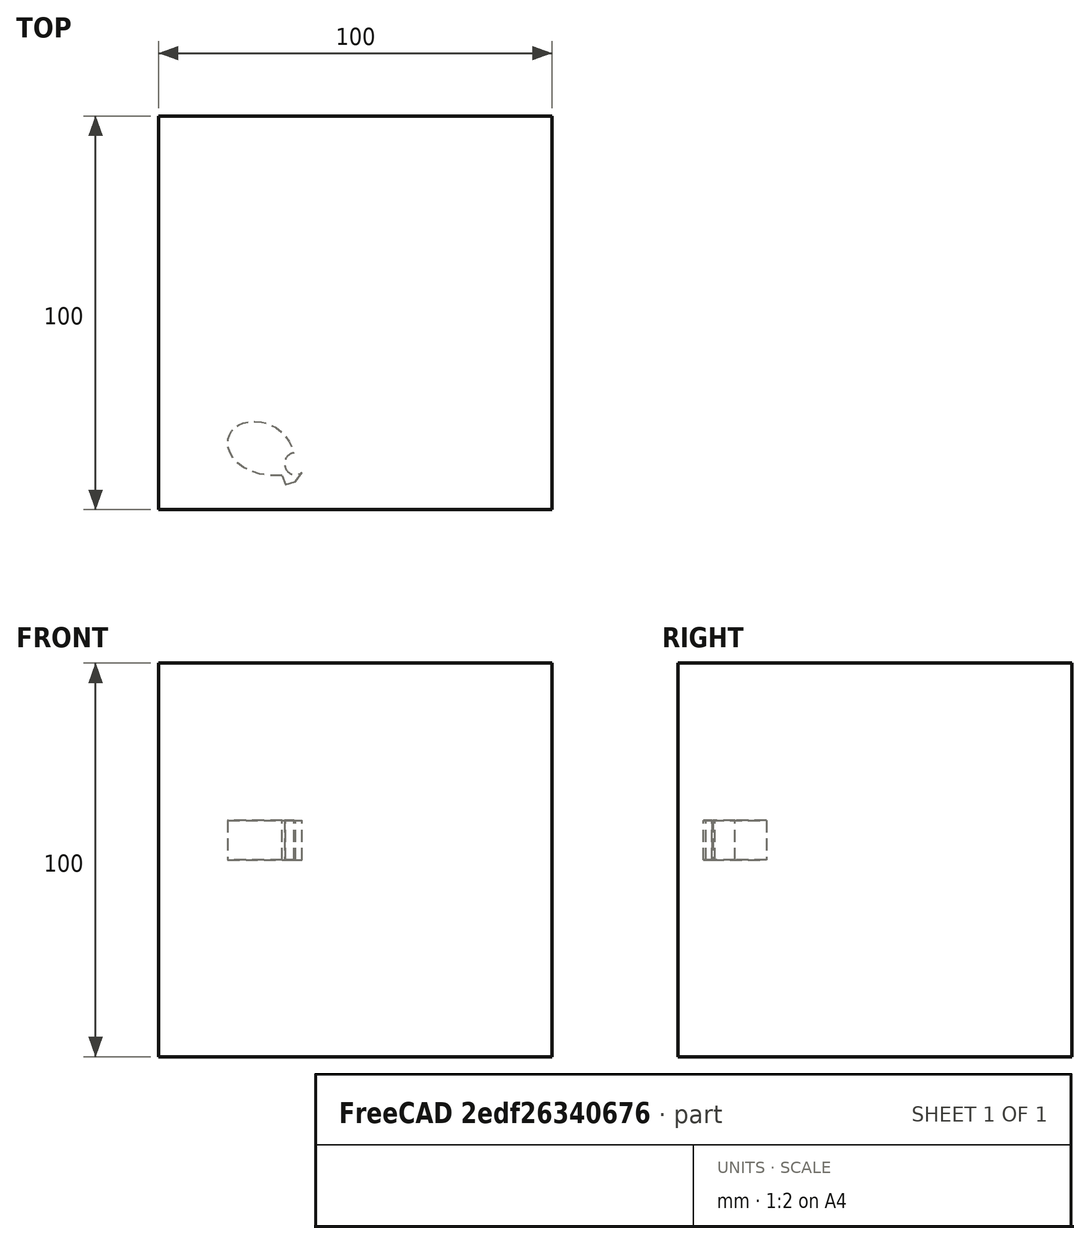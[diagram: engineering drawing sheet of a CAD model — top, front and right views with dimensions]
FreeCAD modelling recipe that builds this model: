
FCSTD DOCUMENT  (FreeCAD 1.0R39109 (Git))
Label: mirrorTest-3
License: All rights reserved
LicenseURL: http://en.wikipedia.org/wiki/All_rights_reserved
objects: App::DocumentObjectGroupPython×1248, Part::Mirroring×2, App::Part×2, Part::FeaturePython×1, Sketcher::SketchObject×1, Part::Extrusion×1
note: 6 computed .brp shape members not serialized (recipe doc carries the construction recipe); baked Part::Feature solids carry a one-line shape summary decoded from their .brp

FEATURE [App::DocumentObjectGroupPython] HALFPI  # scripted group (container) (typed FeaturePython)
  name = HALFPI
  value = pi/2.
FEATURE [App::DocumentObjectGroupPython] PI  # scripted group (container) (typed FeaturePython)
  name = PI
  value = 1.*pi
FEATURE [App::DocumentObjectGroupPython] TWOPI  # scripted group (container) (typed FeaturePython)
  name = TWOPI
  value = 2.*pi
FEATURE [App::DocumentObjectGroupPython] Constants  # scripted group (container) (typed FeaturePython)
  Group = -> [HALFPI,PI,TWOPI]
FEATURE [App::DocumentObjectGroupPython] Variables  # scripted group (container) (typed FeaturePython)
FEATURE [App::DocumentObjectGroupPython] Quantities  # scripted group (container) (typed FeaturePython)
FEATURE [App::DocumentObjectGroupPython] Isotopes  # scripted group (container) (typed FeaturePython)
FEATURE [App::DocumentObjectGroupPython] Elements  # scripted group (container) (typed FeaturePython)
FEATURE [App::DocumentObjectGroupPython] G4Isotopes  # scripted group (container) (typed FeaturePython)
FEATURE [App::DocumentObjectGroupPython] H_element  # scripted group (container) (typed FeaturePython)
  Z = 1
  atom_value = 1.008
  formula = H
  name = H_element
FEATURE [App::DocumentObjectGroupPython] He_element  # scripted group (container) (typed FeaturePython)
  Z = 2
  atom_value = 4.0026
  formula = He
  name = He_element
FEATURE [App::DocumentObjectGroupPython] Li_element  # scripted group (container) (typed FeaturePython)
  Z = 3
  atom_value = 6.94
  formula = Li
  name = Li_element
FEATURE [App::DocumentObjectGroupPython] Be_element  # scripted group (container) (typed FeaturePython)
  Z = 4
  atom_value = 9.01218
  formula = Be
  name = Be_element
FEATURE [App::DocumentObjectGroupPython] B_element  # scripted group (container) (typed FeaturePython)
  Z = 5
  atom_value = 10.81
  formula = B
  name = B_element
FEATURE [App::DocumentObjectGroupPython] C_element  # scripted group (container) (typed FeaturePython)
  Z = 6
  atom_value = 12.011
  formula = C
  name = C_element
FEATURE [App::DocumentObjectGroupPython] N_element  # scripted group (container) (typed FeaturePython)
  Z = 7
  atom_value = 14.007
  formula = N
  name = N_element
FEATURE [App::DocumentObjectGroupPython] O_element  # scripted group (container) (typed FeaturePython)
  Z = 8
  atom_value = 15.999
  formula = O
  name = O_element
FEATURE [App::DocumentObjectGroupPython] F_element  # scripted group (container) (typed FeaturePython)
  Z = 9
  atom_value = 18.9984
  formula = F
  name = F_element
FEATURE [App::DocumentObjectGroupPython] Ne_element  # scripted group (container) (typed FeaturePython)
  Z = 10
  atom_value = 20.1797
  formula = Ne
  name = Ne_element
FEATURE [App::DocumentObjectGroupPython] Na_element  # scripted group (container) (typed FeaturePython)
  Z = 11
  atom_value = 22.9898
  formula = Na
  name = Na_element
FEATURE [App::DocumentObjectGroupPython] Mg_element  # scripted group (container) (typed FeaturePython)
  Z = 12
  atom_value = 24.305
  formula = Mg
  name = Mg_element
FEATURE [App::DocumentObjectGroupPython] Al_element  # scripted group (container) (typed FeaturePython)
  Z = 13
  atom_value = 26.9815
  formula = Al
  name = Al_element
FEATURE [App::DocumentObjectGroupPython] Si_element  # scripted group (container) (typed FeaturePython)
  Z = 14
  atom_value = 28.085
  formula = Si
  name = Si_element
FEATURE [App::DocumentObjectGroupPython] P_element  # scripted group (container) (typed FeaturePython)
  Z = 15
  atom_value = 30.9738
  formula = P
  name = P_element
FEATURE [App::DocumentObjectGroupPython] S_element  # scripted group (container) (typed FeaturePython)
  Z = 16
  atom_value = 32.06
  formula = S
  name = S_element
FEATURE [App::DocumentObjectGroupPython] Cl_element  # scripted group (container) (typed FeaturePython)
  Z = 17
  atom_value = 35.45
  formula = Cl
  name = Cl_element
FEATURE [App::DocumentObjectGroupPython] Ar_element  # scripted group (container) (typed FeaturePython)
  Z = 18
  atom_value = 39.95
  formula = Ar
  name = Ar_element
FEATURE [App::DocumentObjectGroupPython] K_element  # scripted group (container) (typed FeaturePython)
  Z = 19
  atom_value = 39.0983
  formula = K
  name = K_element
FEATURE [App::DocumentObjectGroupPython] Ca_element  # scripted group (container) (typed FeaturePython)
  Z = 20
  atom_value = 40.078
  formula = Ca
  name = Ca_element
FEATURE [App::DocumentObjectGroupPython] Sc_element  # scripted group (container) (typed FeaturePython)
  Z = 21
  atom_value = 44.9559
  formula = Sc
  name = Sc_element
FEATURE [App::DocumentObjectGroupPython] Ti_element  # scripted group (container) (typed FeaturePython)
  Z = 22
  atom_value = 47.867
  formula = Ti
  name = Ti_element
FEATURE [App::DocumentObjectGroupPython] V_element  # scripted group (container) (typed FeaturePython)
  Z = 23
  atom_value = 50.9415
  formula = V
  name = V_element
FEATURE [App::DocumentObjectGroupPython] Cr_element  # scripted group (container) (typed FeaturePython)
  Z = 24
  atom_value = 51.9961
  formula = Cr
  name = Cr_element
FEATURE [App::DocumentObjectGroupPython] Mn_element  # scripted group (container) (typed FeaturePython)
  Z = 25
  atom_value = 54.938
  formula = Mn
  name = Mn_element
FEATURE [App::DocumentObjectGroupPython] Fe_element  # scripted group (container) (typed FeaturePython)
  Z = 26
  atom_value = 55.845
  formula = Fe
  name = Fe_element
FEATURE [App::DocumentObjectGroupPython] Co_element  # scripted group (container) (typed FeaturePython)
  Z = 27
  atom_value = 58.9332
  formula = Co
  name = Co_element
FEATURE [App::DocumentObjectGroupPython] Ni_element  # scripted group (container) (typed FeaturePython)
  Z = 28
  atom_value = 58.6934
  formula = Ni
  name = Ni_element
FEATURE [App::DocumentObjectGroupPython] Cu_element  # scripted group (container) (typed FeaturePython)
  Z = 29
  atom_value = 63.546
  formula = Cu
  name = Cu_element
FEATURE [App::DocumentObjectGroupPython] Zn_element  # scripted group (container) (typed FeaturePython)
  Z = 30
  atom_value = 65.38
  formula = Zn
  name = Zn_element
FEATURE [App::DocumentObjectGroupPython] Ga_element  # scripted group (container) (typed FeaturePython)
  Z = 31
  atom_value = 69.723
  formula = Ga
  name = Ga_element
FEATURE [App::DocumentObjectGroupPython] Ge_element  # scripted group (container) (typed FeaturePython)
  Z = 32
  atom_value = 72.63
  formula = Ge
  name = Ge_element
FEATURE [App::DocumentObjectGroupPython] As_element  # scripted group (container) (typed FeaturePython)
  Z = 33
  atom_value = 74.9216
  formula = As
  name = As_element
FEATURE [App::DocumentObjectGroupPython] Se_element  # scripted group (container) (typed FeaturePython)
  Z = 34
  atom_value = 78.971
  formula = Se
  name = Se_element
FEATURE [App::DocumentObjectGroupPython] Br_element  # scripted group (container) (typed FeaturePython)
  Z = 35
  atom_value = 79.904
  formula = Br
  name = Br_element
FEATURE [App::DocumentObjectGroupPython] Kr_element  # scripted group (container) (typed FeaturePython)
  Z = 36
  atom_value = 83.798
  formula = Kr
  name = Kr_element
FEATURE [App::DocumentObjectGroupPython] Rb_element  # scripted group (container) (typed FeaturePython)
  Z = 37
  atom_value = 85.4678
  formula = Rb
  name = Rb_element
FEATURE [App::DocumentObjectGroupPython] Sr_element  # scripted group (container) (typed FeaturePython)
  Z = 38
  atom_value = 87.62
  formula = Sr
  name = Sr_element
FEATURE [App::DocumentObjectGroupPython] Y_element  # scripted group (container) (typed FeaturePython)
  Z = 39
  atom_value = 88.9058
  formula = Y
  name = Y_element
FEATURE [App::DocumentObjectGroupPython] Zr_element  # scripted group (container) (typed FeaturePython)
  Z = 40
  atom_value = 91.224
  formula = Zr
  name = Zr_element
FEATURE [App::DocumentObjectGroupPython] Nb_element  # scripted group (container) (typed FeaturePython)
  Z = 41
  atom_value = 92.9064
  formula = Nb
  name = Nb_element
FEATURE [App::DocumentObjectGroupPython] Mo_element  # scripted group (container) (typed FeaturePython)
  Z = 42
  atom_value = 95.95
  formula = Mo
  name = Mo_element
FEATURE [App::DocumentObjectGroupPython] Tc_element  # scripted group (container) (typed FeaturePython)
  Z = 43
  atom_value = 97
  formula = Tc
  name = Tc_element
FEATURE [App::DocumentObjectGroupPython] Ru_element  # scripted group (container) (typed FeaturePython)
  Z = 44
  atom_value = 101.07
  formula = Ru
  name = Ru_element
FEATURE [App::DocumentObjectGroupPython] Rh_element  # scripted group (container) (typed FeaturePython)
  Z = 45
  atom_value = 102.905
  formula = Rh
  name = Rh_element
FEATURE [App::DocumentObjectGroupPython] Pd_element  # scripted group (container) (typed FeaturePython)
  Z = 46
  atom_value = 106.42
  formula = Pd
  name = Pd_element
FEATURE [App::DocumentObjectGroupPython] Ag_element  # scripted group (container) (typed FeaturePython)
  Z = 47
  atom_value = 107.868
  formula = Ag
  name = Ag_element
FEATURE [App::DocumentObjectGroupPython] Cd_element  # scripted group (container) (typed FeaturePython)
  Z = 48
  atom_value = 112.414
  formula = Cd
  name = Cd_element
FEATURE [App::DocumentObjectGroupPython] In_element  # scripted group (container) (typed FeaturePython)
  Z = 49
  atom_value = 114.818
  formula = In
  name = In_element
FEATURE [App::DocumentObjectGroupPython] Sn_element  # scripted group (container) (typed FeaturePython)
  Z = 50
  atom_value = 118.71
  formula = Sn
  name = Sn_element
FEATURE [App::DocumentObjectGroupPython] Sb_element  # scripted group (container) (typed FeaturePython)
  Z = 51
  atom_value = 121.76
  formula = Sb
  name = Sb_element
FEATURE [App::DocumentObjectGroupPython] Te_element  # scripted group (container) (typed FeaturePython)
  Z = 52
  atom_value = 127.6
  formula = Te
  name = Te_element
FEATURE [App::DocumentObjectGroupPython] I_element  # scripted group (container) (typed FeaturePython)
  Z = 53
  atom_value = 126.904
  formula = I
  name = I_element
FEATURE [App::DocumentObjectGroupPython] Xe_element  # scripted group (container) (typed FeaturePython)
  Z = 54
  atom_value = 131.293
  formula = Xe
  name = Xe_element
FEATURE [App::DocumentObjectGroupPython] Cs_element  # scripted group (container) (typed FeaturePython)
  Z = 55
  atom_value = 132.905
  formula = Cs
  name = Cs_element
FEATURE [App::DocumentObjectGroupPython] Ba_element  # scripted group (container) (typed FeaturePython)
  Z = 56
  atom_value = 137.327
  formula = Ba
  name = Ba_element
FEATURE [App::DocumentObjectGroupPython] La_element  # scripted group (container) (typed FeaturePython)
  Z = 57
  atom_value = 138.905
  formula = La
  name = La_element
FEATURE [App::DocumentObjectGroupPython] Ce_element  # scripted group (container) (typed FeaturePython)
  Z = 58
  atom_value = 140.116
  formula = Ce
  name = Ce_element
FEATURE [App::DocumentObjectGroupPython] Pr_element  # scripted group (container) (typed FeaturePython)
  Z = 59
  atom_value = 140.908
  formula = Pr
  name = Pr_element
FEATURE [App::DocumentObjectGroupPython] Nd_element  # scripted group (container) (typed FeaturePython)
  Z = 60
  atom_value = 144.242
  formula = Nd
  name = Nd_element
FEATURE [App::DocumentObjectGroupPython] Pm_element  # scripted group (container) (typed FeaturePython)
  Z = 61
  atom_value = 145
  formula = Pm
  name = Pm_element
FEATURE [App::DocumentObjectGroupPython] Sm_element  # scripted group (container) (typed FeaturePython)
  Z = 62
  atom_value = 150.36
  formula = Sm
  name = Sm_element
FEATURE [App::DocumentObjectGroupPython] Eu_element  # scripted group (container) (typed FeaturePython)
  Z = 63
  atom_value = 151.964
  formula = Eu
  name = Eu_element
FEATURE [App::DocumentObjectGroupPython] Gd_element  # scripted group (container) (typed FeaturePython)
  Z = 64
  atom_value = 157.25
  formula = Gd
  name = Gd_element
FEATURE [App::DocumentObjectGroupPython] Tb_element  # scripted group (container) (typed FeaturePython)
  Z = 65
  atom_value = 158.925
  formula = Tb
  name = Tb_element
FEATURE [App::DocumentObjectGroupPython] Dy_element  # scripted group (container) (typed FeaturePython)
  Z = 66
  atom_value = 162.5
  formula = Dy
  name = Dy_element
FEATURE [App::DocumentObjectGroupPython] Ho_element  # scripted group (container) (typed FeaturePython)
  Z = 67
  atom_value = 164.93
  formula = Ho
  name = Ho_element
FEATURE [App::DocumentObjectGroupPython] Er_element  # scripted group (container) (typed FeaturePython)
  Z = 68
  atom_value = 167.259
  formula = Er
  name = Er_element
FEATURE [App::DocumentObjectGroupPython] Tm_element  # scripted group (container) (typed FeaturePython)
  Z = 69
  atom_value = 168.934
  formula = Tm
  name = Tm_element
FEATURE [App::DocumentObjectGroupPython] Yb_element  # scripted group (container) (typed FeaturePython)
  Z = 70
  atom_value = 173.045
  formula = Yb
  name = Yb_element
FEATURE [App::DocumentObjectGroupPython] Lu_element  # scripted group (container) (typed FeaturePython)
  Z = 71
  atom_value = 174.967
  formula = Lu
  name = Lu_element
FEATURE [App::DocumentObjectGroupPython] Hf_element  # scripted group (container) (typed FeaturePython)
  Z = 72
  atom_value = 178.49
  formula = Hf
  name = Hf_element
FEATURE [App::DocumentObjectGroupPython] Ta_element  # scripted group (container) (typed FeaturePython)
  Z = 73
  atom_value = 180.948
  formula = Ta
  name = Ta_element
FEATURE [App::DocumentObjectGroupPython] W_element  # scripted group (container) (typed FeaturePython)
  Z = 74
  atom_value = 183.84
  formula = W
  name = W_element
FEATURE [App::DocumentObjectGroupPython] Re_element  # scripted group (container) (typed FeaturePython)
  Z = 75
  atom_value = 186.207
  formula = Re
  name = Re_element
FEATURE [App::DocumentObjectGroupPython] Os_element  # scripted group (container) (typed FeaturePython)
  Z = 76
  atom_value = 190.23
  formula = Os
  name = Os_element
FEATURE [App::DocumentObjectGroupPython] Ir_element  # scripted group (container) (typed FeaturePython)
  Z = 77
  atom_value = 192.217
  formula = Ir
  name = Ir_element
FEATURE [App::DocumentObjectGroupPython] Pt_element  # scripted group (container) (typed FeaturePython)
  Z = 78
  atom_value = 195.084
  formula = Pt
  name = Pt_element
FEATURE [App::DocumentObjectGroupPython] Au_element  # scripted group (container) (typed FeaturePython)
  Z = 79
  atom_value = 196.967
  formula = Au
  name = Au_element
FEATURE [App::DocumentObjectGroupPython] Hg_element  # scripted group (container) (typed FeaturePython)
  Z = 80
  atom_value = 200.592
  formula = Hg
  name = Hg_element
FEATURE [App::DocumentObjectGroupPython] Tl_element  # scripted group (container) (typed FeaturePython)
  Z = 81
  atom_value = 204.38
  formula = Tl
  name = Tl_element
FEATURE [App::DocumentObjectGroupPython] Pb_element  # scripted group (container) (typed FeaturePython)
  Z = 82
  atom_value = 207.2
  formula = Pb
  name = Pb_element
FEATURE [App::DocumentObjectGroupPython] Bi_element  # scripted group (container) (typed FeaturePython)
  Z = 83
  atom_value = 208.98
  formula = Bi
  name = Bi_element
FEATURE [App::DocumentObjectGroupPython] Po_element  # scripted group (container) (typed FeaturePython)
  Z = 84
  atom_value = 209
  formula = Po
  name = Po_element
FEATURE [App::DocumentObjectGroupPython] At_element  # scripted group (container) (typed FeaturePython)
  Z = 85
  atom_value = 210
  formula = At
  name = At_element
FEATURE [App::DocumentObjectGroupPython] Rn_element  # scripted group (container) (typed FeaturePython)
  Z = 86
  atom_value = 222
  formula = Rn
  name = Rn_element
FEATURE [App::DocumentObjectGroupPython] Fr_element  # scripted group (container) (typed FeaturePython)
  Z = 87
  atom_value = 223
  formula = Fr
  name = Fr_element
FEATURE [App::DocumentObjectGroupPython] Ra_element  # scripted group (container) (typed FeaturePython)
  Z = 88
  atom_value = 226
  formula = Ra
  name = Ra_element
FEATURE [App::DocumentObjectGroupPython] Ac_element  # scripted group (container) (typed FeaturePython)
  Z = 89
  atom_value = 227
  formula = Ac
  name = Ac_element
FEATURE [App::DocumentObjectGroupPython] Th_element  # scripted group (container) (typed FeaturePython)
  Z = 90
  atom_value = 232.038
  formula = Th
  name = Th_element
FEATURE [App::DocumentObjectGroupPython] Pa_element  # scripted group (container) (typed FeaturePython)
  Z = 91
  atom_value = 231.036
  formula = Pa
  name = Pa_element
FEATURE [App::DocumentObjectGroupPython] U_element  # scripted group (container) (typed FeaturePython)
  Z = 92
  atom_value = 238.029
  formula = U
  name = U_element
FEATURE [App::DocumentObjectGroupPython] Np_element  # scripted group (container) (typed FeaturePython)
  Z = 93
  atom_value = 237
  formula = Np
  name = Np_element
FEATURE [App::DocumentObjectGroupPython] Pu_element  # scripted group (container) (typed FeaturePython)
  Z = 94
  atom_value = 244
  formula = Pu
  name = Pu_element
FEATURE [App::DocumentObjectGroupPython] Am_element  # scripted group (container) (typed FeaturePython)
  Z = 95
  atom_value = 243
  formula = Am
  name = Am_element
FEATURE [App::DocumentObjectGroupPython] Cm_element  # scripted group (container) (typed FeaturePython)
  Z = 96
  atom_value = 247
  formula = Cm
  name = Cm_element
FEATURE [App::DocumentObjectGroupPython] Bk_element  # scripted group (container) (typed FeaturePython)
  Z = 97
  atom_value = 247
  formula = Bk
  name = Bk_element
FEATURE [App::DocumentObjectGroupPython] Cf_element  # scripted group (container) (typed FeaturePython)
  Z = 98
  atom_value = 251
  formula = Cf
  name = Cf_element
FEATURE [App::DocumentObjectGroupPython] G4Elements  # scripted group (container) (typed FeaturePython)
  Group = -> [H_element,He_element,Li_element,Be_element,B_element,C_element,N_element,O_element,F_element,Ne_element,Na_element,Mg_element,Al_element,Si_element,P_element,S_element,Cl_element,Ar_element,K_element,Ca_element,Sc_element,Ti_element,V_element,Cr_element,Mn_element,Fe_element,Co_element,Ni_element,Cu_element,Zn_element,Ga_element,Ge_element,As_element,Se_element,Br_element,Kr_element,Rb_element,+61 more]
FEATURE [App::DocumentObjectGroupPython] H_element001  label="H_element : 0.101"  # scripted group (container) (typed FeaturePython)
  n = 0.101327
FEATURE [App::DocumentObjectGroupPython] C_element001  label="C_element : 0.775"  # scripted group (container) (typed FeaturePython)
  n = 0.7755
FEATURE [App::DocumentObjectGroupPython] N_element001  label="N_element : 0.035"  # scripted group (container) (typed FeaturePython)
  n = 0.035057
FEATURE [App::DocumentObjectGroupPython] O_element001  label="O_element : 0.052"  # scripted group (container) (typed FeaturePython)
  n = 0.0523159
FEATURE [App::DocumentObjectGroupPython] F_element001  label="F_element : 0.017"  # scripted group (container) (typed FeaturePython)
  n = 0.017422
FEATURE [App::DocumentObjectGroupPython] Ca_element001  label="Ca_element : 0.018"  # scripted group (container) (typed FeaturePython)
  n = 0.018378
FEATURE [App::DocumentObjectGroupPython] G4_A_150_TISSUE  label="G4_A-150_TISSUE"  # scripted group (container) (typed FeaturePython)
  Dunit = g/cm3
  Dvalue = 1.127
  Group = -> [H_element001,C_element001,N_element001,O_element001,F_element001,Ca_element001]
  conduct = 2
  density = 1
  expand = 3
  formula = G4_A-150_TISSUE
  name = G4_A-150_TISSUE
  specific = 4
FEATURE [App::DocumentObjectGroupPython] C_element002  label="C_element : 3"  # scripted group (container) (typed FeaturePython)
  n = 3
  ref = C_element
FEATURE [App::DocumentObjectGroupPython] H_element002  label="H_element : 6"  # scripted group (container) (typed FeaturePython)
  n = 6
  ref = H_element
FEATURE [App::DocumentObjectGroupPython] O_element002  label="O_element : 1"  # scripted group (container) (typed FeaturePython)
  n = 1
  ref = O_element
FEATURE [App::DocumentObjectGroupPython] G4_ACETONE  # scripted group (container) (typed FeaturePython)
  Dunit = g/cm3
  Dvalue = 0.7899
  Group = -> [C_element002,H_element002,O_element002]
  conduct = 2
  density = 1
  expand = 3
  formula = G4_ACETONE
  name = G4_ACETONE
  specific = 4
FEATURE [App::DocumentObjectGroupPython] C_element003  label="C_element : 2"  # scripted group (container) (typed FeaturePython)
  n = 2
  ref = C_element
FEATURE [App::DocumentObjectGroupPython] H_element003  label="H_element : 2"  # scripted group (container) (typed FeaturePython)
  n = 2
  ref = H_element
FEATURE [App::DocumentObjectGroupPython] G4_ACETYLENE  # scripted group (container) (typed FeaturePython)
  Dunit = g/cm3
  Dvalue = 0.0010967
  Group = -> [C_element003,H_element003]
  conduct = 2
  density = 1
  expand = 3
  formula = G4_ACETYLENE
  name = G4_ACETYLENE
  specific = 4
FEATURE [App::DocumentObjectGroupPython] C_element004  label="C_element : 5"  # scripted group (container) (typed FeaturePython)
  n = 5
  ref = C_element
FEATURE [App::DocumentObjectGroupPython] H_element004  label="H_element : 5"  # scripted group (container) (typed FeaturePython)
  n = 5
  ref = H_element
FEATURE [App::DocumentObjectGroupPython] N_element002  label="N_element : 5"  # scripted group (container) (typed FeaturePython)
  n = 5
  ref = N_element
FEATURE [App::DocumentObjectGroupPython] G4_ADENINE  # scripted group (container) (typed FeaturePython)
  Dunit = g/cm3
  Dvalue = 1.6
  Group = -> [C_element004,H_element004,N_element002]
  conduct = 2
  density = 1
  expand = 3
  formula = G4_ADENINE
  name = G4_ADENINE
  specific = 4
FEATURE [App::DocumentObjectGroupPython] H_element005  label="H_element : 0.114"  # scripted group (container) (typed FeaturePython)
  n = 0.114
FEATURE [App::DocumentObjectGroupPython] C_element005  label="C_element : 0.598"  # scripted group (container) (typed FeaturePython)
  n = 0.598
FEATURE [App::DocumentObjectGroupPython] N_element003  label="N_element : 0.007"  # scripted group (container) (typed FeaturePython)
  n = 0.007
FEATURE [App::DocumentObjectGroupPython] O_element003  label="O_element : 0.278"  # scripted group (container) (typed FeaturePython)
  n = 0.278
FEATURE [App::DocumentObjectGroupPython] Na_element001  label="Na_element : 0.001"  # scripted group (container) (typed FeaturePython)
  n = 0.001
FEATURE [App::DocumentObjectGroupPython] S_element001  label="S_element : 0.001"  # scripted group (container) (typed FeaturePython)
  n = 0.001
FEATURE [App::DocumentObjectGroupPython] Cl_element001  label="Cl_element : 0.001"  # scripted group (container) (typed FeaturePython)
  n = 0.001
FEATURE [App::DocumentObjectGroupPython] G4_ADIPOSE_TISSUE_ICRP  # scripted group (container) (typed FeaturePython)
  Dunit = g/cm3
  Dvalue = 0.95
  Group = -> [H_element005,C_element005,N_element003,O_element003,Na_element001,S_element001,Cl_element001]
  conduct = 2
  density = 1
  expand = 3
  formula = G4_ADIPOSE_TISSUE_ICRP
  name = G4_ADIPOSE_TISSUE_ICRP
  specific = 4
FEATURE [App::DocumentObjectGroupPython] C_element006  label="C_element : 0.000"  # scripted group (container) (typed FeaturePython)
  n = 0.000124
FEATURE [App::DocumentObjectGroupPython] N_element004  label="N_element : 0.755"  # scripted group (container) (typed FeaturePython)
  n = 0.755268
FEATURE [App::DocumentObjectGroupPython] O_element004  label="O_element : 0.232"  # scripted group (container) (typed FeaturePython)
  n = 0.231781
FEATURE [App::DocumentObjectGroupPython] Ar_element001  label="Ar_element : 0.013"  # scripted group (container) (typed FeaturePython)
  n = 0.012827
FEATURE [App::DocumentObjectGroupPython] G4_AIR  # scripted group (container) (typed FeaturePython)
  Dunit = g/cm3
  Dvalue = 0.00120479
  Group = -> [C_element006,N_element004,O_element004,Ar_element001]
  conduct = 2
  density = 1
  expand = 3
  formula = G4_AIR
  name = G4_AIR
  specific = 4
FEATURE [App::DocumentObjectGroupPython] C_element007  label="C_element : 006"  # scripted group (container) (typed FeaturePython)
  n = 3
  ref = C_element
FEATURE [App::DocumentObjectGroupPython] H_element006  label="H_element : 7"  # scripted group (container) (typed FeaturePython)
  n = 7
  ref = H_element
FEATURE [App::DocumentObjectGroupPython] N_element005  label="N_element : 1"  # scripted group (container) (typed FeaturePython)
  n = 1
  ref = N_element
FEATURE [App::DocumentObjectGroupPython] O_element005  label="O_element : 2"  # scripted group (container) (typed FeaturePython)
  n = 2
  ref = O_element
FEATURE [App::DocumentObjectGroupPython] G4_ALANINE  # scripted group (container) (typed FeaturePython)
  Dunit = g/cm3
  Dvalue = 1.42
  Group = -> [C_element007,H_element006,N_element005,O_element005]
  conduct = 2
  density = 1
  expand = 3
  formula = G4_ALANINE
  name = G4_ALANINE
  specific = 4
FEATURE [App::DocumentObjectGroupPython] Al_element001  label="Al_element : 2"  # scripted group (container) (typed FeaturePython)
  n = 2
  ref = Al_element
FEATURE [App::DocumentObjectGroupPython] O_element006  label="O_element : 3"  # scripted group (container) (typed FeaturePython)
  n = 3
  ref = O_element
FEATURE [App::DocumentObjectGroupPython] G4_ALUMINUM_OXIDE  # scripted group (container) (typed FeaturePython)
  Dunit = g/cm3
  Dvalue = 3.97
  Group = -> [Al_element001,O_element006]
  conduct = 2
  density = 1
  expand = 3
  formula = G4_ALUMINUM_OXIDE
  name = G4_ALUMINUM_OXIDE
  specific = 4
FEATURE [App::DocumentObjectGroupPython] H_element007  label="H_element : 0.106"  # scripted group (container) (typed FeaturePython)
  n = 0.10593
FEATURE [App::DocumentObjectGroupPython] C_element008  label="C_element : 0.789"  # scripted group (container) (typed FeaturePython)
  n = 0.788974
FEATURE [App::DocumentObjectGroupPython] O_element007  label="O_element : 0.105"  # scripted group (container) (typed FeaturePython)
  n = 0.105096
FEATURE [App::DocumentObjectGroupPython] G4_AMBER  # scripted group (container) (typed FeaturePython)
  Dunit = g/cm3
  Dvalue = 1.1
  Group = -> [H_element007,C_element008,O_element007]
  conduct = 2
  density = 1
  expand = 3
  formula = G4_AMBER
  name = G4_AMBER
  specific = 4
FEATURE [App::DocumentObjectGroupPython] N_element006  label="N_element : 006"  # scripted group (container) (typed FeaturePython)
  n = 1
  ref = N_element
FEATURE [App::DocumentObjectGroupPython] H_element008  label="H_element : 3"  # scripted group (container) (typed FeaturePython)
  n = 3
  ref = H_element
FEATURE [App::DocumentObjectGroupPython] G4_AMMONIA  # scripted group (container) (typed FeaturePython)
  Dunit = g/cm3
  Dvalue = 0.000826019
  Group = -> [N_element006,H_element008]
  conduct = 2
  density = 1
  expand = 3
  formula = G4_AMMONIA
  name = G4_AMMONIA
  specific = 4
FEATURE [App::DocumentObjectGroupPython] C_element009  label="C_element : 6"  # scripted group (container) (typed FeaturePython)
  n = 6
  ref = C_element
FEATURE [App::DocumentObjectGroupPython] H_element009  label="H_element : 008"  # scripted group (container) (typed FeaturePython)
  n = 7
  ref = H_element
FEATURE [App::DocumentObjectGroupPython] N_element007  label="N_element : 007"  # scripted group (container) (typed FeaturePython)
  n = 1
  ref = N_element
FEATURE [App::DocumentObjectGroupPython] G4_ANILINE  # scripted group (container) (typed FeaturePython)
  Dunit = g/cm3
  Dvalue = 1.0235
  Group = -> [C_element009,H_element009,N_element007]
  conduct = 2
  density = 1
  expand = 3
  formula = G4_ANILINE
  name = G4_ANILINE
  specific = 4
FEATURE [App::DocumentObjectGroupPython] C_element010  label="C_element : 14"  # scripted group (container) (typed FeaturePython)
  n = 14
  ref = C_element
FEATURE [App::DocumentObjectGroupPython] H_element010  label="H_element : 10"  # scripted group (container) (typed FeaturePython)
  n = 10
  ref = H_element
FEATURE [App::DocumentObjectGroupPython] G4_ANTHRACENE  # scripted group (container) (typed FeaturePython)
  Dunit = g/cm3
  Dvalue = 1.283
  Group = -> [C_element010,H_element010]
  conduct = 2
  density = 1
  expand = 3
  formula = G4_ANTHRACENE
  name = G4_ANTHRACENE
  specific = 4
FEATURE [App::DocumentObjectGroupPython] H_element011  label="H_element : 0.065"  # scripted group (container) (typed FeaturePython)
  n = 0.0654709
FEATURE [App::DocumentObjectGroupPython] C_element011  label="C_element : 0.537"  # scripted group (container) (typed FeaturePython)
  n = 0.536944
FEATURE [App::DocumentObjectGroupPython] N_element008  label="N_element : 0.021"  # scripted group (container) (typed FeaturePython)
  n = 0.0215
FEATURE [App::DocumentObjectGroupPython] O_element008  label="O_element : 0.032"  # scripted group (container) (typed FeaturePython)
  n = 0.032085
FEATURE [App::DocumentObjectGroupPython] F_element002  label="F_element : 0.167"  # scripted group (container) (typed FeaturePython)
  n = 0.167411
FEATURE [App::DocumentObjectGroupPython] Ca_element002  label="Ca_element : 0.177"  # scripted group (container) (typed FeaturePython)
  n = 0.176589
FEATURE [App::DocumentObjectGroupPython] G4_B_100_BONE  label="G4_B-100_BONE"  # scripted group (container) (typed FeaturePython)
  Dunit = g/cm3
  Dvalue = 1.45
  Group = -> [H_element011,C_element011,N_element008,O_element008,F_element002,Ca_element002]
  conduct = 2
  density = 1
  expand = 3
  formula = G4_B-100_BONE
  name = G4_B-100_BONE
  specific = 4
FEATURE [App::DocumentObjectGroupPython] H_element012  label="H_element : 0.057"  # scripted group (container) (typed FeaturePython)
  n = 0.057441
FEATURE [App::DocumentObjectGroupPython] C_element012  label="C_element : 0.790"  # scripted group (container) (typed FeaturePython)
  n = 0.774591
FEATURE [App::DocumentObjectGroupPython] O_element009  label="O_element : 0.168"  # scripted group (container) (typed FeaturePython)
  n = 0.167968
FEATURE [App::DocumentObjectGroupPython] G4_BAKELITE  # scripted group (container) (typed FeaturePython)
  Dunit = g/cm3
  Dvalue = 1.25
  Group = -> [H_element012,C_element012,O_element009]
  conduct = 2
  density = 1
  expand = 3
  formula = G4_BAKELITE
  name = G4_BAKELITE
  specific = 4
FEATURE [App::DocumentObjectGroupPython] Ba_element001  label="Ba_element : 1"  # scripted group (container) (typed FeaturePython)
  n = 1
  ref = Ba_element
FEATURE [App::DocumentObjectGroupPython] F_element003  label="F_element : 2"  # scripted group (container) (typed FeaturePython)
  n = 2
  ref = F_element
FEATURE [App::DocumentObjectGroupPython] G4_BARIUM_FLUORIDE  # scripted group (container) (typed FeaturePython)
  Dunit = g/cm3
  Dvalue = 4.89
  Group = -> [Ba_element001,F_element003]
  conduct = 2
  density = 1
  expand = 3
  formula = G4_BARIUM_FLUORIDE
  name = G4_BARIUM_FLUORIDE
  specific = 4
FEATURE [App::DocumentObjectGroupPython] Ba_element002  label="Ba_element : 002"  # scripted group (container) (typed FeaturePython)
  n = 1
  ref = Ba_element
FEATURE [App::DocumentObjectGroupPython] S_element002  label="S_element : 1"  # scripted group (container) (typed FeaturePython)
  n = 1
  ref = S_element
FEATURE [App::DocumentObjectGroupPython] O_element010  label="O_element : 4"  # scripted group (container) (typed FeaturePython)
  n = 4
  ref = O_element
FEATURE [App::DocumentObjectGroupPython] G4_BARIUM_SULFATE  # scripted group (container) (typed FeaturePython)
  Dunit = g/cm3
  Dvalue = 4.5
  Group = -> [Ba_element002,S_element002,O_element010]
  conduct = 2
  density = 1
  expand = 3
  formula = G4_BARIUM_SULFATE
  name = G4_BARIUM_SULFATE
  specific = 4
FEATURE [App::DocumentObjectGroupPython] C_element013  label="C_element : 007"  # scripted group (container) (typed FeaturePython)
  n = 6
  ref = C_element
FEATURE [App::DocumentObjectGroupPython] H_element013  label="H_element : 009"  # scripted group (container) (typed FeaturePython)
  n = 6
  ref = H_element
FEATURE [App::DocumentObjectGroupPython] G4_BENZENE  # scripted group (container) (typed FeaturePython)
  Dunit = g/cm3
  Dvalue = 0.87865
  Group = -> [C_element013,H_element013]
  conduct = 2
  density = 1
  expand = 3
  formula = G4_BENZENE
  name = G4_BENZENE
  specific = 4
FEATURE [App::DocumentObjectGroupPython] Be_element001  label="Be_element : 1"  # scripted group (container) (typed FeaturePython)
  n = 1
  ref = Be_element
FEATURE [App::DocumentObjectGroupPython] O_element011  label="O_element : 005"  # scripted group (container) (typed FeaturePython)
  n = 1
  ref = O_element
FEATURE [App::DocumentObjectGroupPython] G4_BERYLLIUM_OXIDE  # scripted group (container) (typed FeaturePython)
  Dunit = g/cm3
  Dvalue = 3.01
  Group = -> [Be_element001,O_element011]
  conduct = 2
  density = 1
  expand = 3
  formula = G4_BERYLLIUM_OXIDE
  name = G4_BERYLLIUM_OXIDE
  specific = 4
FEATURE [App::DocumentObjectGroupPython] Bi_element001  label="Bi_element : 4"  # scripted group (container) (typed FeaturePython)
  n = 4
  ref = Bi_element
FEATURE [App::DocumentObjectGroupPython] Ge_element001  label="Ge_element : 3"  # scripted group (container) (typed FeaturePython)
  n = 3
  ref = Ge_element
FEATURE [App::DocumentObjectGroupPython] O_element012  label="O_element : 12"  # scripted group (container) (typed FeaturePython)
  n = 12
  ref = O_element
FEATURE [App::DocumentObjectGroupPython] G4_BGO  # scripted group (container) (typed FeaturePython)
  Dunit = g/cm3
  Dvalue = 7.13
  Group = -> [Bi_element001,Ge_element001,O_element012]
  conduct = 2
  density = 1
  expand = 3
  formula = G4_BGO
  name = G4_BGO
  specific = 4
FEATURE [App::DocumentObjectGroupPython] H_element014  label="H_element : 0.102"  # scripted group (container) (typed FeaturePython)
  n = 0.102
FEATURE [App::DocumentObjectGroupPython] C_element014  label="C_element : 0.110"  # scripted group (container) (typed FeaturePython)
  n = 0.11
FEATURE [App::DocumentObjectGroupPython] N_element009  label="N_element : 0.033"  # scripted group (container) (typed FeaturePython)
  n = 0.033
FEATURE [App::DocumentObjectGroupPython] O_element013  label="O_element : 0.745"  # scripted group (container) (typed FeaturePython)
  n = 0.745
FEATURE [App::DocumentObjectGroupPython] Na_element002  label="Na_element : 0.002"  # scripted group (container) (typed FeaturePython)
  n = 0.001
FEATURE [App::DocumentObjectGroupPython] P_element001  label="P_element : 0.001"  # scripted group (container) (typed FeaturePython)
  n = 0.001
FEATURE [App::DocumentObjectGroupPython] S_element003  label="S_element : 0.002"  # scripted group (container) (typed FeaturePython)
  n = 0.002
FEATURE [App::DocumentObjectGroupPython] Cl_element002  label="Cl_element : 0.003"  # scripted group (container) (typed FeaturePython)
  n = 0.003
FEATURE [App::DocumentObjectGroupPython] K_element001  label="K_element : 0.002"  # scripted group (container) (typed FeaturePython)
  n = 0.002
FEATURE [App::DocumentObjectGroupPython] Fe_element001  label="Fe_element : 0.001"  # scripted group (container) (typed FeaturePython)
  n = 0.001
FEATURE [App::DocumentObjectGroupPython] G4_BLOOD_ICRP  # scripted group (container) (typed FeaturePython)
  Dunit = g/cm3
  Dvalue = 1.06
  Group = -> [H_element014,C_element014,N_element009,O_element013,Na_element002,P_element001,S_element003,Cl_element002,K_element001,Fe_element001]
  conduct = 2
  density = 1
  expand = 3
  formula = G4_BLOOD_ICRP
  name = G4_BLOOD_ICRP
  specific = 4
FEATURE [App::DocumentObjectGroupPython] H_element015  label="H_element : 0.064"  # scripted group (container) (typed FeaturePython)
  n = 0.064
FEATURE [App::DocumentObjectGroupPython] C_element015  label="C_element : 0.278"  # scripted group (container) (typed FeaturePython)
  n = 0.278
FEATURE [App::DocumentObjectGroupPython] N_element010  label="N_element : 0.027"  # scripted group (container) (typed FeaturePython)
  n = 0.027
FEATURE [App::DocumentObjectGroupPython] O_element014  label="O_element : 0.410"  # scripted group (container) (typed FeaturePython)
  n = 0.41
FEATURE [App::DocumentObjectGroupPython] Mg_element001  label="Mg_element : 0.002"  # scripted group (container) (typed FeaturePython)
  n = 0.002
FEATURE [App::DocumentObjectGroupPython] P_element002  label="P_element : 0.070"  # scripted group (container) (typed FeaturePython)
  n = 0.07
FEATURE [App::DocumentObjectGroupPython] S_element004  label="S_element : 0.003"  # scripted group (container) (typed FeaturePython)
  n = 0.002
FEATURE [App::DocumentObjectGroupPython] Ca_element003  label="Ca_element : 0.147"  # scripted group (container) (typed FeaturePython)
  n = 0.147
FEATURE [App::DocumentObjectGroupPython] G4_BONE_COMPACT_ICRU  # scripted group (container) (typed FeaturePython)
  Dunit = g/cm3
  Dvalue = 1.85
  Group = -> [H_element015,C_element015,N_element010,O_element014,Mg_element001,P_element002,S_element004,Ca_element003]
  conduct = 2
  density = 1
  expand = 3
  formula = G4_BONE_COMPACT_ICRU
  name = G4_BONE_COMPACT_ICRU
  specific = 4
FEATURE [App::DocumentObjectGroupPython] H_element016  label="H_element : 0.034"  # scripted group (container) (typed FeaturePython)
  n = 0.034
FEATURE [App::DocumentObjectGroupPython] C_element016  label="C_element : 0.155"  # scripted group (container) (typed FeaturePython)
  n = 0.155
FEATURE [App::DocumentObjectGroupPython] N_element011  label="N_element : 0.042"  # scripted group (container) (typed FeaturePython)
  n = 0.042
FEATURE [App::DocumentObjectGroupPython] O_element015  label="O_element : 0.435"  # scripted group (container) (typed FeaturePython)
  n = 0.435
FEATURE [App::DocumentObjectGroupPython] Na_element003  label="Na_element : 0.003"  # scripted group (container) (typed FeaturePython)
  n = 0.001
FEATURE [App::DocumentObjectGroupPython] Mg_element002  label="Mg_element : 0.003"  # scripted group (container) (typed FeaturePython)
  n = 0.002
FEATURE [App::DocumentObjectGroupPython] P_element003  label="P_element : 0.103"  # scripted group (container) (typed FeaturePython)
  n = 0.103
FEATURE [App::DocumentObjectGroupPython] S_element005  label="S_element : 0.004"  # scripted group (container) (typed FeaturePython)
  n = 0.003
FEATURE [App::DocumentObjectGroupPython] Ca_element004  label="Ca_element : 0.225"  # scripted group (container) (typed FeaturePython)
  n = 0.225
FEATURE [App::DocumentObjectGroupPython] G4_BONE_CORTICAL_ICRP  # scripted group (container) (typed FeaturePython)
  Dunit = g/cm3
  Dvalue = 1.92
  Group = -> [H_element016,C_element016,N_element011,O_element015,Na_element003,Mg_element002,P_element003,S_element005,Ca_element004]
  conduct = 2
  density = 1
  expand = 3
  formula = G4_BONE_CORTICAL_ICRP
  name = G4_BONE_CORTICAL_ICRP
  specific = 4
FEATURE [App::DocumentObjectGroupPython] B_element001  label="B_element : 4"  # scripted group (container) (typed FeaturePython)
  n = 4
  ref = B_element
FEATURE [App::DocumentObjectGroupPython] C_element017  label="C_element : 1"  # scripted group (container) (typed FeaturePython)
  n = 1
  ref = C_element
FEATURE [App::DocumentObjectGroupPython] G4_BORON_CARBIDE  # scripted group (container) (typed FeaturePython)
  Dunit = g/cm3
  Dvalue = 2.52
  Group = -> [B_element001,C_element017]
  conduct = 2
  density = 1
  expand = 3
  formula = G4_BORON_CARBIDE
  name = G4_BORON_CARBIDE
  specific = 4
FEATURE [App::DocumentObjectGroupPython] B_element002  label="B_element : 2"  # scripted group (container) (typed FeaturePython)
  n = 2
  ref = B_element
FEATURE [App::DocumentObjectGroupPython] O_element016  label="O_element : 006"  # scripted group (container) (typed FeaturePython)
  n = 3
  ref = O_element
FEATURE [App::DocumentObjectGroupPython] G4_BORON_OXIDE  # scripted group (container) (typed FeaturePython)
  Dunit = g/cm3
  Dvalue = 1.812
  Group = -> [B_element002,O_element016]
  conduct = 2
  density = 1
  expand = 3
  formula = G4_BORON_OXIDE
  name = G4_BORON_OXIDE
  specific = 4
FEATURE [App::DocumentObjectGroupPython] H_element017  label="H_element : 0.107"  # scripted group (container) (typed FeaturePython)
  n = 0.107
FEATURE [App::DocumentObjectGroupPython] C_element018  label="C_element : 0.145"  # scripted group (container) (typed FeaturePython)
  n = 0.145
FEATURE [App::DocumentObjectGroupPython] N_element012  label="N_element : 0.022"  # scripted group (container) (typed FeaturePython)
  n = 0.022
FEATURE [App::DocumentObjectGroupPython] O_element017  label="O_element : 0.712"  # scripted group (container) (typed FeaturePython)
  n = 0.712
FEATURE [App::DocumentObjectGroupPython] Na_element004  label="Na_element : 0.004"  # scripted group (container) (typed FeaturePython)
  n = 0.002
FEATURE [App::DocumentObjectGroupPython] P_element004  label="P_element : 0.004"  # scripted group (container) (typed FeaturePython)
  n = 0.004
FEATURE [App::DocumentObjectGroupPython] S_element006  label="S_element : 0.005"  # scripted group (container) (typed FeaturePython)
  n = 0.002
FEATURE [App::DocumentObjectGroupPython] Cl_element003  label="Cl_element : 0.004"  # scripted group (container) (typed FeaturePython)
  n = 0.003
FEATURE [App::DocumentObjectGroupPython] K_element002  label="K_element : 0.003"  # scripted group (container) (typed FeaturePython)
  n = 0.003
FEATURE [App::DocumentObjectGroupPython] G4_BRAIN_ICRP  # scripted group (container) (typed FeaturePython)
  Dunit = g/cm3
  Dvalue = 1.04
  Group = -> [H_element017,C_element018,N_element012,O_element017,Na_element004,P_element004,S_element006,Cl_element003,K_element002]
  conduct = 2
  density = 1
  expand = 3
  formula = G4_BRAIN_ICRP
  name = G4_BRAIN_ICRP
  specific = 4
FEATURE [App::DocumentObjectGroupPython] C_element019  label="C_element : 4"  # scripted group (container) (typed FeaturePython)
  n = 4
  ref = C_element
FEATURE [App::DocumentObjectGroupPython] H_element018  label="H_element : 010"  # scripted group (container) (typed FeaturePython)
  n = 10
  ref = H_element
FEATURE [App::DocumentObjectGroupPython] G4_BUTANE  # scripted group (container) (typed FeaturePython)
  Dunit = g/cm3
  Dvalue = 0.00249343
  Group = -> [C_element019,H_element018]
  conduct = 2
  density = 1
  expand = 3
  formula = G4_BUTANE
  name = G4_BUTANE
  specific = 4
FEATURE [App::DocumentObjectGroupPython] C_element020  label="C_element : 008"  # scripted group (container) (typed FeaturePython)
  n = 4
  ref = C_element
FEATURE [App::DocumentObjectGroupPython] H_element019  label="H_element : 011"  # scripted group (container) (typed FeaturePython)
  n = 10
  ref = H_element
FEATURE [App::DocumentObjectGroupPython] O_element018  label="O_element : 007"  # scripted group (container) (typed FeaturePython)
  n = 1
  ref = O_element
FEATURE [App::DocumentObjectGroupPython] G4_N_BUTYL_ALCOHOL  label="G4_N-BUTYL_ALCOHOL"  # scripted group (container) (typed FeaturePython)
  Dunit = g/cm3
  Dvalue = 0.8098
  Group = -> [C_element020,H_element019,O_element018]
  conduct = 2
  density = 1
  expand = 3
  formula = G4_N-BUTYL_ALCOHOL
  name = G4_N-BUTYL_ALCOHOL
  specific = 4
FEATURE [App::DocumentObjectGroupPython] H_element020  label="H_element : 0.025"  # scripted group (container) (typed FeaturePython)
  n = 0.02468
FEATURE [App::DocumentObjectGroupPython] C_element021  label="C_element : 0.502"  # scripted group (container) (typed FeaturePython)
  n = 0.501611
FEATURE [App::DocumentObjectGroupPython] O_element019  label="O_element : 0.005"  # scripted group (container) (typed FeaturePython)
  n = 0.004527
FEATURE [App::DocumentObjectGroupPython] F_element004  label="F_element : 0.465"  # scripted group (container) (typed FeaturePython)
  n = 0.465209
FEATURE [App::DocumentObjectGroupPython] Si_element001  label="Si_element : 0.004"  # scripted group (container) (typed FeaturePython)
  n = 0.003973
FEATURE [App::DocumentObjectGroupPython] G4_C_552  label="G4_C-552"  # scripted group (container) (typed FeaturePython)
  Dunit = g/cm3
  Dvalue = 1.76
  Group = -> [H_element020,C_element021,O_element019,F_element004,Si_element001]
  conduct = 2
  density = 1
  expand = 3
  formula = G4_C-552
  name = G4_C-552
  specific = 4
FEATURE [App::DocumentObjectGroupPython] Cd_element001  label="Cd_element : 1"  # scripted group (container) (typed FeaturePython)
  n = 1
  ref = Cd_element
FEATURE [App::DocumentObjectGroupPython] Te_element001  label="Te_element : 1"  # scripted group (container) (typed FeaturePython)
  n = 1
  ref = Te_element
FEATURE [App::DocumentObjectGroupPython] G4_CADMIUM_TELLURIDE  # scripted group (container) (typed FeaturePython)
  Dunit = g/cm3
  Dvalue = 6.2
  Group = -> [Cd_element001,Te_element001]
  conduct = 2
  density = 1
  expand = 3
  formula = G4_CADMIUM_TELLURIDE
  name = G4_CADMIUM_TELLURIDE
  specific = 4
FEATURE [App::DocumentObjectGroupPython] Cd_element002  label="Cd_element : 002"  # scripted group (container) (typed FeaturePython)
  n = 1
  ref = Cd_element
FEATURE [App::DocumentObjectGroupPython] W_element001  label="W_element : 1"  # scripted group (container) (typed FeaturePython)
  n = 1
  ref = W_element
FEATURE [App::DocumentObjectGroupPython] O_element020  label="O_element : 008"  # scripted group (container) (typed FeaturePython)
  n = 4
  ref = O_element
FEATURE [App::DocumentObjectGroupPython] G4_CADMIUM_TUNGSTATE  # scripted group (container) (typed FeaturePython)
  Dunit = g/cm3
  Dvalue = 7.9
  Group = -> [Cd_element002,W_element001,O_element020]
  conduct = 2
  density = 1
  expand = 3
  formula = G4_CADMIUM_TUNGSTATE
  name = G4_CADMIUM_TUNGSTATE
  specific = 4
FEATURE [App::DocumentObjectGroupPython] Ca_element005  label="Ca_element : 1"  # scripted group (container) (typed FeaturePython)
  n = 1
  ref = Ca_element
FEATURE [App::DocumentObjectGroupPython] C_element022  label="C_element : 009"  # scripted group (container) (typed FeaturePython)
  n = 1
  ref = C_element
FEATURE [App::DocumentObjectGroupPython] O_element021  label="O_element : 009"  # scripted group (container) (typed FeaturePython)
  n = 3
  ref = O_element
FEATURE [App::DocumentObjectGroupPython] G4_CALCIUM_CARBONATE  # scripted group (container) (typed FeaturePython)
  Dunit = g/cm3
  Dvalue = 2.8
  Group = -> [Ca_element005,C_element022,O_element021]
  conduct = 2
  density = 1
  expand = 3
  formula = G4_CALCIUM_CARBONATE
  name = G4_CALCIUM_CARBONATE
  specific = 4
FEATURE [App::DocumentObjectGroupPython] Ca_element006  label="Ca_element : 002"  # scripted group (container) (typed FeaturePython)
  n = 1
  ref = Ca_element
FEATURE [App::DocumentObjectGroupPython] F_element005  label="F_element : 003"  # scripted group (container) (typed FeaturePython)
  n = 2
  ref = F_element
FEATURE [App::DocumentObjectGroupPython] G4_CALCIUM_FLUORIDE  # scripted group (container) (typed FeaturePython)
  Dunit = g/cm3
  Dvalue = 3.18
  Group = -> [Ca_element006,F_element005]
  conduct = 2
  density = 1
  expand = 3
  formula = G4_CALCIUM_FLUORIDE
  name = G4_CALCIUM_FLUORIDE
  specific = 4
FEATURE [App::DocumentObjectGroupPython] Ca_element007  label="Ca_element : 003"  # scripted group (container) (typed FeaturePython)
  n = 1
  ref = Ca_element
FEATURE [App::DocumentObjectGroupPython] O_element022  label="O_element : 010"  # scripted group (container) (typed FeaturePython)
  n = 1
  ref = O_element
FEATURE [App::DocumentObjectGroupPython] G4_CALCIUM_OXIDE  # scripted group (container) (typed FeaturePython)
  Dunit = g/cm3
  Dvalue = 3.3
  Group = -> [Ca_element007,O_element022]
  conduct = 2
  density = 1
  expand = 3
  formula = G4_CALCIUM_OXIDE
  name = G4_CALCIUM_OXIDE
  specific = 4
FEATURE [App::DocumentObjectGroupPython] Ca_element008  label="Ca_element : 004"  # scripted group (container) (typed FeaturePython)
  n = 1
  ref = Ca_element
FEATURE [App::DocumentObjectGroupPython] S_element007  label="S_element : 002"  # scripted group (container) (typed FeaturePython)
  n = 1
  ref = S_element
FEATURE [App::DocumentObjectGroupPython] O_element023  label="O_element : 011"  # scripted group (container) (typed FeaturePython)
  n = 4
  ref = O_element
FEATURE [App::DocumentObjectGroupPython] G4_CALCIUM_SULFATE  # scripted group (container) (typed FeaturePython)
  Dunit = g/cm3
  Dvalue = 2.96
  Group = -> [Ca_element008,S_element007,O_element023]
  conduct = 2
  density = 1
  expand = 3
  formula = G4_CALCIUM_SULFATE
  name = G4_CALCIUM_SULFATE
  specific = 4
FEATURE [App::DocumentObjectGroupPython] Ca_element009  label="Ca_element : 005"  # scripted group (container) (typed FeaturePython)
  n = 1
  ref = Ca_element
FEATURE [App::DocumentObjectGroupPython] W_element002  label="W_element : 002"  # scripted group (container) (typed FeaturePython)
  n = 1
  ref = W_element
FEATURE [App::DocumentObjectGroupPython] O_element024  label="O_element : 012"  # scripted group (container) (typed FeaturePython)
  n = 4
  ref = O_element
FEATURE [App::DocumentObjectGroupPython] G4_CALCIUM_TUNGSTATE  # scripted group (container) (typed FeaturePython)
  Dunit = g/cm3
  Dvalue = 6.062
  Group = -> [Ca_element009,W_element002,O_element024]
  conduct = 2
  density = 1
  expand = 3
  formula = G4_CALCIUM_TUNGSTATE
  name = G4_CALCIUM_TUNGSTATE
  specific = 4
FEATURE [App::DocumentObjectGroupPython] C_element023  label="C_element : 010"  # scripted group (container) (typed FeaturePython)
  n = 1
  ref = C_element
FEATURE [App::DocumentObjectGroupPython] O_element025  label="O_element : 013"  # scripted group (container) (typed FeaturePython)
  n = 2
  ref = O_element
FEATURE [App::DocumentObjectGroupPython] G4_CARBON_DIOXIDE  # scripted group (container) (typed FeaturePython)
  Dunit = g/cm3
  Dvalue = 0.00184212
  Group = -> [C_element023,O_element025]
  conduct = 2
  density = 1
  expand = 3
  formula = G4_CARBON_DIOXIDE
  name = G4_CARBON_DIOXIDE
  specific = 4
FEATURE [App::DocumentObjectGroupPython] C_element024  label="C_element : 011"  # scripted group (container) (typed FeaturePython)
  n = 1
  ref = C_element
FEATURE [App::DocumentObjectGroupPython] Cl_element004  label="Cl_element : 4"  # scripted group (container) (typed FeaturePython)
  n = 4
  ref = Cl_element
FEATURE [App::DocumentObjectGroupPython] G4_CARBON_TETRACHLORIDE  # scripted group (container) (typed FeaturePython)
  Dunit = g/cm3
  Dvalue = 1.594
  Group = -> [C_element024,Cl_element004]
  conduct = 2
  density = 1
  expand = 3
  formula = G4_CARBON_TETRACHLORIDE
  name = G4_CARBON_TETRACHLORIDE
  specific = 4
FEATURE [App::DocumentObjectGroupPython] C_element025  label="C_element : 012"  # scripted group (container) (typed FeaturePython)
  n = 6
  ref = C_element
FEATURE [App::DocumentObjectGroupPython] H_element021  label="H_element : 012"  # scripted group (container) (typed FeaturePython)
  n = 10
  ref = H_element
FEATURE [App::DocumentObjectGroupPython] O_element026  label="O_element : 5"  # scripted group (container) (typed FeaturePython)
  n = 5
  ref = O_element
FEATURE [App::DocumentObjectGroupPython] G4_CELLULOSE_CELLOPHANE  # scripted group (container) (typed FeaturePython)
  Dunit = g/cm3
  Dvalue = 1.42
  Group = -> [C_element025,H_element021,O_element026]
  conduct = 2
  density = 1
  expand = 3
  formula = G4_CELLULOSE_CELLOPHANE
  name = G4_CELLULOSE_CELLOPHANE
  specific = 4
FEATURE [App::DocumentObjectGroupPython] H_element022  label="H_element : 0.067"  # scripted group (container) (typed FeaturePython)
  n = 0.067125
FEATURE [App::DocumentObjectGroupPython] C_element026  label="C_element : 0.545"  # scripted group (container) (typed FeaturePython)
  n = 0.545403
FEATURE [App::DocumentObjectGroupPython] O_element027  label="O_element : 0.387"  # scripted group (container) (typed FeaturePython)
  n = 0.387472
FEATURE [App::DocumentObjectGroupPython] G4_CELLULOSE_BUTYRATE  # scripted group (container) (typed FeaturePython)
  Dunit = g/cm3
  Dvalue = 1.2
  Group = -> [H_element022,C_element026,O_element027]
  conduct = 2
  density = 1
  expand = 3
  formula = G4_CELLULOSE_BUTYRATE
  name = G4_CELLULOSE_BUTYRATE
  specific = 4
FEATURE [App::DocumentObjectGroupPython] H_element023  label="H_element : 0.029"  # scripted group (container) (typed FeaturePython)
  n = 0.029216
FEATURE [App::DocumentObjectGroupPython] C_element027  label="C_element : 0.271"  # scripted group (container) (typed FeaturePython)
  n = 0.271296
FEATURE [App::DocumentObjectGroupPython] N_element013  label="N_element : 0.121"  # scripted group (container) (typed FeaturePython)
  n = 0.121276
FEATURE [App::DocumentObjectGroupPython] O_element028  label="O_element : 0.578"  # scripted group (container) (typed FeaturePython)
  n = 0.578212
FEATURE [App::DocumentObjectGroupPython] G4_CELLULOSE_NITRATE  # scripted group (container) (typed FeaturePython)
  Dunit = g/cm3
  Dvalue = 1.49
  Group = -> [H_element023,C_element027,N_element013,O_element028]
  conduct = 2
  density = 1
  expand = 3
  formula = G4_CELLULOSE_NITRATE
  name = G4_CELLULOSE_NITRATE
  specific = 4
FEATURE [App::DocumentObjectGroupPython] H_element024  label="H_element : 0.108"  # scripted group (container) (typed FeaturePython)
  n = 0.107596
FEATURE [App::DocumentObjectGroupPython] N_element014  label="N_element : 0.001"  # scripted group (container) (typed FeaturePython)
  n = 0.0008
FEATURE [App::DocumentObjectGroupPython] O_element029  label="O_element : 0.875"  # scripted group (container) (typed FeaturePython)
  n = 0.874976
FEATURE [App::DocumentObjectGroupPython] S_element008  label="S_element : 0.015"  # scripted group (container) (typed FeaturePython)
  n = 0.014627
FEATURE [App::DocumentObjectGroupPython] Ce_element001  label="Ce_element : 0.002"  # scripted group (container) (typed FeaturePython)
  n = 0.002001
FEATURE [App::DocumentObjectGroupPython] G4_CERIC_SULFATE  # scripted group (container) (typed FeaturePython)
  Dunit = g/cm3
  Dvalue = 1.03
  Group = -> [H_element024,N_element014,O_element029,S_element008,Ce_element001]
  conduct = 2
  density = 1
  expand = 3
  formula = G4_CERIC_SULFATE
  name = G4_CERIC_SULFATE
  specific = 4
FEATURE [App::DocumentObjectGroupPython] Cs_element001  label="Cs_element : 1"  # scripted group (container) (typed FeaturePython)
  n = 1
  ref = Cs_element
FEATURE [App::DocumentObjectGroupPython] F_element006  label="F_element : 1"  # scripted group (container) (typed FeaturePython)
  n = 1
  ref = F_element
FEATURE [App::DocumentObjectGroupPython] G4_CESIUM_FLUORIDE  # scripted group (container) (typed FeaturePython)
  Dunit = g/cm3
  Dvalue = 4.115
  Group = -> [Cs_element001,F_element006]
  conduct = 2
  density = 1
  expand = 3
  formula = G4_CESIUM_FLUORIDE
  name = G4_CESIUM_FLUORIDE
  specific = 4
FEATURE [App::DocumentObjectGroupPython] Cs_element002  label="Cs_element : 002"  # scripted group (container) (typed FeaturePython)
  n = 1
  ref = Cs_element
FEATURE [App::DocumentObjectGroupPython] I_element001  label="I_element : 1"  # scripted group (container) (typed FeaturePython)
  n = 1
  ref = I_element
FEATURE [App::DocumentObjectGroupPython] G4_CESIUM_IODIDE  # scripted group (container) (typed FeaturePython)
  Dunit = g/cm3
  Dvalue = 4.51
  Group = -> [Cs_element002,I_element001]
  conduct = 2
  density = 1
  expand = 3
  formula = G4_CESIUM_IODIDE
  name = G4_CESIUM_IODIDE
  specific = 4
FEATURE [App::DocumentObjectGroupPython] C_element028  label="C_element : 013"  # scripted group (container) (typed FeaturePython)
  n = 6
  ref = C_element
FEATURE [App::DocumentObjectGroupPython] H_element025  label="H_element : 013"  # scripted group (container) (typed FeaturePython)
  n = 5
  ref = H_element
FEATURE [App::DocumentObjectGroupPython] Cl_element005  label="Cl_element : 1"  # scripted group (container) (typed FeaturePython)
  n = 1
  ref = Cl_element
FEATURE [App::DocumentObjectGroupPython] G4_CHLOROBENZENE  # scripted group (container) (typed FeaturePython)
  Dunit = g/cm3
  Dvalue = 1.1058
  Group = -> [C_element028,H_element025,Cl_element005]
  conduct = 2
  density = 1
  expand = 3
  formula = G4_CHLOROBENZENE
  name = G4_CHLOROBENZENE
  specific = 4
FEATURE [App::DocumentObjectGroupPython] C_element029  label="C_element : 014"  # scripted group (container) (typed FeaturePython)
  n = 1
  ref = C_element
FEATURE [App::DocumentObjectGroupPython] H_element026  label="H_element : 1"  # scripted group (container) (typed FeaturePython)
  n = 1
  ref = H_element
FEATURE [App::DocumentObjectGroupPython] Cl_element006  label="Cl_element : 3"  # scripted group (container) (typed FeaturePython)
  n = 3
  ref = Cl_element
FEATURE [App::DocumentObjectGroupPython] G4_CHLOROFORM  # scripted group (container) (typed FeaturePython)
  Dunit = g/cm3
  Dvalue = 1.4832
  Group = -> [C_element029,H_element026,Cl_element006]
  conduct = 2
  density = 1
  expand = 3
  formula = G4_CHLOROFORM
  name = G4_CHLOROFORM
  specific = 4
FEATURE [App::DocumentObjectGroupPython] H_element027  label="H_element : 0.010"  # scripted group (container) (typed FeaturePython)
  n = 0.01
FEATURE [App::DocumentObjectGroupPython] C_element030  label="C_element : 0.001"  # scripted group (container) (typed FeaturePython)
  n = 0.001
FEATURE [App::DocumentObjectGroupPython] O_element030  label="O_element : 0.529"  # scripted group (container) (typed FeaturePython)
  n = 0.529107
FEATURE [App::DocumentObjectGroupPython] Na_element005  label="Na_element : 0.016"  # scripted group (container) (typed FeaturePython)
  n = 0.016
FEATURE [App::DocumentObjectGroupPython] Mg_element003  label="Mg_element : 0.004"  # scripted group (container) (typed FeaturePython)
  n = 0.002
FEATURE [App::DocumentObjectGroupPython] Al_element002  label="Al_element : 0.034"  # scripted group (container) (typed FeaturePython)
  n = 0.033872
FEATURE [App::DocumentObjectGroupPython] Si_element002  label="Si_element : 0.337"  # scripted group (container) (typed FeaturePython)
  n = 0.337021
FEATURE [App::DocumentObjectGroupPython] K_element003  label="K_element : 0.013"  # scripted group (container) (typed FeaturePython)
  n = 0.013
FEATURE [App::DocumentObjectGroupPython] Ca_element010  label="Ca_element : 0.044"  # scripted group (container) (typed FeaturePython)
  n = 0.044
FEATURE [App::DocumentObjectGroupPython] Fe_element002  label="Fe_element : 0.014"  # scripted group (container) (typed FeaturePython)
  n = 0.014
FEATURE [App::DocumentObjectGroupPython] G4_CONCRETE  # scripted group (container) (typed FeaturePython)
  Dunit = g/cm3
  Dvalue = 2.3
  Group = -> [H_element027,C_element030,O_element030,Na_element005,Mg_element003,Al_element002,Si_element002,K_element003,Ca_element010,Fe_element002]
  conduct = 2
  density = 1
  expand = 3
  formula = G4_CONCRETE
  name = G4_CONCRETE
  specific = 4
FEATURE [App::DocumentObjectGroupPython] C_element031  label="C_element : 015"  # scripted group (container) (typed FeaturePython)
  n = 6
  ref = C_element
FEATURE [App::DocumentObjectGroupPython] H_element028  label="H_element : 12"  # scripted group (container) (typed FeaturePython)
  n = 12
  ref = H_element
FEATURE [App::DocumentObjectGroupPython] G4_CYCLOHEXANE  # scripted group (container) (typed FeaturePython)
  Dunit = g/cm3
  Dvalue = 0.779
  Group = -> [C_element031,H_element028]
  conduct = 2
  density = 1
  expand = 3
  formula = G4_CYCLOHEXANE
  name = G4_CYCLOHEXANE
  specific = 4
FEATURE [App::DocumentObjectGroupPython] C_element032  label="C_element : 016"  # scripted group (container) (typed FeaturePython)
  n = 6
  ref = C_element
FEATURE [App::DocumentObjectGroupPython] H_element029  label="H_element : 4"  # scripted group (container) (typed FeaturePython)
  n = 4
  ref = H_element
FEATURE [App::DocumentObjectGroupPython] Cl_element007  label="Cl_element : 2"  # scripted group (container) (typed FeaturePython)
  n = 2
  ref = Cl_element
FEATURE [App::DocumentObjectGroupPython] G4_1_2_DICHLOROBENZENE  label="G4_1.2-DICHLOROBENZENE"  # scripted group (container) (typed FeaturePython)
  Dunit = g/cm3
  Dvalue = 1.3048
  Group = -> [C_element032,H_element029,Cl_element007]
  conduct = 2
  density = 1
  expand = 3
  formula = G4_1.2-DICHLOROBENZENE
  name = G4_1.2-DICHLOROBENZENE
  specific = 4
FEATURE [App::DocumentObjectGroupPython] C_element033  label="C_element : 017"  # scripted group (container) (typed FeaturePython)
  n = 4
  ref = C_element
FEATURE [App::DocumentObjectGroupPython] H_element030  label="H_element : 8"  # scripted group (container) (typed FeaturePython)
  n = 8
  ref = H_element
FEATURE [App::DocumentObjectGroupPython] O_element031  label="O_element : 014"  # scripted group (container) (typed FeaturePython)
  n = 1
  ref = O_element
FEATURE [App::DocumentObjectGroupPython] Cl_element008  label="Cl_element : 005"  # scripted group (container) (typed FeaturePython)
  n = 2
  ref = Cl_element
FEATURE [App::DocumentObjectGroupPython] G4_DICHLORODIETHYL_ETHER  # scripted group (container) (typed FeaturePython)
  Dunit = g/cm3
  Dvalue = 1.2199
  Group = -> [C_element033,H_element030,O_element031,Cl_element008]
  conduct = 2
  density = 1
  expand = 3
  formula = G4_DICHLORODIETHYL_ETHER
  name = G4_DICHLORODIETHYL_ETHER
  specific = 4
FEATURE [App::DocumentObjectGroupPython] C_element034  label="C_element : 018"  # scripted group (container) (typed FeaturePython)
  n = 2
  ref = C_element
FEATURE [App::DocumentObjectGroupPython] H_element031  label="H_element : 014"  # scripted group (container) (typed FeaturePython)
  n = 4
  ref = H_element
FEATURE [App::DocumentObjectGroupPython] Cl_element009  label="Cl_element : 006"  # scripted group (container) (typed FeaturePython)
  n = 2
  ref = Cl_element
FEATURE [App::DocumentObjectGroupPython] G4_1_2_DICHLOROETHANE  label="G4_1.2-DICHLOROETHANE"  # scripted group (container) (typed FeaturePython)
  Dunit = g/cm3
  Dvalue = 1.2351
  Group = -> [C_element034,H_element031,Cl_element009]
  conduct = 2
  density = 1
  expand = 3
  formula = G4_1.2-DICHLOROETHANE
  name = G4_1.2-DICHLOROETHANE
  specific = 4
FEATURE [App::DocumentObjectGroupPython] C_element035  label="C_element : 019"  # scripted group (container) (typed FeaturePython)
  n = 4
  ref = C_element
FEATURE [App::DocumentObjectGroupPython] H_element032  label="H_element : 015"  # scripted group (container) (typed FeaturePython)
  n = 10
  ref = H_element
FEATURE [App::DocumentObjectGroupPython] O_element032  label="O_element : 015"  # scripted group (container) (typed FeaturePython)
  n = 1
  ref = O_element
FEATURE [App::DocumentObjectGroupPython] G4_DIETHYL_ETHER  # scripted group (container) (typed FeaturePython)
  Dunit = g/cm3
  Dvalue = 0.71378
  Group = -> [C_element035,H_element032,O_element032]
  conduct = 2
  density = 1
  expand = 3
  formula = G4_DIETHYL_ETHER
  name = G4_DIETHYL_ETHER
  specific = 4
FEATURE [App::DocumentObjectGroupPython] C_element036  label="C_element : 020"  # scripted group (container) (typed FeaturePython)
  n = 3
  ref = C_element
FEATURE [App::DocumentObjectGroupPython] H_element033  label="H_element : 016"  # scripted group (container) (typed FeaturePython)
  n = 7
  ref = H_element
FEATURE [App::DocumentObjectGroupPython] N_element015  label="N_element : 008"  # scripted group (container) (typed FeaturePython)
  n = 1
  ref = N_element
FEATURE [App::DocumentObjectGroupPython] O_element033  label="O_element : 016"  # scripted group (container) (typed FeaturePython)
  n = 1
  ref = O_element
FEATURE [App::DocumentObjectGroupPython] G4_N_N_DIMETHYL_FORMAMIDE  label="G4_N.N-DIMETHYL_FORMAMIDE"  # scripted group (container) (typed FeaturePython)
  Dunit = g/cm3
  Dvalue = 0.9487
  Group = -> [C_element036,H_element033,N_element015,O_element033]
  conduct = 2
  density = 1
  expand = 3
  formula = G4_N.N-DIMETHYL_FORMAMIDE
  name = G4_N.N-DIMETHYL_FORMAMIDE
  specific = 4
FEATURE [App::DocumentObjectGroupPython] C_element037  label="C_element : 021"  # scripted group (container) (typed FeaturePython)
  n = 2
  ref = C_element
FEATURE [App::DocumentObjectGroupPython] H_element034  label="H_element : 017"  # scripted group (container) (typed FeaturePython)
  n = 6
  ref = H_element
FEATURE [App::DocumentObjectGroupPython] O_element034  label="O_element : 017"  # scripted group (container) (typed FeaturePython)
  n = 1
  ref = O_element
FEATURE [App::DocumentObjectGroupPython] S_element009  label="S_element : 003"  # scripted group (container) (typed FeaturePython)
  n = 1
  ref = S_element
FEATURE [App::DocumentObjectGroupPython] G4_DIMETHYL_SULFOXIDE  # scripted group (container) (typed FeaturePython)
  Dunit = g/cm3
  Dvalue = 1.1014
  Group = -> [C_element037,H_element034,O_element034,S_element009]
  conduct = 2
  density = 1
  expand = 3
  formula = G4_DIMETHYL_SULFOXIDE
  name = G4_DIMETHYL_SULFOXIDE
  specific = 4
FEATURE [App::DocumentObjectGroupPython] C_element038  label="C_element : 022"  # scripted group (container) (typed FeaturePython)
  n = 2
  ref = C_element
FEATURE [App::DocumentObjectGroupPython] H_element035  label="H_element : 018"  # scripted group (container) (typed FeaturePython)
  n = 6
  ref = H_element
FEATURE [App::DocumentObjectGroupPython] G4_ETHANE  # scripted group (container) (typed FeaturePython)
  Dunit = g/cm3
  Dvalue = 0.00125324
  Group = -> [C_element038,H_element035]
  conduct = 2
  density = 1
  expand = 3
  formula = G4_ETHANE
  name = G4_ETHANE
  specific = 4
FEATURE [App::DocumentObjectGroupPython] C_element039  label="C_element : 023"  # scripted group (container) (typed FeaturePython)
  n = 2
  ref = C_element
FEATURE [App::DocumentObjectGroupPython] H_element036  label="H_element : 019"  # scripted group (container) (typed FeaturePython)
  n = 6
  ref = H_element
FEATURE [App::DocumentObjectGroupPython] O_element035  label="O_element : 018"  # scripted group (container) (typed FeaturePython)
  n = 1
  ref = O_element
FEATURE [App::DocumentObjectGroupPython] G4_ETHYL_ALCOHOL  # scripted group (container) (typed FeaturePython)
  Dunit = g/cm3
  Dvalue = 0.7893
  Group = -> [C_element039,H_element036,O_element035]
  conduct = 2
  density = 1
  expand = 3
  formula = G4_ETHYL_ALCOHOL
  name = G4_ETHYL_ALCOHOL
  specific = 4
FEATURE [App::DocumentObjectGroupPython] H_element037  label="H_element : 0.090"  # scripted group (container) (typed FeaturePython)
  n = 0.090027
FEATURE [App::DocumentObjectGroupPython] C_element040  label="C_element : 0.585"  # scripted group (container) (typed FeaturePython)
  n = 0.585182
FEATURE [App::DocumentObjectGroupPython] O_element036  label="O_element : 0.325"  # scripted group (container) (typed FeaturePython)
  n = 0.324791
FEATURE [App::DocumentObjectGroupPython] G4_ETHYL_CELLULOSE  # scripted group (container) (typed FeaturePython)
  Dunit = g/cm3
  Dvalue = 1.13
  Group = -> [H_element037,C_element040,O_element036]
  conduct = 2
  density = 1
  expand = 3
  formula = G4_ETHYL_CELLULOSE
  name = G4_ETHYL_CELLULOSE
  specific = 4
FEATURE [App::DocumentObjectGroupPython] C_element041  label="C_element : 024"  # scripted group (container) (typed FeaturePython)
  n = 2
  ref = C_element
FEATURE [App::DocumentObjectGroupPython] H_element038  label="H_element : 020"  # scripted group (container) (typed FeaturePython)
  n = 4
  ref = H_element
FEATURE [App::DocumentObjectGroupPython] G4_ETHYLENE  # scripted group (container) (typed FeaturePython)
  Dunit = g/cm3
  Dvalue = 0.00117497
  Group = -> [C_element041,H_element038]
  conduct = 2
  density = 1
  expand = 3
  formula = G4_ETHYLENE
  name = G4_ETHYLENE
  specific = 4
FEATURE [App::DocumentObjectGroupPython] H_element039  label="H_element : 0.096"  # scripted group (container) (typed FeaturePython)
  n = 0.096
FEATURE [App::DocumentObjectGroupPython] C_element042  label="C_element : 0.195"  # scripted group (container) (typed FeaturePython)
  n = 0.195
FEATURE [App::DocumentObjectGroupPython] N_element016  label="N_element : 0.057"  # scripted group (container) (typed FeaturePython)
  n = 0.057
FEATURE [App::DocumentObjectGroupPython] O_element037  label="O_element : 0.646"  # scripted group (container) (typed FeaturePython)
  n = 0.646
FEATURE [App::DocumentObjectGroupPython] Na_element006  label="Na_element : 0.017"  # scripted group (container) (typed FeaturePython)
  n = 0.001
FEATURE [App::DocumentObjectGroupPython] P_element005  label="P_element : 0.104"  # scripted group (container) (typed FeaturePython)
  n = 0.001
FEATURE [App::DocumentObjectGroupPython] S_element010  label="S_element : 0.016"  # scripted group (container) (typed FeaturePython)
  n = 0.003
FEATURE [App::DocumentObjectGroupPython] Cl_element010  label="Cl_element : 0.005"  # scripted group (container) (typed FeaturePython)
  n = 0.001
FEATURE [App::DocumentObjectGroupPython] G4_EYE_LENS_ICRP  # scripted group (container) (typed FeaturePython)
  Dunit = g/cm3
  Dvalue = 1.07
  Group = -> [H_element039,C_element042,N_element016,O_element037,Na_element006,P_element005,S_element010,Cl_element010]
  conduct = 2
  density = 1
  expand = 3
  formula = G4_EYE_LENS_ICRP
  name = G4_EYE_LENS_ICRP
  specific = 4
FEATURE [App::DocumentObjectGroupPython] Fe_element003  label="Fe_element : 2"  # scripted group (container) (typed FeaturePython)
  n = 2
  ref = Fe_element
FEATURE [App::DocumentObjectGroupPython] O_element038  label="O_element : 019"  # scripted group (container) (typed FeaturePython)
  n = 3
  ref = O_element
FEATURE [App::DocumentObjectGroupPython] G4_FERRIC_OXIDE  # scripted group (container) (typed FeaturePython)
  Dunit = g/cm3
  Dvalue = 5.2
  Group = -> [Fe_element003,O_element038]
  conduct = 2
  density = 1
  expand = 3
  formula = G4_FERRIC_OXIDE
  name = G4_FERRIC_OXIDE
  specific = 4
FEATURE [App::DocumentObjectGroupPython] Fe_element004  label="Fe_element : 1"  # scripted group (container) (typed FeaturePython)
  n = 1
  ref = Fe_element
FEATURE [App::DocumentObjectGroupPython] B_element003  label="B_element : 1"  # scripted group (container) (typed FeaturePython)
  n = 1
  ref = B_element
FEATURE [App::DocumentObjectGroupPython] G4_FERROBORIDE  # scripted group (container) (typed FeaturePython)
  Dunit = g/cm3
  Dvalue = 7.15
  Group = -> [Fe_element004,B_element003]
  conduct = 2
  density = 1
  expand = 3
  formula = G4_FERROBORIDE
  name = G4_FERROBORIDE
  specific = 4
FEATURE [App::DocumentObjectGroupPython] Fe_element005  label="Fe_element : 003"  # scripted group (container) (typed FeaturePython)
  n = 1
  ref = Fe_element
FEATURE [App::DocumentObjectGroupPython] O_element039  label="O_element : 020"  # scripted group (container) (typed FeaturePython)
  n = 1
  ref = O_element
FEATURE [App::DocumentObjectGroupPython] G4_FERROUS_OXIDE  # scripted group (container) (typed FeaturePython)
  Dunit = g/cm3
  Dvalue = 5.7
  Group = -> [Fe_element005,O_element039]
  conduct = 2
  density = 1
  expand = 3
  formula = G4_FERROUS_OXIDE
  name = G4_FERROUS_OXIDE
  specific = 4
FEATURE [App::DocumentObjectGroupPython] H_element040  label="H_element : 0.115"  # scripted group (container) (typed FeaturePython)
  n = 0.108259
FEATURE [App::DocumentObjectGroupPython] N_element017  label="N_element : 0.000"  # scripted group (container) (typed FeaturePython)
  n = 2.7e-05
FEATURE [App::DocumentObjectGroupPython] O_element040  label="O_element : 0.879"  # scripted group (container) (typed FeaturePython)
  n = 0.878636
FEATURE [App::DocumentObjectGroupPython] Na_element007  label="Na_element : 0.000"  # scripted group (container) (typed FeaturePython)
  n = 2.2e-05
FEATURE [App::DocumentObjectGroupPython] S_element011  label="S_element : 0.013"  # scripted group (container) (typed FeaturePython)
  n = 0.012968
FEATURE [App::DocumentObjectGroupPython] Cl_element011  label="Cl_element : 0.000"  # scripted group (container) (typed FeaturePython)
  n = 3.4e-05
FEATURE [App::DocumentObjectGroupPython] Fe_element006  label="Fe_element : 0.000"  # scripted group (container) (typed FeaturePython)
  n = 5.4e-05
FEATURE [App::DocumentObjectGroupPython] G4_FERROUS_SULFATE  # scripted group (container) (typed FeaturePython)
  Dunit = g/cm3
  Dvalue = 1.024
  Group = -> [H_element040,N_element017,O_element040,Na_element007,S_element011,Cl_element011,Fe_element006]
  conduct = 2
  density = 1
  expand = 3
  formula = G4_FERROUS_SULFATE
  name = G4_FERROUS_SULFATE
  specific = 4
FEATURE [App::DocumentObjectGroupPython] C_element043  label="C_element : 0.099"  # scripted group (container) (typed FeaturePython)
  n = 0.099335
FEATURE [App::DocumentObjectGroupPython] F_element007  label="F_element : 0.314"  # scripted group (container) (typed FeaturePython)
  n = 0.314247
FEATURE [App::DocumentObjectGroupPython] Cl_element012  label="Cl_element : 0.586"  # scripted group (container) (typed FeaturePython)
  n = 0.586418
FEATURE [App::DocumentObjectGroupPython] G4_FREON_12  label="G4_FREON-12"  # scripted group (container) (typed FeaturePython)
  Dunit = g/cm3
  Dvalue = 1.12
  Group = -> [C_element043,F_element007,Cl_element012]
  conduct = 2
  density = 1
  expand = 3
  formula = G4_FREON-12
  name = G4_FREON-12
  specific = 4
FEATURE [App::DocumentObjectGroupPython] C_element044  label="C_element : 0.057"  # scripted group (container) (typed FeaturePython)
  n = 0.057245
FEATURE [App::DocumentObjectGroupPython] F_element008  label="F_element : 0.181"  # scripted group (container) (typed FeaturePython)
  n = 0.181096
FEATURE [App::DocumentObjectGroupPython] Br_element001  label="Br_element : 0.762"  # scripted group (container) (typed FeaturePython)
  n = 0.761659
FEATURE [App::DocumentObjectGroupPython] G4_FREON_12B2  label="G4_FREON-12B2"  # scripted group (container) (typed FeaturePython)
  Dunit = g/cm3
  Dvalue = 1.8
  Group = -> [C_element044,F_element008,Br_element001]
  conduct = 2
  density = 1
  expand = 3
  formula = G4_FREON-12B2
  name = G4_FREON-12B2
  specific = 4
FEATURE [App::DocumentObjectGroupPython] C_element045  label="C_element : 0.115"  # scripted group (container) (typed FeaturePython)
  n = 0.114983
FEATURE [App::DocumentObjectGroupPython] F_element009  label="F_element : 0.546"  # scripted group (container) (typed FeaturePython)
  n = 0.545621
FEATURE [App::DocumentObjectGroupPython] Cl_element013  label="Cl_element : 0.339"  # scripted group (container) (typed FeaturePython)
  n = 0.339396
FEATURE [App::DocumentObjectGroupPython] G4_FREON_13  label="G4_FREON-13"  # scripted group (container) (typed FeaturePython)
  Dunit = g/cm3
  Dvalue = 0.95
  Group = -> [C_element045,F_element009,Cl_element013]
  conduct = 2
  density = 1
  expand = 3
  formula = G4_FREON-13
  name = G4_FREON-13
  specific = 4
FEATURE [App::DocumentObjectGroupPython] C_element046  label="C_element : 025"  # scripted group (container) (typed FeaturePython)
  n = 1
  ref = C_element
FEATURE [App::DocumentObjectGroupPython] F_element010  label="F_element : 3"  # scripted group (container) (typed FeaturePython)
  n = 3
  ref = F_element
FEATURE [App::DocumentObjectGroupPython] Br_element002  label="Br_element : 1"  # scripted group (container) (typed FeaturePython)
  n = 1
  ref = Br_element
FEATURE [App::DocumentObjectGroupPython] G4_FREON_13B1  label="G4_FREON-13B1"  # scripted group (container) (typed FeaturePython)
  Dunit = g/cm3
  Dvalue = 1.5
  Group = -> [C_element046,F_element010,Br_element002]
  conduct = 2
  density = 1
  expand = 3
  formula = G4_FREON-13B1
  name = G4_FREON-13B1
  specific = 4
FEATURE [App::DocumentObjectGroupPython] C_element047  label="C_element : 0.061"  # scripted group (container) (typed FeaturePython)
  n = 0.061309
FEATURE [App::DocumentObjectGroupPython] F_element011  label="F_element : 0.291"  # scripted group (container) (typed FeaturePython)
  n = 0.290924
FEATURE [App::DocumentObjectGroupPython] I_element002  label="I_element : 0.648"  # scripted group (container) (typed FeaturePython)
  n = 0.647767
FEATURE [App::DocumentObjectGroupPython] G4_FREON_13I1  label="G4_FREON-13I1"  # scripted group (container) (typed FeaturePython)
  Dunit = g/cm3
  Dvalue = 1.8
  Group = -> [C_element047,F_element011,I_element002]
  conduct = 2
  density = 1
  expand = 3
  formula = G4_FREON-13I1
  name = G4_FREON-13I1
  specific = 4
FEATURE [App::DocumentObjectGroupPython] Gd_element001  label="Gd_element : 2"  # scripted group (container) (typed FeaturePython)
  n = 2
  ref = Gd_element
FEATURE [App::DocumentObjectGroupPython] O_element041  label="O_element : 021"  # scripted group (container) (typed FeaturePython)
  n = 2
  ref = O_element
FEATURE [App::DocumentObjectGroupPython] S_element012  label="S_element : 004"  # scripted group (container) (typed FeaturePython)
  n = 1
  ref = S_element
FEATURE [App::DocumentObjectGroupPython] G4_GADOLINIUM_OXYSULFIDE  # scripted group (container) (typed FeaturePython)
  Dunit = g/cm3
  Dvalue = 7.44
  Group = -> [Gd_element001,O_element041,S_element012]
  conduct = 2
  density = 1
  expand = 3
  formula = G4_GADOLINIUM_OXYSULFIDE
  name = G4_GADOLINIUM_OXYSULFIDE
  specific = 4
FEATURE [App::DocumentObjectGroupPython] Ga_element001  label="Ga_element : 1"  # scripted group (container) (typed FeaturePython)
  n = 1
  ref = Ga_element
FEATURE [App::DocumentObjectGroupPython] As_element001  label="As_element : 1"  # scripted group (container) (typed FeaturePython)
  n = 1
  ref = As_element
FEATURE [App::DocumentObjectGroupPython] G4_GALLIUM_ARSENIDE  # scripted group (container) (typed FeaturePython)
  Dunit = g/cm3
  Dvalue = 5.31
  Group = -> [Ga_element001,As_element001]
  conduct = 2
  density = 1
  expand = 3
  formula = G4_GALLIUM_ARSENIDE
  name = G4_GALLIUM_ARSENIDE
  specific = 4
FEATURE [App::DocumentObjectGroupPython] H_element041  label="H_element : 0.081"  # scripted group (container) (typed FeaturePython)
  n = 0.08118
FEATURE [App::DocumentObjectGroupPython] C_element048  label="C_element : 0.416"  # scripted group (container) (typed FeaturePython)
  n = 0.41606
FEATURE [App::DocumentObjectGroupPython] N_element018  label="N_element : 0.111"  # scripted group (container) (typed FeaturePython)
  n = 0.11124
FEATURE [App::DocumentObjectGroupPython] O_element042  label="O_element : 0.381"  # scripted group (container) (typed FeaturePython)
  n = 0.38064
FEATURE [App::DocumentObjectGroupPython] S_element013  label="S_element : 0.011"  # scripted group (container) (typed FeaturePython)
  n = 0.01088
FEATURE [App::DocumentObjectGroupPython] G4_GEL_PHOTO_EMULSION  # scripted group (container) (typed FeaturePython)
  Dunit = g/cm3
  Dvalue = 1.2914
  Group = -> [H_element041,C_element048,N_element018,O_element042,S_element013]
  conduct = 2
  density = 1
  expand = 3
  formula = G4_GEL_PHOTO_EMULSION
  name = G4_GEL_PHOTO_EMULSION
  specific = 4
FEATURE [App::DocumentObjectGroupPython] B_element004  label="B_element : 0.040"  # scripted group (container) (typed FeaturePython)
  n = 0.0400639
FEATURE [App::DocumentObjectGroupPython] O_element043  label="O_element : 0.540"  # scripted group (container) (typed FeaturePython)
  n = 0.539561
FEATURE [App::DocumentObjectGroupPython] Na_element008  label="Na_element : 0.028"  # scripted group (container) (typed FeaturePython)
  n = 0.0281909
FEATURE [App::DocumentObjectGroupPython] Al_element003  label="Al_element : 0.012"  # scripted group (container) (typed FeaturePython)
  n = 0.011644
FEATURE [App::DocumentObjectGroupPython] Si_element003  label="Si_element : 0.377"  # scripted group (container) (typed FeaturePython)
  n = 0.377219
FEATURE [App::DocumentObjectGroupPython] K_element004  label="K_element : 0.014"  # scripted group (container) (typed FeaturePython)
  n = 0.00332099
FEATURE [App::DocumentObjectGroupPython] G4_Pyrex_Glass  # scripted group (container) (typed FeaturePython)
  Dunit = g/cm3
  Dvalue = 2.23
  Group = -> [B_element004,O_element043,Na_element008,Al_element003,Si_element003,K_element004]
  conduct = 2
  density = 1
  expand = 3
  formula = G4_Pyrex_Glass
  name = G4_Pyrex_Glass
  specific = 4
FEATURE [App::DocumentObjectGroupPython] O_element044  label="O_element : 0.156"  # scripted group (container) (typed FeaturePython)
  n = 0.156453
FEATURE [App::DocumentObjectGroupPython] Si_element004  label="Si_element : 0.081"  # scripted group (container) (typed FeaturePython)
  n = 0.080866
FEATURE [App::DocumentObjectGroupPython] Ti_element001  label="Ti_element : 0.008"  # scripted group (container) (typed FeaturePython)
  n = 0.008092
FEATURE [App::DocumentObjectGroupPython] As_element002  label="As_element : 0.003"  # scripted group (container) (typed FeaturePython)
  n = 0.002651
FEATURE [App::DocumentObjectGroupPython] Pb_element001  label="Pb_element : 0.752"  # scripted group (container) (typed FeaturePython)
  n = 0.751938
FEATURE [App::DocumentObjectGroupPython] G4_GLASS_LEAD  # scripted group (container) (typed FeaturePython)
  Dunit = g/cm3
  Dvalue = 6.22
  Group = -> [O_element044,Si_element004,Ti_element001,As_element002,Pb_element001]
  conduct = 2
  density = 1
  expand = 3
  formula = G4_GLASS_LEAD
  name = G4_GLASS_LEAD
  specific = 4
FEATURE [App::DocumentObjectGroupPython] O_element045  label="O_element : 0.460"  # scripted group (container) (typed FeaturePython)
  n = 0.4598
FEATURE [App::DocumentObjectGroupPython] Na_element009  label="Na_element : 0.096"  # scripted group (container) (typed FeaturePython)
  n = 0.0964411
FEATURE [App::DocumentObjectGroupPython] Si_element005  label="Si_element : 0.378"  # scripted group (container) (typed FeaturePython)
  n = 0.336553
FEATURE [App::DocumentObjectGroupPython] Ca_element011  label="Ca_element : 0.107"  # scripted group (container) (typed FeaturePython)
  n = 0.107205
FEATURE [App::DocumentObjectGroupPython] G4_GLASS_PLATE  # scripted group (container) (typed FeaturePython)
  Dunit = g/cm3
  Dvalue = 2.4
  Group = -> [O_element045,Na_element009,Si_element005,Ca_element011]
  conduct = 2
  density = 1
  expand = 3
  formula = G4_GLASS_PLATE
  name = G4_GLASS_PLATE
  specific = 4
FEATURE [App::DocumentObjectGroupPython] C_element049  label="C_element : 026"  # scripted group (container) (typed FeaturePython)
  n = 5
  ref = C_element
FEATURE [App::DocumentObjectGroupPython] H_element042  label="H_element : 021"  # scripted group (container) (typed FeaturePython)
  n = 10
  ref = H_element
FEATURE [App::DocumentObjectGroupPython] N_element019  label="N_element : 2"  # scripted group (container) (typed FeaturePython)
  n = 2
  ref = N_element
FEATURE [App::DocumentObjectGroupPython] O_element046  label="O_element : 022"  # scripted group (container) (typed FeaturePython)
  n = 3
  ref = O_element
FEATURE [App::DocumentObjectGroupPython] G4_GLUTAMINE  # scripted group (container) (typed FeaturePython)
  Dunit = g/cm3
  Dvalue = 1.46
  Group = -> [C_element049,H_element042,N_element019,O_element046]
  conduct = 2
  density = 1
  expand = 3
  formula = G4_GLUTAMINE
  name = G4_GLUTAMINE
  specific = 4
FEATURE [App::DocumentObjectGroupPython] C_element050  label="C_element : 027"  # scripted group (container) (typed FeaturePython)
  n = 3
  ref = C_element
FEATURE [App::DocumentObjectGroupPython] H_element043  label="H_element : 022"  # scripted group (container) (typed FeaturePython)
  n = 8
  ref = H_element
FEATURE [App::DocumentObjectGroupPython] O_element047  label="O_element : 023"  # scripted group (container) (typed FeaturePython)
  n = 3
  ref = O_element
FEATURE [App::DocumentObjectGroupPython] G4_GLYCEROL  # scripted group (container) (typed FeaturePython)
  Dunit = g/cm3
  Dvalue = 1.2613
  Group = -> [C_element050,H_element043,O_element047]
  conduct = 2
  density = 1
  expand = 3
  formula = G4_GLYCEROL
  name = G4_GLYCEROL
  specific = 4
FEATURE [App::DocumentObjectGroupPython] C_element051  label="C_element : 028"  # scripted group (container) (typed FeaturePython)
  n = 5
  ref = C_element
FEATURE [App::DocumentObjectGroupPython] H_element044  label="H_element : 023"  # scripted group (container) (typed FeaturePython)
  n = 5
  ref = H_element
FEATURE [App::DocumentObjectGroupPython] N_element020  label="N_element : 009"  # scripted group (container) (typed FeaturePython)
  n = 5
  ref = N_element
FEATURE [App::DocumentObjectGroupPython] O_element048  label="O_element : 024"  # scripted group (container) (typed FeaturePython)
  n = 1
  ref = O_element
FEATURE [App::DocumentObjectGroupPython] G4_GUANINE  # scripted group (container) (typed FeaturePython)
  Dunit = g/cm3
  Dvalue = 2.2
  Group = -> [C_element051,H_element044,N_element020,O_element048]
  conduct = 2
  density = 1
  expand = 3
  formula = G4_GUANINE
  name = G4_GUANINE
  specific = 4
FEATURE [App::DocumentObjectGroupPython] Ca_element012  label="Ca_element : 006"  # scripted group (container) (typed FeaturePython)
  n = 1
  ref = Ca_element
FEATURE [App::DocumentObjectGroupPython] S_element014  label="S_element : 005"  # scripted group (container) (typed FeaturePython)
  n = 1
  ref = S_element
FEATURE [App::DocumentObjectGroupPython] O_element049  label="O_element : 6"  # scripted group (container) (typed FeaturePython)
  n = 6
  ref = O_element
FEATURE [App::DocumentObjectGroupPython] H_element045  label="H_element : 024"  # scripted group (container) (typed FeaturePython)
  n = 4
  ref = H_element
FEATURE [App::DocumentObjectGroupPython] G4_GYPSUM  # scripted group (container) (typed FeaturePython)
  Dunit = g/cm3
  Dvalue = 2.32
  Group = -> [Ca_element012,S_element014,O_element049,H_element045]
  conduct = 2
  density = 1
  expand = 3
  formula = G4_GYPSUM
  name = G4_GYPSUM
  specific = 4
FEATURE [App::DocumentObjectGroupPython] C_element052  label="C_element : 7"  # scripted group (container) (typed FeaturePython)
  n = 7
  ref = C_element
FEATURE [App::DocumentObjectGroupPython] H_element046  label="H_element : 16"  # scripted group (container) (typed FeaturePython)
  n = 16
  ref = H_element
FEATURE [App::DocumentObjectGroupPython] G4_N_HEPTANE  label="G4_N-HEPTANE"  # scripted group (container) (typed FeaturePython)
  Dunit = g/cm3
  Dvalue = 0.68376
  Group = -> [C_element052,H_element046]
  conduct = 2
  density = 1
  expand = 3
  formula = G4_N-HEPTANE
  name = G4_N-HEPTANE
  specific = 4
FEATURE [App::DocumentObjectGroupPython] C_element053  label="C_element : 029"  # scripted group (container) (typed FeaturePython)
  n = 6
  ref = C_element
FEATURE [App::DocumentObjectGroupPython] H_element047  label="H_element : 14"  # scripted group (container) (typed FeaturePython)
  n = 14
  ref = H_element
FEATURE [App::DocumentObjectGroupPython] G4_N_HEXANE  label="G4_N-HEXANE"  # scripted group (container) (typed FeaturePython)
  Dunit = g/cm3
  Dvalue = 0.6603
  Group = -> [C_element053,H_element047]
  conduct = 2
  density = 1
  expand = 3
  formula = G4_N-HEXANE
  name = G4_N-HEXANE
  specific = 4
FEATURE [App::DocumentObjectGroupPython] C_element054  label="C_element : 22"  # scripted group (container) (typed FeaturePython)
  n = 22
  ref = C_element
FEATURE [App::DocumentObjectGroupPython] H_element048  label="H_element : 025"  # scripted group (container) (typed FeaturePython)
  n = 10
  ref = H_element
FEATURE [App::DocumentObjectGroupPython] N_element021  label="N_element : 010"  # scripted group (container) (typed FeaturePython)
  n = 2
  ref = N_element
FEATURE [App::DocumentObjectGroupPython] O_element050  label="O_element : 025"  # scripted group (container) (typed FeaturePython)
  n = 5
  ref = O_element
FEATURE [App::DocumentObjectGroupPython] G4_KAPTON  # scripted group (container) (typed FeaturePython)
  Dunit = g/cm3
  Dvalue = 1.42
  Group = -> [C_element054,H_element048,N_element021,O_element050]
  conduct = 2
  density = 1
  expand = 3
  formula = G4_KAPTON
  name = G4_KAPTON
  specific = 4
FEATURE [App::DocumentObjectGroupPython] La_element001  label="La_element : 1"  # scripted group (container) (typed FeaturePython)
  n = 1
  ref = La_element
FEATURE [App::DocumentObjectGroupPython] Br_element003  label="Br_element : 002"  # scripted group (container) (typed FeaturePython)
  n = 1
  ref = Br_element
FEATURE [App::DocumentObjectGroupPython] O_element051  label="O_element : 026"  # scripted group (container) (typed FeaturePython)
  n = 1
  ref = O_element
FEATURE [App::DocumentObjectGroupPython] G4_LANTHANUM_OXYBROMIDE  # scripted group (container) (typed FeaturePython)
  Dunit = g/cm3
  Dvalue = 6.28
  Group = -> [La_element001,Br_element003,O_element051]
  conduct = 2
  density = 1
  expand = 3
  formula = G4_LANTHANUM_OXYBROMIDE
  name = G4_LANTHANUM_OXYBROMIDE
  specific = 4
FEATURE [App::DocumentObjectGroupPython] La_element002  label="La_element : 2"  # scripted group (container) (typed FeaturePython)
  n = 2
  ref = La_element
FEATURE [App::DocumentObjectGroupPython] O_element052  label="O_element : 027"  # scripted group (container) (typed FeaturePython)
  n = 2
  ref = O_element
FEATURE [App::DocumentObjectGroupPython] S_element015  label="S_element : 006"  # scripted group (container) (typed FeaturePython)
  n = 1
  ref = S_element
FEATURE [App::DocumentObjectGroupPython] G4_LANTHANUM_OXYSULFIDE  # scripted group (container) (typed FeaturePython)
  Dunit = g/cm3
  Dvalue = 5.86
  Group = -> [La_element002,O_element052,S_element015]
  conduct = 2
  density = 1
  expand = 3
  formula = G4_LANTHANUM_OXYSULFIDE
  name = G4_LANTHANUM_OXYSULFIDE
  specific = 4
FEATURE [App::DocumentObjectGroupPython] O_element053  label="O_element : 0.072"  # scripted group (container) (typed FeaturePython)
  n = 0.071682
FEATURE [App::DocumentObjectGroupPython] Pb_element002  label="Pb_element : 0.928"  # scripted group (container) (typed FeaturePython)
  n = 0.928318
FEATURE [App::DocumentObjectGroupPython] G4_LEAD_OXIDE  # scripted group (container) (typed FeaturePython)
  Dunit = g/cm3
  Dvalue = 9.53
  Group = -> [O_element053,Pb_element002]
  conduct = 2
  density = 1
  expand = 3
  formula = G4_LEAD_OXIDE
  name = G4_LEAD_OXIDE
  specific = 4
FEATURE [App::DocumentObjectGroupPython] Li_element001  label="Li_element : 1"  # scripted group (container) (typed FeaturePython)
  n = 1
  ref = Li_element
FEATURE [App::DocumentObjectGroupPython] N_element022  label="N_element : 011"  # scripted group (container) (typed FeaturePython)
  n = 1
  ref = N_element
FEATURE [App::DocumentObjectGroupPython] H_element049  label="H_element : 026"  # scripted group (container) (typed FeaturePython)
  n = 2
  ref = H_element
FEATURE [App::DocumentObjectGroupPython] G4_LITHIUM_AMIDE  # scripted group (container) (typed FeaturePython)
  Dunit = g/cm3
  Dvalue = 1.178
  Group = -> [Li_element001,N_element022,H_element049]
  conduct = 2
  density = 1
  expand = 3
  formula = G4_LITHIUM_AMIDE
  name = G4_LITHIUM_AMIDE
  specific = 4
FEATURE [App::DocumentObjectGroupPython] Li_element002  label="Li_element : 2"  # scripted group (container) (typed FeaturePython)
  n = 2
  ref = Li_element
FEATURE [App::DocumentObjectGroupPython] C_element055  label="C_element : 030"  # scripted group (container) (typed FeaturePython)
  n = 1
  ref = C_element
FEATURE [App::DocumentObjectGroupPython] O_element054  label="O_element : 028"  # scripted group (container) (typed FeaturePython)
  n = 3
  ref = O_element
FEATURE [App::DocumentObjectGroupPython] G4_LITHIUM_CARBONATE  # scripted group (container) (typed FeaturePython)
  Dunit = g/cm3
  Dvalue = 2.11
  Group = -> [Li_element002,C_element055,O_element054]
  conduct = 2
  density = 1
  expand = 3
  formula = G4_LITHIUM_CARBONATE
  name = G4_LITHIUM_CARBONATE
  specific = 4
FEATURE [App::DocumentObjectGroupPython] Li_element003  label="Li_element : 003"  # scripted group (container) (typed FeaturePython)
  n = 1
  ref = Li_element
FEATURE [App::DocumentObjectGroupPython] F_element012  label="F_element : 004"  # scripted group (container) (typed FeaturePython)
  n = 1
  ref = F_element
FEATURE [App::DocumentObjectGroupPython] G4_LITHIUM_FLUORIDE  # scripted group (container) (typed FeaturePython)
  Dunit = g/cm3
  Dvalue = 2.635
  Group = -> [Li_element003,F_element012]
  conduct = 2
  density = 1
  expand = 3
  formula = G4_LITHIUM_FLUORIDE
  name = G4_LITHIUM_FLUORIDE
  specific = 4
FEATURE [App::DocumentObjectGroupPython] Li_element004  label="Li_element : 004"  # scripted group (container) (typed FeaturePython)
  n = 1
  ref = Li_element
FEATURE [App::DocumentObjectGroupPython] H_element050  label="H_element : 027"  # scripted group (container) (typed FeaturePython)
  n = 1
  ref = H_element
FEATURE [App::DocumentObjectGroupPython] G4_LITHIUM_HYDRIDE  # scripted group (container) (typed FeaturePython)
  Dunit = g/cm3
  Dvalue = 0.82
  Group = -> [Li_element004,H_element050]
  conduct = 2
  density = 1
  expand = 3
  formula = G4_LITHIUM_HYDRIDE
  name = G4_LITHIUM_HYDRIDE
  specific = 4
FEATURE [App::DocumentObjectGroupPython] Li_element005  label="Li_element : 005"  # scripted group (container) (typed FeaturePython)
  n = 1
  ref = Li_element
FEATURE [App::DocumentObjectGroupPython] I_element003  label="I_element : 002"  # scripted group (container) (typed FeaturePython)
  n = 1
  ref = I_element
FEATURE [App::DocumentObjectGroupPython] G4_LITHIUM_IODIDE  # scripted group (container) (typed FeaturePython)
  Dunit = g/cm3
  Dvalue = 3.494
  Group = -> [Li_element005,I_element003]
  conduct = 2
  density = 1
  expand = 3
  formula = G4_LITHIUM_IODIDE
  name = G4_LITHIUM_IODIDE
  specific = 4
FEATURE [App::DocumentObjectGroupPython] Li_element006  label="Li_element : 006"  # scripted group (container) (typed FeaturePython)
  n = 2
  ref = Li_element
FEATURE [App::DocumentObjectGroupPython] O_element055  label="O_element : 029"  # scripted group (container) (typed FeaturePython)
  n = 1
  ref = O_element
FEATURE [App::DocumentObjectGroupPython] G4_LITHIUM_OXIDE  # scripted group (container) (typed FeaturePython)
  Dunit = g/cm3
  Dvalue = 2.013
  Group = -> [Li_element006,O_element055]
  conduct = 2
  density = 1
  expand = 3
  formula = G4_LITHIUM_OXIDE
  name = G4_LITHIUM_OXIDE
  specific = 4
FEATURE [App::DocumentObjectGroupPython] Li_element007  label="Li_element : 007"  # scripted group (container) (typed FeaturePython)
  n = 2
  ref = Li_element
FEATURE [App::DocumentObjectGroupPython] B_element005  label="B_element : 005"  # scripted group (container) (typed FeaturePython)
  n = 4
  ref = B_element
FEATURE [App::DocumentObjectGroupPython] O_element056  label="O_element : 7"  # scripted group (container) (typed FeaturePython)
  n = 7
  ref = O_element
FEATURE [App::DocumentObjectGroupPython] G4_LITHIUM_TETRABORATE  # scripted group (container) (typed FeaturePython)
  Dunit = g/cm3
  Dvalue = 2.44
  Group = -> [Li_element007,B_element005,O_element056]
  conduct = 2
  density = 1
  expand = 3
  formula = G4_LITHIUM_TETRABORATE
  name = G4_LITHIUM_TETRABORATE
  specific = 4
FEATURE [App::DocumentObjectGroupPython] H_element051  label="H_element : 0.105"  # scripted group (container) (typed FeaturePython)
  n = 0.105
FEATURE [App::DocumentObjectGroupPython] C_element056  label="C_element : 0.083"  # scripted group (container) (typed FeaturePython)
  n = 0.083
FEATURE [App::DocumentObjectGroupPython] N_element023  label="N_element : 0.023"  # scripted group (container) (typed FeaturePython)
  n = 0.023
FEATURE [App::DocumentObjectGroupPython] O_element057  label="O_element : 0.779"  # scripted group (container) (typed FeaturePython)
  n = 0.779
FEATURE [App::DocumentObjectGroupPython] Na_element010  label="Na_element : 0.097"  # scripted group (container) (typed FeaturePython)
  n = 0.002
FEATURE [App::DocumentObjectGroupPython] P_element006  label="P_element : 0.105"  # scripted group (container) (typed FeaturePython)
  n = 0.001
FEATURE [App::DocumentObjectGroupPython] S_element016  label="S_element : 0.017"  # scripted group (container) (typed FeaturePython)
  n = 0.002
FEATURE [App::DocumentObjectGroupPython] Cl_element014  label="Cl_element : 0.587"  # scripted group (container) (typed FeaturePython)
  n = 0.003
FEATURE [App::DocumentObjectGroupPython] K_element005  label="K_element : 0.015"  # scripted group (container) (typed FeaturePython)
  n = 0.002
FEATURE [App::DocumentObjectGroupPython] G4_LUNG_ICRP  # scripted group (container) (typed FeaturePython)
  Dunit = g/cm3
  Dvalue = 1.04
  Group = -> [H_element051,C_element056,N_element023,O_element057,Na_element010,P_element006,S_element016,Cl_element014,K_element005]
  conduct = 2
  density = 1
  expand = 3
  formula = G4_LUNG_ICRP
  name = G4_LUNG_ICRP
  specific = 4
FEATURE [App::DocumentObjectGroupPython] H_element052  label="H_element : 0.116"  # scripted group (container) (typed FeaturePython)
  n = 0.114318
FEATURE [App::DocumentObjectGroupPython] C_element057  label="C_element : 0.656"  # scripted group (container) (typed FeaturePython)
  n = 0.655824
FEATURE [App::DocumentObjectGroupPython] O_element058  label="O_element : 0.092"  # scripted group (container) (typed FeaturePython)
  n = 0.0921831
FEATURE [App::DocumentObjectGroupPython] Mg_element004  label="Mg_element : 0.135"  # scripted group (container) (typed FeaturePython)
  n = 0.134792
FEATURE [App::DocumentObjectGroupPython] Ca_element013  label="Ca_element : 0.003"  # scripted group (container) (typed FeaturePython)
  n = 0.002883
FEATURE [App::DocumentObjectGroupPython] G4_M3_WAX  # scripted group (container) (typed FeaturePython)
  Dunit = g/cm3
  Dvalue = 1.05
  Group = -> [H_element052,C_element057,O_element058,Mg_element004,Ca_element013]
  conduct = 2
  density = 1
  expand = 3
  formula = G4_M3_WAX
  name = G4_M3_WAX
  specific = 4
FEATURE [App::DocumentObjectGroupPython] Mg_element005  label="Mg_element : 1"  # scripted group (container) (typed FeaturePython)
  n = 1
  ref = Mg_element
FEATURE [App::DocumentObjectGroupPython] C_element058  label="C_element : 031"  # scripted group (container) (typed FeaturePython)
  n = 1
  ref = C_element
FEATURE [App::DocumentObjectGroupPython] O_element059  label="O_element : 030"  # scripted group (container) (typed FeaturePython)
  n = 3
  ref = O_element
FEATURE [App::DocumentObjectGroupPython] G4_MAGNESIUM_CARBONATE  # scripted group (container) (typed FeaturePython)
  Dunit = g/cm3
  Dvalue = 2.958
  Group = -> [Mg_element005,C_element058,O_element059]
  conduct = 2
  density = 1
  expand = 3
  formula = G4_MAGNESIUM_CARBONATE
  name = G4_MAGNESIUM_CARBONATE
  specific = 4
FEATURE [App::DocumentObjectGroupPython] Mg_element006  label="Mg_element : 002"  # scripted group (container) (typed FeaturePython)
  n = 1
  ref = Mg_element
FEATURE [App::DocumentObjectGroupPython] F_element013  label="F_element : 005"  # scripted group (container) (typed FeaturePython)
  n = 2
  ref = F_element
FEATURE [App::DocumentObjectGroupPython] G4_MAGNESIUM_FLUORIDE  # scripted group (container) (typed FeaturePython)
  Dunit = g/cm3
  Dvalue = 3
  Group = -> [Mg_element006,F_element013]
  conduct = 2
  density = 1
  expand = 3
  formula = G4_MAGNESIUM_FLUORIDE
  name = G4_MAGNESIUM_FLUORIDE
  specific = 4
FEATURE [App::DocumentObjectGroupPython] Mg_element007  label="Mg_element : 003"  # scripted group (container) (typed FeaturePython)
  n = 1
  ref = Mg_element
FEATURE [App::DocumentObjectGroupPython] O_element060  label="O_element : 031"  # scripted group (container) (typed FeaturePython)
  n = 1
  ref = O_element
FEATURE [App::DocumentObjectGroupPython] G4_MAGNESIUM_OXIDE  # scripted group (container) (typed FeaturePython)
  Dunit = g/cm3
  Dvalue = 3.58
  Group = -> [Mg_element007,O_element060]
  conduct = 2
  density = 1
  expand = 3
  formula = G4_MAGNESIUM_OXIDE
  name = G4_MAGNESIUM_OXIDE
  specific = 4
FEATURE [App::DocumentObjectGroupPython] Mg_element008  label="Mg_element : 004"  # scripted group (container) (typed FeaturePython)
  n = 1
  ref = Mg_element
FEATURE [App::DocumentObjectGroupPython] B_element006  label="B_element : 006"  # scripted group (container) (typed FeaturePython)
  n = 4
  ref = B_element
FEATURE [App::DocumentObjectGroupPython] O_element061  label="O_element : 032"  # scripted group (container) (typed FeaturePython)
  n = 7
  ref = O_element
FEATURE [App::DocumentObjectGroupPython] G4_MAGNESIUM_TETRABORATE  # scripted group (container) (typed FeaturePython)
  Dunit = g/cm3
  Dvalue = 2.53
  Group = -> [Mg_element008,B_element006,O_element061]
  conduct = 2
  density = 1
  expand = 3
  formula = G4_MAGNESIUM_TETRABORATE
  name = G4_MAGNESIUM_TETRABORATE
  specific = 4
FEATURE [App::DocumentObjectGroupPython] Hg_element001  label="Hg_element : 1"  # scripted group (container) (typed FeaturePython)
  n = 1
  ref = Hg_element
FEATURE [App::DocumentObjectGroupPython] I_element004  label="I_element : 2"  # scripted group (container) (typed FeaturePython)
  n = 2
  ref = I_element
FEATURE [App::DocumentObjectGroupPython] G4_MERCURIC_IODIDE  # scripted group (container) (typed FeaturePython)
  Dunit = g/cm3
  Dvalue = 6.36
  Group = -> [Hg_element001,I_element004]
  conduct = 2
  density = 1
  expand = 3
  formula = G4_MERCURIC_IODIDE
  name = G4_MERCURIC_IODIDE
  specific = 4
FEATURE [App::DocumentObjectGroupPython] C_element059  label="C_element : 032"  # scripted group (container) (typed FeaturePython)
  n = 1
  ref = C_element
FEATURE [App::DocumentObjectGroupPython] H_element053  label="H_element : 028"  # scripted group (container) (typed FeaturePython)
  n = 4
  ref = H_element
FEATURE [App::DocumentObjectGroupPython] G4_METHANE  # scripted group (container) (typed FeaturePython)
  Dunit = g/cm3
  Dvalue = 0.000667151
  Group = -> [C_element059,H_element053]
  conduct = 2
  density = 1
  expand = 3
  formula = G4_METHANE
  name = G4_METHANE
  specific = 4
FEATURE [App::DocumentObjectGroupPython] C_element060  label="C_element : 033"  # scripted group (container) (typed FeaturePython)
  n = 1
  ref = C_element
FEATURE [App::DocumentObjectGroupPython] H_element054  label="H_element : 029"  # scripted group (container) (typed FeaturePython)
  n = 4
  ref = H_element
FEATURE [App::DocumentObjectGroupPython] O_element062  label="O_element : 033"  # scripted group (container) (typed FeaturePython)
  n = 1
  ref = O_element
FEATURE [App::DocumentObjectGroupPython] G4_METHANOL  # scripted group (container) (typed FeaturePython)
  Dunit = g/cm3
  Dvalue = 0.7914
  Group = -> [C_element060,H_element054,O_element062]
  conduct = 2
  density = 1
  expand = 3
  formula = G4_METHANOL
  name = G4_METHANOL
  specific = 4
FEATURE [App::DocumentObjectGroupPython] H_element055  label="H_element : 0.134"  # scripted group (container) (typed FeaturePython)
  n = 0.13404
FEATURE [App::DocumentObjectGroupPython] C_element061  label="C_element : 0.778"  # scripted group (container) (typed FeaturePython)
  n = 0.77796
FEATURE [App::DocumentObjectGroupPython] O_element063  label="O_element : 0.035"  # scripted group (container) (typed FeaturePython)
  n = 0.03502
FEATURE [App::DocumentObjectGroupPython] Mg_element009  label="Mg_element : 0.039"  # scripted group (container) (typed FeaturePython)
  n = 0.038594
FEATURE [App::DocumentObjectGroupPython] Ti_element002  label="Ti_element : 0.014"  # scripted group (container) (typed FeaturePython)
  n = 0.014386
FEATURE [App::DocumentObjectGroupPython] G4_MIX_D_WAX  # scripted group (container) (typed FeaturePython)
  Dunit = g/cm3
  Dvalue = 0.99
  Group = -> [H_element055,C_element061,O_element063,Mg_element009,Ti_element002]
  conduct = 2
  density = 1
  expand = 3
  formula = G4_MIX_D_WAX
  name = G4_MIX_D_WAX
  specific = 4
FEATURE [App::DocumentObjectGroupPython] H_element056  label="H_element : 0.135"  # scripted group (container) (typed FeaturePython)
  n = 0.081192
FEATURE [App::DocumentObjectGroupPython] C_element062  label="C_element : 0.583"  # scripted group (container) (typed FeaturePython)
  n = 0.583442
FEATURE [App::DocumentObjectGroupPython] N_element024  label="N_element : 0.018"  # scripted group (container) (typed FeaturePython)
  n = 0.017798
FEATURE [App::DocumentObjectGroupPython] O_element064  label="O_element : 0.186"  # scripted group (container) (typed FeaturePython)
  n = 0.186381
FEATURE [App::DocumentObjectGroupPython] Mg_element010  label="Mg_element : 0.130"  # scripted group (container) (typed FeaturePython)
  n = 0.130287
FEATURE [App::DocumentObjectGroupPython] Cl_element015  label="Cl_element : 0.588"  # scripted group (container) (typed FeaturePython)
  n = 0.0009
FEATURE [App::DocumentObjectGroupPython] G4_MS20_TISSUE  # scripted group (container) (typed FeaturePython)
  Dunit = g/cm3
  Dvalue = 1
  Group = -> [H_element056,C_element062,N_element024,O_element064,Mg_element010,Cl_element015]
  conduct = 2
  density = 1
  expand = 3
  formula = G4_MS20_TISSUE
  name = G4_MS20_TISSUE
  specific = 4
FEATURE [App::DocumentObjectGroupPython] H_element057  label="H_element : 0.136"  # scripted group (container) (typed FeaturePython)
  n = 0.102
FEATURE [App::DocumentObjectGroupPython] C_element063  label="C_element : 0.143"  # scripted group (container) (typed FeaturePython)
  n = 0.143
FEATURE [App::DocumentObjectGroupPython] N_element025  label="N_element : 0.034"  # scripted group (container) (typed FeaturePython)
  n = 0.034
FEATURE [App::DocumentObjectGroupPython] O_element065  label="O_element : 0.710"  # scripted group (container) (typed FeaturePython)
  n = 0.71
FEATURE [App::DocumentObjectGroupPython] Na_element011  label="Na_element : 0.098"  # scripted group (container) (typed FeaturePython)
  n = 0.001
FEATURE [App::DocumentObjectGroupPython] P_element007  label="P_element : 0.002"  # scripted group (container) (typed FeaturePython)
  n = 0.002
FEATURE [App::DocumentObjectGroupPython] S_element017  label="S_element : 0.018"  # scripted group (container) (typed FeaturePython)
  n = 0.003
FEATURE [App::DocumentObjectGroupPython] Cl_element016  label="Cl_element : 0.589"  # scripted group (container) (typed FeaturePython)
  n = 0.001
FEATURE [App::DocumentObjectGroupPython] K_element006  label="K_element : 0.004"  # scripted group (container) (typed FeaturePython)
  n = 0.004
FEATURE [App::DocumentObjectGroupPython] G4_MUSCLE_SKELETAL_ICRP  # scripted group (container) (typed FeaturePython)
  Dunit = g/cm3
  Dvalue = 1.05
  Group = -> [H_element057,C_element063,N_element025,O_element065,Na_element011,P_element007,S_element017,Cl_element016,K_element006]
  conduct = 2
  density = 1
  expand = 3
  formula = G4_MUSCLE_SKELETAL_ICRP
  name = G4_MUSCLE_SKELETAL_ICRP
  specific = 4
FEATURE [App::DocumentObjectGroupPython] H_element058  label="H_element : 0.137"  # scripted group (container) (typed FeaturePython)
  n = 0.102102
FEATURE [App::DocumentObjectGroupPython] C_element064  label="C_element : 0.123"  # scripted group (container) (typed FeaturePython)
  n = 0.123123
FEATURE [App::DocumentObjectGroupPython] N_element026  label="N_element : 0.756"  # scripted group (container) (typed FeaturePython)
  n = 0.035035
FEATURE [App::DocumentObjectGroupPython] O_element066  label="O_element : 0.730"  # scripted group (container) (typed FeaturePython)
  n = 0.72973
FEATURE [App::DocumentObjectGroupPython] Na_element012  label="Na_element : 0.099"  # scripted group (container) (typed FeaturePython)
  n = 0.001001
FEATURE [App::DocumentObjectGroupPython] P_element008  label="P_element : 0.106"  # scripted group (container) (typed FeaturePython)
  n = 0.002002
FEATURE [App::DocumentObjectGroupPython] S_element018  label="S_element : 0.019"  # scripted group (container) (typed FeaturePython)
  n = 0.004004
FEATURE [App::DocumentObjectGroupPython] K_element007  label="K_element : 0.016"  # scripted group (container) (typed FeaturePython)
  n = 0.003003
FEATURE [App::DocumentObjectGroupPython] G4_MUSCLE_STRIATED_ICRU  # scripted group (container) (typed FeaturePython)
  Dunit = g/cm3
  Dvalue = 1.04
  Group = -> [H_element058,C_element064,N_element026,O_element066,Na_element012,P_element008,S_element018,K_element007]
  conduct = 2
  density = 1
  expand = 3
  formula = G4_MUSCLE_STRIATED_ICRU
  name = G4_MUSCLE_STRIATED_ICRU
  specific = 4
FEATURE [App::DocumentObjectGroupPython] H_element059  label="H_element : 0.098"  # scripted group (container) (typed FeaturePython)
  n = 0.0982341
FEATURE [App::DocumentObjectGroupPython] C_element065  label="C_element : 0.156"  # scripted group (container) (typed FeaturePython)
  n = 0.156214
FEATURE [App::DocumentObjectGroupPython] N_element027  label="N_element : 0.757"  # scripted group (container) (typed FeaturePython)
  n = 0.035451
FEATURE [App::DocumentObjectGroupPython] O_element067  label="O_element : 0.880"  # scripted group (container) (typed FeaturePython)
  n = 0.710101
FEATURE [App::DocumentObjectGroupPython] G4_MUSCLE_WITH_SUCROSE  # scripted group (container) (typed FeaturePython)
  Dunit = g/cm3
  Dvalue = 1.11
  Group = -> [H_element059,C_element065,N_element027,O_element067]
  conduct = 2
  density = 1
  expand = 3
  formula = G4_MUSCLE_WITH_SUCROSE
  name = G4_MUSCLE_WITH_SUCROSE
  specific = 4
FEATURE [App::DocumentObjectGroupPython] H_element060  label="H_element : 0.138"  # scripted group (container) (typed FeaturePython)
  n = 0.101969
FEATURE [App::DocumentObjectGroupPython] C_element066  label="C_element : 0.120"  # scripted group (container) (typed FeaturePython)
  n = 0.120058
FEATURE [App::DocumentObjectGroupPython] N_element028  label="N_element : 0.758"  # scripted group (container) (typed FeaturePython)
  n = 0.035451
FEATURE [App::DocumentObjectGroupPython] O_element068  label="O_element : 0.743"  # scripted group (container) (typed FeaturePython)
  n = 0.742522
FEATURE [App::DocumentObjectGroupPython] G4_MUSCLE_WITHOUT_SUCROSE  # scripted group (container) (typed FeaturePython)
  Dunit = g/cm3
  Dvalue = 1.07
  Group = -> [H_element060,C_element066,N_element028,O_element068]
  conduct = 2
  density = 1
  expand = 3
  formula = G4_MUSCLE_WITHOUT_SUCROSE
  name = G4_MUSCLE_WITHOUT_SUCROSE
  specific = 4
FEATURE [App::DocumentObjectGroupPython] C_element067  label="C_element : 10"  # scripted group (container) (typed FeaturePython)
  n = 10
  ref = C_element
FEATURE [App::DocumentObjectGroupPython] H_element061  label="H_element : 030"  # scripted group (container) (typed FeaturePython)
  n = 8
  ref = H_element
FEATURE [App::DocumentObjectGroupPython] G4_NAPHTHALENE  # scripted group (container) (typed FeaturePython)
  Dunit = g/cm3
  Dvalue = 1.145
  Group = -> [C_element067,H_element061]
  conduct = 2
  density = 1
  expand = 3
  formula = G4_NAPHTHALENE
  name = G4_NAPHTHALENE
  specific = 4
FEATURE [App::DocumentObjectGroupPython] C_element068  label="C_element : 034"  # scripted group (container) (typed FeaturePython)
  n = 6
  ref = C_element
FEATURE [App::DocumentObjectGroupPython] H_element062  label="H_element : 031"  # scripted group (container) (typed FeaturePython)
  n = 5
  ref = H_element
FEATURE [App::DocumentObjectGroupPython] N_element029  label="N_element : 012"  # scripted group (container) (typed FeaturePython)
  n = 1
  ref = N_element
FEATURE [App::DocumentObjectGroupPython] O_element069  label="O_element : 034"  # scripted group (container) (typed FeaturePython)
  n = 2
  ref = O_element
FEATURE [App::DocumentObjectGroupPython] G4_NITROBENZENE  # scripted group (container) (typed FeaturePython)
  Dunit = g/cm3
  Dvalue = 1.19867
  Group = -> [C_element068,H_element062,N_element029,O_element069]
  conduct = 2
  density = 1
  expand = 3
  formula = G4_NITROBENZENE
  name = G4_NITROBENZENE
  specific = 4
FEATURE [App::DocumentObjectGroupPython] N_element030  label="N_element : 013"  # scripted group (container) (typed FeaturePython)
  n = 2
  ref = N_element
FEATURE [App::DocumentObjectGroupPython] O_element070  label="O_element : 035"  # scripted group (container) (typed FeaturePython)
  n = 1
  ref = O_element
FEATURE [App::DocumentObjectGroupPython] G4_NITROUS_OXIDE  # scripted group (container) (typed FeaturePython)
  Dunit = g/cm3
  Dvalue = 0.00183094
  Group = -> [N_element030,O_element070]
  conduct = 2
  density = 1
  expand = 3
  formula = G4_NITROUS_OXIDE
  name = G4_NITROUS_OXIDE
  specific = 4
FEATURE [App::DocumentObjectGroupPython] H_element063  label="H_element : 0.104"  # scripted group (container) (typed FeaturePython)
  n = 0.103509
FEATURE [App::DocumentObjectGroupPython] C_element069  label="C_element : 0.648"  # scripted group (container) (typed FeaturePython)
  n = 0.648416
FEATURE [App::DocumentObjectGroupPython] N_element031  label="N_element : 0.100"  # scripted group (container) (typed FeaturePython)
  n = 0.0995361
FEATURE [App::DocumentObjectGroupPython] O_element071  label="O_element : 0.149"  # scripted group (container) (typed FeaturePython)
  n = 0.148539
FEATURE [App::DocumentObjectGroupPython] G4_NYLON_8062  label="G4_NYLON-8062"  # scripted group (container) (typed FeaturePython)
  Dunit = g/cm3
  Dvalue = 1.08
  Group = -> [H_element063,C_element069,N_element031,O_element071]
  conduct = 2
  density = 1
  expand = 3
  formula = G4_NYLON-8062
  name = G4_NYLON-8062
  specific = 4
FEATURE [App::DocumentObjectGroupPython] C_element070  label="C_element : 035"  # scripted group (container) (typed FeaturePython)
  n = 6
  ref = C_element
FEATURE [App::DocumentObjectGroupPython] H_element064  label="H_element : 11"  # scripted group (container) (typed FeaturePython)
  n = 11
  ref = H_element
FEATURE [App::DocumentObjectGroupPython] N_element032  label="N_element : 014"  # scripted group (container) (typed FeaturePython)
  n = 1
  ref = N_element
FEATURE [App::DocumentObjectGroupPython] O_element072  label="O_element : 036"  # scripted group (container) (typed FeaturePython)
  n = 1
  ref = O_element
FEATURE [App::DocumentObjectGroupPython] G4_NYLON_6_6  label="G4_NYLON-6-6"  # scripted group (container) (typed FeaturePython)
  Dunit = g/cm3
  Dvalue = 1.14
  Group = -> [C_element070,H_element064,N_element032,O_element072]
  conduct = 2
  density = 1
  expand = 3
  formula = G4_NYLON-6-6
  name = G4_NYLON-6-6
  specific = 4
FEATURE [App::DocumentObjectGroupPython] H_element065  label="H_element : 0.139"  # scripted group (container) (typed FeaturePython)
  n = 0.107062
FEATURE [App::DocumentObjectGroupPython] C_element071  label="C_element : 0.680"  # scripted group (container) (typed FeaturePython)
  n = 0.680449
FEATURE [App::DocumentObjectGroupPython] N_element033  label="N_element : 0.099"  # scripted group (container) (typed FeaturePython)
  n = 0.099189
FEATURE [App::DocumentObjectGroupPython] O_element073  label="O_element : 0.113"  # scripted group (container) (typed FeaturePython)
  n = 0.1133
FEATURE [App::DocumentObjectGroupPython] G4_NYLON_6_10  label="G4_NYLON-6-10"  # scripted group (container) (typed FeaturePython)
  Dunit = g/cm3
  Dvalue = 1.14
  Group = -> [H_element065,C_element071,N_element033,O_element073]
  conduct = 2
  density = 1
  expand = 3
  formula = G4_NYLON-6-10
  name = G4_NYLON-6-10
  specific = 4
FEATURE [App::DocumentObjectGroupPython] H_element066  label="H_element : 0.140"  # scripted group (container) (typed FeaturePython)
  n = 0.115476
FEATURE [App::DocumentObjectGroupPython] C_element072  label="C_element : 0.721"  # scripted group (container) (typed FeaturePython)
  n = 0.720818
FEATURE [App::DocumentObjectGroupPython] N_element034  label="N_element : 0.076"  # scripted group (container) (typed FeaturePython)
  n = 0.0764169
FEATURE [App::DocumentObjectGroupPython] O_element074  label="O_element : 0.087"  # scripted group (container) (typed FeaturePython)
  n = 0.0872889
FEATURE [App::DocumentObjectGroupPython] G4_NYLON_11_RILSAN  label="G4_NYLON-11_RILSAN"  # scripted group (container) (typed FeaturePython)
  Dunit = g/cm3
  Dvalue = 1.425
  Group = -> [H_element066,C_element072,N_element034,O_element074]
  conduct = 2
  density = 1
  expand = 3
  formula = G4_NYLON-11_RILSAN
  name = G4_NYLON-11_RILSAN
  specific = 4
FEATURE [App::DocumentObjectGroupPython] C_element073  label="C_element : 8"  # scripted group (container) (typed FeaturePython)
  n = 8
  ref = C_element
FEATURE [App::DocumentObjectGroupPython] H_element067  label="H_element : 18"  # scripted group (container) (typed FeaturePython)
  n = 18
  ref = H_element
FEATURE [App::DocumentObjectGroupPython] G4_OCTANE  # scripted group (container) (typed FeaturePython)
  Dunit = g/cm3
  Dvalue = 0.7026
  Group = -> [C_element073,H_element067]
  conduct = 2
  density = 1
  expand = 3
  formula = G4_OCTANE
  name = G4_OCTANE
  specific = 4
FEATURE [App::DocumentObjectGroupPython] C_element074  label="C_element : 25"  # scripted group (container) (typed FeaturePython)
  n = 25
  ref = C_element
FEATURE [App::DocumentObjectGroupPython] H_element068  label="H_element : 52"  # scripted group (container) (typed FeaturePython)
  n = 52
  ref = H_element
FEATURE [App::DocumentObjectGroupPython] G4_PARAFFIN  # scripted group (container) (typed FeaturePython)
  Dunit = g/cm3
  Dvalue = 0.93
  Group = -> [C_element074,H_element068]
  conduct = 2
  density = 1
  expand = 3
  formula = G4_PARAFFIN
  name = G4_PARAFFIN
  specific = 4
FEATURE [App::DocumentObjectGroupPython] C_element075  label="C_element : 036"  # scripted group (container) (typed FeaturePython)
  n = 5
  ref = C_element
FEATURE [App::DocumentObjectGroupPython] H_element069  label="H_element : 032"  # scripted group (container) (typed FeaturePython)
  n = 12
  ref = H_element
FEATURE [App::DocumentObjectGroupPython] G4_N_PENTANE  label="G4_N-PENTANE"  # scripted group (container) (typed FeaturePython)
  Dunit = g/cm3
  Dvalue = 0.6262
  Group = -> [C_element075,H_element069]
  conduct = 2
  density = 1
  expand = 3
  formula = G4_N-PENTANE
  name = G4_N-PENTANE
  specific = 4
FEATURE [App::DocumentObjectGroupPython] H_element070  label="H_element : 0.014"  # scripted group (container) (typed FeaturePython)
  n = 0.0141
FEATURE [App::DocumentObjectGroupPython] C_element076  label="C_element : 0.072"  # scripted group (container) (typed FeaturePython)
  n = 0.072261
FEATURE [App::DocumentObjectGroupPython] N_element035  label="N_element : 0.019"  # scripted group (container) (typed FeaturePython)
  n = 0.01932
FEATURE [App::DocumentObjectGroupPython] O_element075  label="O_element : 0.066"  # scripted group (container) (typed FeaturePython)
  n = 0.066101
FEATURE [App::DocumentObjectGroupPython] S_element019  label="S_element : 0.020"  # scripted group (container) (typed FeaturePython)
  n = 0.00189
FEATURE [App::DocumentObjectGroupPython] Br_element004  label="Br_element : 0.349"  # scripted group (container) (typed FeaturePython)
  n = 0.349103
FEATURE [App::DocumentObjectGroupPython] Ag_element001  label="Ag_element : 0.474"  # scripted group (container) (typed FeaturePython)
  n = 0.474105
FEATURE [App::DocumentObjectGroupPython] I_element005  label="I_element : 0.003"  # scripted group (container) (typed FeaturePython)
  n = 0.00312
FEATURE [App::DocumentObjectGroupPython] G4_PHOTO_EMULSION  # scripted group (container) (typed FeaturePython)
  Dunit = g/cm3
  Dvalue = 3.815
  Group = -> [H_element070,C_element076,N_element035,O_element075,S_element019,Br_element004,Ag_element001,I_element005]
  conduct = 2
  density = 1
  expand = 3
  formula = G4_PHOTO_EMULSION
  name = G4_PHOTO_EMULSION
  specific = 4
FEATURE [App::DocumentObjectGroupPython] C_element077  label="C_element : 9"  # scripted group (container) (typed FeaturePython)
  n = 9
  ref = C_element
FEATURE [App::DocumentObjectGroupPython] H_element071  label="H_element : 033"  # scripted group (container) (typed FeaturePython)
  n = 10
  ref = H_element
FEATURE [App::DocumentObjectGroupPython] G4_PLASTIC_SC_VINYLTOLUENE  # scripted group (container) (typed FeaturePython)
  Dunit = g/cm3
  Dvalue = 1.032
  Group = -> [C_element077,H_element071]
  conduct = 2
  density = 1
  expand = 3
  formula = G4_PLASTIC_SC_VINYLTOLUENE
  name = G4_PLASTIC_SC_VINYLTOLUENE
  specific = 4
FEATURE [App::DocumentObjectGroupPython] Pu_element001  label="Pu_element : 1"  # scripted group (container) (typed FeaturePython)
  n = 1
  ref = Pu_element
FEATURE [App::DocumentObjectGroupPython] O_element076  label="O_element : 037"  # scripted group (container) (typed FeaturePython)
  n = 2
  ref = O_element
FEATURE [App::DocumentObjectGroupPython] G4_PLUTONIUM_DIOXIDE  # scripted group (container) (typed FeaturePython)
  Dunit = g/cm3
  Dvalue = 11.46
  Group = -> [Pu_element001,O_element076]
  conduct = 2
  density = 1
  expand = 3
  formula = G4_PLUTONIUM_DIOXIDE
  name = G4_PLUTONIUM_DIOXIDE
  specific = 4
FEATURE [App::DocumentObjectGroupPython] C_element078  label="C_element : 037"  # scripted group (container) (typed FeaturePython)
  n = 3
  ref = C_element
FEATURE [App::DocumentObjectGroupPython] H_element072  label="H_element : 034"  # scripted group (container) (typed FeaturePython)
  n = 3
  ref = H_element
FEATURE [App::DocumentObjectGroupPython] N_element036  label="N_element : 015"  # scripted group (container) (typed FeaturePython)
  n = 1
  ref = N_element
FEATURE [App::DocumentObjectGroupPython] G4_POLYACRYLONITRILE  # scripted group (container) (typed FeaturePython)
  Dunit = g/cm3
  Dvalue = 1.17
  Group = -> [C_element078,H_element072,N_element036]
  conduct = 2
  density = 1
  expand = 3
  formula = G4_POLYACRYLONITRILE
  name = G4_POLYACRYLONITRILE
  specific = 4
FEATURE [App::DocumentObjectGroupPython] C_element079  label="C_element : 16"  # scripted group (container) (typed FeaturePython)
  n = 16
  ref = C_element
FEATURE [App::DocumentObjectGroupPython] H_element073  label="H_element : 035"  # scripted group (container) (typed FeaturePython)
  n = 14
  ref = H_element
FEATURE [App::DocumentObjectGroupPython] O_element077  label="O_element : 038"  # scripted group (container) (typed FeaturePython)
  n = 3
  ref = O_element
FEATURE [App::DocumentObjectGroupPython] G4_POLYCARBONATE  # scripted group (container) (typed FeaturePython)
  Dunit = g/cm3
  Dvalue = 1.2
  Group = -> [C_element079,H_element073,O_element077]
  conduct = 2
  density = 1
  expand = 3
  formula = G4_POLYCARBONATE
  name = G4_POLYCARBONATE
  specific = 4
FEATURE [App::DocumentObjectGroupPython] C_element080  label="C_element : 038"  # scripted group (container) (typed FeaturePython)
  n = 8
  ref = C_element
FEATURE [App::DocumentObjectGroupPython] H_element074  label="H_element : 036"  # scripted group (container) (typed FeaturePython)
  n = 7
  ref = H_element
FEATURE [App::DocumentObjectGroupPython] Cl_element017  label="Cl_element : 007"  # scripted group (container) (typed FeaturePython)
  n = 1
  ref = Cl_element
FEATURE [App::DocumentObjectGroupPython] G4_POLYCHLOROSTYRENE  # scripted group (container) (typed FeaturePython)
  Dunit = g/cm3
  Dvalue = 1.3
  Group = -> [C_element080,H_element074,Cl_element017]
  conduct = 2
  density = 1
  expand = 3
  formula = G4_POLYCHLOROSTYRENE
  name = G4_POLYCHLOROSTYRENE
  specific = 4
FEATURE [App::DocumentObjectGroupPython] C_element081  label="C_element : 039"  # scripted group (container) (typed FeaturePython)
  n = 1
  ref = C_element
FEATURE [App::DocumentObjectGroupPython] H_element075  label="H_element : 037"  # scripted group (container) (typed FeaturePython)
  n = 2
  ref = H_element
FEATURE [App::DocumentObjectGroupPython] G4_POLYETHYLENE  # scripted group (container) (typed FeaturePython)
  Dunit = g/cm3
  Dvalue = 0.94
  Group = -> [C_element081,H_element075]
  conduct = 2
  density = 1
  expand = 3
  formula = G4_POLYETHYLENE
  name = G4_POLYETHYLENE
  specific = 4
FEATURE [App::DocumentObjectGroupPython] C_element082  label="C_element : 040"  # scripted group (container) (typed FeaturePython)
  n = 10
  ref = C_element
FEATURE [App::DocumentObjectGroupPython] H_element076  label="H_element : 038"  # scripted group (container) (typed FeaturePython)
  n = 8
  ref = H_element
FEATURE [App::DocumentObjectGroupPython] O_element078  label="O_element : 039"  # scripted group (container) (typed FeaturePython)
  n = 4
  ref = O_element
FEATURE [App::DocumentObjectGroupPython] G4_MYLAR  # scripted group (container) (typed FeaturePython)
  Dunit = g/cm3
  Dvalue = 1.4
  Group = -> [C_element082,H_element076,O_element078]
  conduct = 2
  density = 1
  expand = 3
  formula = G4_MYLAR
  name = G4_MYLAR
  specific = 4
FEATURE [App::DocumentObjectGroupPython] C_element083  label="C_element : 041"  # scripted group (container) (typed FeaturePython)
  n = 5
  ref = C_element
FEATURE [App::DocumentObjectGroupPython] H_element077  label="H_element : 039"  # scripted group (container) (typed FeaturePython)
  n = 8
  ref = H_element
FEATURE [App::DocumentObjectGroupPython] O_element079  label="O_element : 040"  # scripted group (container) (typed FeaturePython)
  n = 2
  ref = O_element
FEATURE [App::DocumentObjectGroupPython] G4_PLEXIGLASS  # scripted group (container) (typed FeaturePython)
  Dunit = g/cm3
  Dvalue = 1.19
  Group = -> [C_element083,H_element077,O_element079]
  conduct = 2
  density = 1
  expand = 3
  formula = G4_PLEXIGLASS
  name = G4_PLEXIGLASS
  specific = 4
FEATURE [App::DocumentObjectGroupPython] C_element084  label="C_element : 042"  # scripted group (container) (typed FeaturePython)
  n = 1
  ref = C_element
FEATURE [App::DocumentObjectGroupPython] H_element078  label="H_element : 040"  # scripted group (container) (typed FeaturePython)
  n = 2
  ref = H_element
FEATURE [App::DocumentObjectGroupPython] O_element080  label="O_element : 041"  # scripted group (container) (typed FeaturePython)
  n = 1
  ref = O_element
FEATURE [App::DocumentObjectGroupPython] G4_POLYOXYMETHYLENE  # scripted group (container) (typed FeaturePython)
  Dunit = g/cm3
  Dvalue = 1.425
  Group = -> [C_element084,H_element078,O_element080]
  conduct = 2
  density = 1
  expand = 3
  formula = G4_POLYOXYMETHYLENE
  name = G4_POLYOXYMETHYLENE
  specific = 4
FEATURE [App::DocumentObjectGroupPython] C_element085  label="C_element : 043"  # scripted group (container) (typed FeaturePython)
  n = 2
  ref = C_element
FEATURE [App::DocumentObjectGroupPython] H_element079  label="H_element : 041"  # scripted group (container) (typed FeaturePython)
  n = 4
  ref = H_element
FEATURE [App::DocumentObjectGroupPython] G4_POLYPROPYLENE  # scripted group (container) (typed FeaturePython)
  Dunit = g/cm3
  Dvalue = 0.9
  Group = -> [C_element085,H_element079]
  conduct = 2
  density = 1
  expand = 3
  formula = G4_POLYPROPYLENE
  name = G4_POLYPROPYLENE
  specific = 4
FEATURE [App::DocumentObjectGroupPython] C_element086  label="C_element : 044"  # scripted group (container) (typed FeaturePython)
  n = 8
  ref = C_element
FEATURE [App::DocumentObjectGroupPython] H_element080  label="H_element : 042"  # scripted group (container) (typed FeaturePython)
  n = 8
  ref = H_element
FEATURE [App::DocumentObjectGroupPython] G4_POLYSTYRENE  # scripted group (container) (typed FeaturePython)
  Dunit = g/cm3
  Dvalue = 1.06
  Group = -> [C_element086,H_element080]
  conduct = 2
  density = 1
  expand = 3
  formula = G4_POLYSTYRENE
  name = G4_POLYSTYRENE
  specific = 4
FEATURE [App::DocumentObjectGroupPython] C_element087  label="C_element : 045"  # scripted group (container) (typed FeaturePython)
  n = 2
  ref = C_element
FEATURE [App::DocumentObjectGroupPython] F_element014  label="F_element : 4"  # scripted group (container) (typed FeaturePython)
  n = 4
  ref = F_element
FEATURE [App::DocumentObjectGroupPython] G4_TEFLON  # scripted group (container) (typed FeaturePython)
  Dunit = g/cm3
  Dvalue = 2.2
  Group = -> [C_element087,F_element014]
  conduct = 2
  density = 1
  expand = 3
  formula = G4_TEFLON
  name = G4_TEFLON
  specific = 4
FEATURE [App::DocumentObjectGroupPython] C_element088  label="C_element : 046"  # scripted group (container) (typed FeaturePython)
  n = 2
  ref = C_element
FEATURE [App::DocumentObjectGroupPython] F_element015  label="F_element : 006"  # scripted group (container) (typed FeaturePython)
  n = 3
  ref = F_element
FEATURE [App::DocumentObjectGroupPython] Cl_element018  label="Cl_element : 008"  # scripted group (container) (typed FeaturePython)
  n = 1
  ref = Cl_element
FEATURE [App::DocumentObjectGroupPython] G4_POLYTRIFLUOROCHLOROETHYLENE  # scripted group (container) (typed FeaturePython)
  Dunit = g/cm3
  Dvalue = 2.1
  Group = -> [C_element088,F_element015,Cl_element018]
  conduct = 2
  density = 1
  expand = 3
  formula = G4_POLYTRIFLUOROCHLOROETHYLENE
  name = G4_POLYTRIFLUOROCHLOROETHYLENE
  specific = 4
FEATURE [App::DocumentObjectGroupPython] C_element089  label="C_element : 047"  # scripted group (container) (typed FeaturePython)
  n = 4
  ref = C_element
FEATURE [App::DocumentObjectGroupPython] H_element081  label="H_element : 043"  # scripted group (container) (typed FeaturePython)
  n = 6
  ref = H_element
FEATURE [App::DocumentObjectGroupPython] O_element081  label="O_element : 042"  # scripted group (container) (typed FeaturePython)
  n = 2
  ref = O_element
FEATURE [App::DocumentObjectGroupPython] G4_POLYVINYL_ACETATE  # scripted group (container) (typed FeaturePython)
  Dunit = g/cm3
  Dvalue = 1.19
  Group = -> [C_element089,H_element081,O_element081]
  conduct = 2
  density = 1
  expand = 3
  formula = G4_POLYVINYL_ACETATE
  name = G4_POLYVINYL_ACETATE
  specific = 4
FEATURE [App::DocumentObjectGroupPython] C_element090  label="C_element : 048"  # scripted group (container) (typed FeaturePython)
  n = 2
  ref = C_element
FEATURE [App::DocumentObjectGroupPython] H_element082  label="H_element : 044"  # scripted group (container) (typed FeaturePython)
  n = 4
  ref = H_element
FEATURE [App::DocumentObjectGroupPython] O_element082  label="O_element : 043"  # scripted group (container) (typed FeaturePython)
  n = 1
  ref = O_element
FEATURE [App::DocumentObjectGroupPython] G4_POLYVINYL_ALCOHOL  # scripted group (container) (typed FeaturePython)
  Dunit = g/cm3
  Dvalue = 1.3
  Group = -> [C_element090,H_element082,O_element082]
  conduct = 2
  density = 1
  expand = 3
  formula = G4_POLYVINYL_ALCOHOL
  name = G4_POLYVINYL_ALCOHOL
  specific = 4
FEATURE [App::DocumentObjectGroupPython] C_element091  label="C_element : 049"  # scripted group (container) (typed FeaturePython)
  n = 8
  ref = C_element
FEATURE [App::DocumentObjectGroupPython] H_element083  label="H_element : 045"  # scripted group (container) (typed FeaturePython)
  n = 14
  ref = H_element
FEATURE [App::DocumentObjectGroupPython] O_element083  label="O_element : 044"  # scripted group (container) (typed FeaturePython)
  n = 2
  ref = O_element
FEATURE [App::DocumentObjectGroupPython] G4_POLYVINYL_BUTYRAL  # scripted group (container) (typed FeaturePython)
  Dunit = g/cm3
  Dvalue = 1.12
  Group = -> [C_element091,H_element083,O_element083]
  conduct = 2
  density = 1
  expand = 3
  formula = G4_POLYVINYL_BUTYRAL
  name = G4_POLYVINYL_BUTYRAL
  specific = 4
FEATURE [App::DocumentObjectGroupPython] C_element092  label="C_element : 050"  # scripted group (container) (typed FeaturePython)
  n = 2
  ref = C_element
FEATURE [App::DocumentObjectGroupPython] H_element084  label="H_element : 046"  # scripted group (container) (typed FeaturePython)
  n = 3
  ref = H_element
FEATURE [App::DocumentObjectGroupPython] Cl_element019  label="Cl_element : 009"  # scripted group (container) (typed FeaturePython)
  n = 1
  ref = Cl_element
FEATURE [App::DocumentObjectGroupPython] G4_POLYVINYL_CHLORIDE  # scripted group (container) (typed FeaturePython)
  Dunit = g/cm3
  Dvalue = 1.3
  Group = -> [C_element092,H_element084,Cl_element019]
  conduct = 2
  density = 1
  expand = 3
  formula = G4_POLYVINYL_CHLORIDE
  name = G4_POLYVINYL_CHLORIDE
  specific = 4
FEATURE [App::DocumentObjectGroupPython] C_element093  label="C_element : 051"  # scripted group (container) (typed FeaturePython)
  n = 2
  ref = C_element
FEATURE [App::DocumentObjectGroupPython] H_element085  label="H_element : 047"  # scripted group (container) (typed FeaturePython)
  n = 2
  ref = H_element
FEATURE [App::DocumentObjectGroupPython] Cl_element020  label="Cl_element : 010"  # scripted group (container) (typed FeaturePython)
  n = 2
  ref = Cl_element
FEATURE [App::DocumentObjectGroupPython] G4_POLYVINYLIDENE_CHLORIDE  # scripted group (container) (typed FeaturePython)
  Dunit = g/cm3
  Dvalue = 1.7
  Group = -> [C_element093,H_element085,Cl_element020]
  conduct = 2
  density = 1
  expand = 3
  formula = G4_POLYVINYLIDENE_CHLORIDE
  name = G4_POLYVINYLIDENE_CHLORIDE
  specific = 4
FEATURE [App::DocumentObjectGroupPython] C_element094  label="C_element : 052"  # scripted group (container) (typed FeaturePython)
  n = 2
  ref = C_element
FEATURE [App::DocumentObjectGroupPython] H_element086  label="H_element : 048"  # scripted group (container) (typed FeaturePython)
  n = 2
  ref = H_element
FEATURE [App::DocumentObjectGroupPython] F_element016  label="F_element : 007"  # scripted group (container) (typed FeaturePython)
  n = 2
  ref = F_element
FEATURE [App::DocumentObjectGroupPython] G4_POLYVINYLIDENE_FLUORIDE  # scripted group (container) (typed FeaturePython)
  Dunit = g/cm3
  Dvalue = 1.76
  Group = -> [C_element094,H_element086,F_element016]
  conduct = 2
  density = 1
  expand = 3
  formula = G4_POLYVINYLIDENE_FLUORIDE
  name = G4_POLYVINYLIDENE_FLUORIDE
  specific = 4
FEATURE [App::DocumentObjectGroupPython] C_element095  label="C_element : 053"  # scripted group (container) (typed FeaturePython)
  n = 6
  ref = C_element
FEATURE [App::DocumentObjectGroupPython] H_element087  label="H_element : 9"  # scripted group (container) (typed FeaturePython)
  n = 9
  ref = H_element
FEATURE [App::DocumentObjectGroupPython] N_element037  label="N_element : 016"  # scripted group (container) (typed FeaturePython)
  n = 1
  ref = N_element
FEATURE [App::DocumentObjectGroupPython] O_element084  label="O_element : 045"  # scripted group (container) (typed FeaturePython)
  n = 1
  ref = O_element
FEATURE [App::DocumentObjectGroupPython] G4_POLYVINYL_PYRROLIDONE  # scripted group (container) (typed FeaturePython)
  Dunit = g/cm3
  Dvalue = 1.25
  Group = -> [C_element095,H_element087,N_element037,O_element084]
  conduct = 2
  density = 1
  expand = 3
  formula = G4_POLYVINYL_PYRROLIDONE
  name = G4_POLYVINYL_PYRROLIDONE
  specific = 4
FEATURE [App::DocumentObjectGroupPython] K_element008  label="K_element : 1"  # scripted group (container) (typed FeaturePython)
  n = 1
  ref = K_element
FEATURE [App::DocumentObjectGroupPython] I_element006  label="I_element : 003"  # scripted group (container) (typed FeaturePython)
  n = 1
  ref = I_element
FEATURE [App::DocumentObjectGroupPython] G4_POTASSIUM_IODIDE  # scripted group (container) (typed FeaturePython)
  Dunit = g/cm3
  Dvalue = 3.13
  Group = -> [K_element008,I_element006]
  conduct = 2
  density = 1
  expand = 3
  formula = G4_POTASSIUM_IODIDE
  name = G4_POTASSIUM_IODIDE
  specific = 4
FEATURE [App::DocumentObjectGroupPython] K_element009  label="K_element : 2"  # scripted group (container) (typed FeaturePython)
  n = 2
  ref = K_element
FEATURE [App::DocumentObjectGroupPython] O_element085  label="O_element : 046"  # scripted group (container) (typed FeaturePython)
  n = 1
  ref = O_element
FEATURE [App::DocumentObjectGroupPython] G4_POTASSIUM_OXIDE  # scripted group (container) (typed FeaturePython)
  Dunit = g/cm3
  Dvalue = 2.32
  Group = -> [K_element009,O_element085]
  conduct = 2
  density = 1
  expand = 3
  formula = G4_POTASSIUM_OXIDE
  name = G4_POTASSIUM_OXIDE
  specific = 4
FEATURE [App::DocumentObjectGroupPython] C_element096  label="C_element : 054"  # scripted group (container) (typed FeaturePython)
  n = 3
  ref = C_element
FEATURE [App::DocumentObjectGroupPython] H_element088  label="H_element : 049"  # scripted group (container) (typed FeaturePython)
  n = 8
  ref = H_element
FEATURE [App::DocumentObjectGroupPython] G4_PROPANE  # scripted group (container) (typed FeaturePython)
  Dunit = g/cm3
  Dvalue = 0.00187939
  Group = -> [C_element096,H_element088]
  conduct = 2
  density = 1
  expand = 3
  formula = G4_PROPANE
  name = G4_PROPANE
  specific = 4
FEATURE [App::DocumentObjectGroupPython] C_element097  label="C_element : 055"  # scripted group (container) (typed FeaturePython)
  n = 3
  ref = C_element
FEATURE [App::DocumentObjectGroupPython] H_element089  label="H_element : 050"  # scripted group (container) (typed FeaturePython)
  n = 8
  ref = H_element
FEATURE [App::DocumentObjectGroupPython] G4_lPROPANE  # scripted group (container) (typed FeaturePython)
  Dunit = g/cm3
  Dvalue = 0.43
  Group = -> [C_element097,H_element089]
  conduct = 2
  density = 1
  expand = 3
  formula = G4_lPROPANE
  name = G4_lPROPANE
  specific = 4
FEATURE [App::DocumentObjectGroupPython] C_element098  label="C_element : 056"  # scripted group (container) (typed FeaturePython)
  n = 3
  ref = C_element
FEATURE [App::DocumentObjectGroupPython] H_element090  label="H_element : 051"  # scripted group (container) (typed FeaturePython)
  n = 8
  ref = H_element
FEATURE [App::DocumentObjectGroupPython] O_element086  label="O_element : 047"  # scripted group (container) (typed FeaturePython)
  n = 1
  ref = O_element
FEATURE [App::DocumentObjectGroupPython] G4_N_PROPYL_ALCOHOL  label="G4_N-PROPYL_ALCOHOL"  # scripted group (container) (typed FeaturePython)
  Dunit = g/cm3
  Dvalue = 0.8035
  Group = -> [C_element098,H_element090,O_element086]
  conduct = 2
  density = 1
  expand = 3
  formula = G4_N-PROPYL_ALCOHOL
  name = G4_N-PROPYL_ALCOHOL
  specific = 4
FEATURE [App::DocumentObjectGroupPython] C_element099  label="C_element : 057"  # scripted group (container) (typed FeaturePython)
  n = 5
  ref = C_element
FEATURE [App::DocumentObjectGroupPython] H_element091  label="H_element : 052"  # scripted group (container) (typed FeaturePython)
  n = 5
  ref = H_element
FEATURE [App::DocumentObjectGroupPython] N_element038  label="N_element : 017"  # scripted group (container) (typed FeaturePython)
  n = 1
  ref = N_element
FEATURE [App::DocumentObjectGroupPython] G4_PYRIDINE  # scripted group (container) (typed FeaturePython)
  Dunit = g/cm3
  Dvalue = 0.9819
  Group = -> [C_element099,H_element091,N_element038]
  conduct = 2
  density = 1
  expand = 3
  formula = G4_PYRIDINE
  name = G4_PYRIDINE
  specific = 4
FEATURE [App::DocumentObjectGroupPython] H_element092  label="H_element : 0.144"  # scripted group (container) (typed FeaturePython)
  n = 0.143711
FEATURE [App::DocumentObjectGroupPython] C_element100  label="C_element : 0.856"  # scripted group (container) (typed FeaturePython)
  n = 0.856289
FEATURE [App::DocumentObjectGroupPython] G4_RUBBER_BUTYL  # scripted group (container) (typed FeaturePython)
  Dunit = g/cm3
  Dvalue = 0.92
  Group = -> [H_element092,C_element100]
  conduct = 2
  density = 1
  expand = 3
  formula = G4_RUBBER_BUTYL
  name = G4_RUBBER_BUTYL
  specific = 4
FEATURE [App::DocumentObjectGroupPython] H_element093  label="H_element : 0.118"  # scripted group (container) (typed FeaturePython)
  n = 0.118371
FEATURE [App::DocumentObjectGroupPython] C_element101  label="C_element : 0.882"  # scripted group (container) (typed FeaturePython)
  n = 0.881629
FEATURE [App::DocumentObjectGroupPython] G4_RUBBER_NATURAL  # scripted group (container) (typed FeaturePython)
  Dunit = g/cm3
  Dvalue = 0.92
  Group = -> [H_element093,C_element101]
  conduct = 2
  density = 1
  expand = 3
  formula = G4_RUBBER_NATURAL
  name = G4_RUBBER_NATURAL
  specific = 4
FEATURE [App::DocumentObjectGroupPython] H_element094  label="H_element : 0.145"  # scripted group (container) (typed FeaturePython)
  n = 0.05692
FEATURE [App::DocumentObjectGroupPython] C_element102  label="C_element : 0.543"  # scripted group (container) (typed FeaturePython)
  n = 0.542646
FEATURE [App::DocumentObjectGroupPython] Cl_element021  label="Cl_element : 0.400"  # scripted group (container) (typed FeaturePython)
  n = 0.400434
FEATURE [App::DocumentObjectGroupPython] G4_RUBBER_NEOPRENE  # scripted group (container) (typed FeaturePython)
  Dunit = g/cm3
  Dvalue = 1.23
  Group = -> [H_element094,C_element102,Cl_element021]
  conduct = 2
  density = 1
  expand = 3
  formula = G4_RUBBER_NEOPRENE
  name = G4_RUBBER_NEOPRENE
  specific = 4
FEATURE [App::DocumentObjectGroupPython] Si_element006  label="Si_element : 1"  # scripted group (container) (typed FeaturePython)
  n = 1
  ref = Si_element
FEATURE [App::DocumentObjectGroupPython] O_element087  label="O_element : 048"  # scripted group (container) (typed FeaturePython)
  n = 2
  ref = O_element
FEATURE [App::DocumentObjectGroupPython] G4_SILICON_DIOXIDE  # scripted group (container) (typed FeaturePython)
  Dunit = g/cm3
  Dvalue = 2.32
  Group = -> [Si_element006,O_element087]
  conduct = 2
  density = 1
  expand = 3
  formula = G4_SILICON_DIOXIDE
  name = G4_SILICON_DIOXIDE
  specific = 4
FEATURE [App::DocumentObjectGroupPython] Ag_element002  label="Ag_element : 1"  # scripted group (container) (typed FeaturePython)
  n = 1
  ref = Ag_element
FEATURE [App::DocumentObjectGroupPython] Br_element005  label="Br_element : 003"  # scripted group (container) (typed FeaturePython)
  n = 1
  ref = Br_element
FEATURE [App::DocumentObjectGroupPython] G4_SILVER_BROMIDE  # scripted group (container) (typed FeaturePython)
  Dunit = g/cm3
  Dvalue = 6.473
  Group = -> [Ag_element002,Br_element005]
  conduct = 2
  density = 1
  expand = 3
  formula = G4_SILVER_BROMIDE
  name = G4_SILVER_BROMIDE
  specific = 4
FEATURE [App::DocumentObjectGroupPython] Ag_element003  label="Ag_element : 002"  # scripted group (container) (typed FeaturePython)
  n = 1
  ref = Ag_element
FEATURE [App::DocumentObjectGroupPython] Cl_element022  label="Cl_element : 011"  # scripted group (container) (typed FeaturePython)
  n = 1
  ref = Cl_element
FEATURE [App::DocumentObjectGroupPython] G4_SILVER_CHLORIDE  # scripted group (container) (typed FeaturePython)
  Dunit = g/cm3
  Dvalue = 5.56
  Group = -> [Ag_element003,Cl_element022]
  conduct = 2
  density = 1
  expand = 3
  formula = G4_SILVER_CHLORIDE
  name = G4_SILVER_CHLORIDE
  specific = 4
FEATURE [App::DocumentObjectGroupPython] Br_element006  label="Br_element : 0.423"  # scripted group (container) (typed FeaturePython)
  n = 0.422895
FEATURE [App::DocumentObjectGroupPython] Ag_element004  label="Ag_element : 0.574"  # scripted group (container) (typed FeaturePython)
  n = 0.573748
FEATURE [App::DocumentObjectGroupPython] I_element007  label="I_element : 0.649"  # scripted group (container) (typed FeaturePython)
  n = 0.003357
FEATURE [App::DocumentObjectGroupPython] G4_SILVER_HALIDES  # scripted group (container) (typed FeaturePython)
  Dunit = g/cm3
  Dvalue = 6.47
  Group = -> [Br_element006,Ag_element004,I_element007]
  conduct = 2
  density = 1
  expand = 3
  formula = G4_SILVER_HALIDES
  name = G4_SILVER_HALIDES
  specific = 4
FEATURE [App::DocumentObjectGroupPython] Ag_element005  label="Ag_element : 003"  # scripted group (container) (typed FeaturePython)
  n = 1
  ref = Ag_element
FEATURE [App::DocumentObjectGroupPython] I_element008  label="I_element : 004"  # scripted group (container) (typed FeaturePython)
  n = 1
  ref = I_element
FEATURE [App::DocumentObjectGroupPython] G4_SILVER_IODIDE  # scripted group (container) (typed FeaturePython)
  Dunit = g/cm3
  Dvalue = 6.01
  Group = -> [Ag_element005,I_element008]
  conduct = 2
  density = 1
  expand = 3
  formula = G4_SILVER_IODIDE
  name = G4_SILVER_IODIDE
  specific = 4
FEATURE [App::DocumentObjectGroupPython] H_element095  label="H_element : 0.100"  # scripted group (container) (typed FeaturePython)
  n = 0.1
FEATURE [App::DocumentObjectGroupPython] C_element103  label="C_element : 0.204"  # scripted group (container) (typed FeaturePython)
  n = 0.204
FEATURE [App::DocumentObjectGroupPython] N_element039  label="N_element : 0.759"  # scripted group (container) (typed FeaturePython)
  n = 0.042
FEATURE [App::DocumentObjectGroupPython] O_element088  label="O_element : 0.645"  # scripted group (container) (typed FeaturePython)
  n = 0.645
FEATURE [App::DocumentObjectGroupPython] Na_element013  label="Na_element : 0.100"  # scripted group (container) (typed FeaturePython)
  n = 0.002
FEATURE [App::DocumentObjectGroupPython] P_element009  label="P_element : 0.107"  # scripted group (container) (typed FeaturePython)
  n = 0.001
FEATURE [App::DocumentObjectGroupPython] S_element020  label="S_element : 0.021"  # scripted group (container) (typed FeaturePython)
  n = 0.002
FEATURE [App::DocumentObjectGroupPython] Cl_element023  label="Cl_element : 0.590"  # scripted group (container) (typed FeaturePython)
  n = 0.003
FEATURE [App::DocumentObjectGroupPython] K_element010  label="K_element : 0.001"  # scripted group (container) (typed FeaturePython)
  n = 0.001
FEATURE [App::DocumentObjectGroupPython] G4_SKIN_ICRP  # scripted group (container) (typed FeaturePython)
  Dunit = g/cm3
  Dvalue = 1.09
  Group = -> [H_element095,C_element103,N_element039,O_element088,Na_element013,P_element009,S_element020,Cl_element023,K_element010]
  conduct = 2
  density = 1
  expand = 3
  formula = G4_SKIN_ICRP
  name = G4_SKIN_ICRP
  specific = 4
FEATURE [App::DocumentObjectGroupPython] Na_element014  label="Na_element : 2"  # scripted group (container) (typed FeaturePython)
  n = 2
  ref = Na_element
FEATURE [App::DocumentObjectGroupPython] C_element104  label="C_element : 058"  # scripted group (container) (typed FeaturePython)
  n = 1
  ref = C_element
FEATURE [App::DocumentObjectGroupPython] O_element089  label="O_element : 049"  # scripted group (container) (typed FeaturePython)
  n = 3
  ref = O_element
FEATURE [App::DocumentObjectGroupPython] G4_SODIUM_CARBONATE  # scripted group (container) (typed FeaturePython)
  Dunit = g/cm3
  Dvalue = 2.532
  Group = -> [Na_element014,C_element104,O_element089]
  conduct = 2
  density = 1
  expand = 3
  formula = G4_SODIUM_CARBONATE
  name = G4_SODIUM_CARBONATE
  specific = 4
FEATURE [App::DocumentObjectGroupPython] Na_element015  label="Na_element : 1"  # scripted group (container) (typed FeaturePython)
  n = 1
  ref = Na_element
FEATURE [App::DocumentObjectGroupPython] I_element009  label="I_element : 005"  # scripted group (container) (typed FeaturePython)
  n = 1
  ref = I_element
FEATURE [App::DocumentObjectGroupPython] G4_SODIUM_IODIDE  # scripted group (container) (typed FeaturePython)
  Dunit = g/cm3
  Dvalue = 3.667
  Group = -> [Na_element015,I_element009]
  conduct = 2
  density = 1
  expand = 3
  formula = G4_SODIUM_IODIDE
  name = G4_SODIUM_IODIDE
  specific = 4
FEATURE [App::DocumentObjectGroupPython] Na_element016  label="Na_element : 003"  # scripted group (container) (typed FeaturePython)
  n = 2
  ref = Na_element
FEATURE [App::DocumentObjectGroupPython] O_element090  label="O_element : 050"  # scripted group (container) (typed FeaturePython)
  n = 1
  ref = O_element
FEATURE [App::DocumentObjectGroupPython] G4_SODIUM_MONOXIDE  # scripted group (container) (typed FeaturePython)
  Dunit = g/cm3
  Dvalue = 2.27
  Group = -> [Na_element016,O_element090]
  conduct = 2
  density = 1
  expand = 3
  formula = G4_SODIUM_MONOXIDE
  name = G4_SODIUM_MONOXIDE
  specific = 4
FEATURE [App::DocumentObjectGroupPython] Na_element017  label="Na_element : 004"  # scripted group (container) (typed FeaturePython)
  n = 1
  ref = Na_element
FEATURE [App::DocumentObjectGroupPython] N_element040  label="N_element : 018"  # scripted group (container) (typed FeaturePython)
  n = 1
  ref = N_element
FEATURE [App::DocumentObjectGroupPython] O_element091  label="O_element : 051"  # scripted group (container) (typed FeaturePython)
  n = 3
  ref = O_element
FEATURE [App::DocumentObjectGroupPython] G4_SODIUM_NITRATE  # scripted group (container) (typed FeaturePython)
  Dunit = g/cm3
  Dvalue = 2.261
  Group = -> [Na_element017,N_element040,O_element091]
  conduct = 2
  density = 1
  expand = 3
  formula = G4_SODIUM_NITRATE
  name = G4_SODIUM_NITRATE
  specific = 4
FEATURE [App::DocumentObjectGroupPython] C_element105  label="C_element : 059"  # scripted group (container) (typed FeaturePython)
  n = 14
  ref = C_element
FEATURE [App::DocumentObjectGroupPython] H_element096  label="H_element : 053"  # scripted group (container) (typed FeaturePython)
  n = 12
  ref = H_element
FEATURE [App::DocumentObjectGroupPython] G4_STILBENE  # scripted group (container) (typed FeaturePython)
  Dunit = g/cm3
  Dvalue = 0.9707
  Group = -> [C_element105,H_element096]
  conduct = 2
  density = 1
  expand = 3
  formula = G4_STILBENE
  name = G4_STILBENE
  specific = 4
FEATURE [App::DocumentObjectGroupPython] C_element106  label="C_element : 12"  # scripted group (container) (typed FeaturePython)
  n = 12
  ref = C_element
FEATURE [App::DocumentObjectGroupPython] H_element097  label="H_element : 22"  # scripted group (container) (typed FeaturePython)
  n = 22
  ref = H_element
FEATURE [App::DocumentObjectGroupPython] O_element092  label="O_element : 11"  # scripted group (container) (typed FeaturePython)
  n = 11
  ref = O_element
FEATURE [App::DocumentObjectGroupPython] G4_SUCROSE  # scripted group (container) (typed FeaturePython)
  Dunit = g/cm3
  Dvalue = 1.5805
  Group = -> [C_element106,H_element097,O_element092]
  conduct = 2
  density = 1
  expand = 3
  formula = G4_SUCROSE
  name = G4_SUCROSE
  specific = 4
FEATURE [App::DocumentObjectGroupPython] C_element107  label="C_element : 18"  # scripted group (container) (typed FeaturePython)
  n = 18
  ref = C_element
FEATURE [App::DocumentObjectGroupPython] H_element098  label="H_element : 054"  # scripted group (container) (typed FeaturePython)
  n = 14
  ref = H_element
FEATURE [App::DocumentObjectGroupPython] G4_TERPHENYL  # scripted group (container) (typed FeaturePython)
  Dunit = g/cm3
  Dvalue = 1.24
  Group = -> [C_element107,H_element098]
  conduct = 2
  density = 1
  expand = 3
  formula = G4_TERPHENYL
  name = G4_TERPHENYL
  specific = 4
FEATURE [App::DocumentObjectGroupPython] H_element099  label="H_element : 0.146"  # scripted group (container) (typed FeaturePython)
  n = 0.106
FEATURE [App::DocumentObjectGroupPython] C_element108  label="C_element : 0.883"  # scripted group (container) (typed FeaturePython)
  n = 0.099
FEATURE [App::DocumentObjectGroupPython] N_element041  label="N_element : 0.020"  # scripted group (container) (typed FeaturePython)
  n = 0.02
FEATURE [App::DocumentObjectGroupPython] O_element093  label="O_element : 0.766"  # scripted group (container) (typed FeaturePython)
  n = 0.766
FEATURE [App::DocumentObjectGroupPython] Na_element018  label="Na_element : 0.101"  # scripted group (container) (typed FeaturePython)
  n = 0.002
FEATURE [App::DocumentObjectGroupPython] P_element010  label="P_element : 0.108"  # scripted group (container) (typed FeaturePython)
  n = 0.001
FEATURE [App::DocumentObjectGroupPython] S_element021  label="S_element : 0.022"  # scripted group (container) (typed FeaturePython)
  n = 0.002
FEATURE [App::DocumentObjectGroupPython] Cl_element024  label="Cl_element : 0.002"  # scripted group (container) (typed FeaturePython)
  n = 0.002
FEATURE [App::DocumentObjectGroupPython] K_element011  label="K_element : 0.017"  # scripted group (container) (typed FeaturePython)
  n = 0.002
FEATURE [App::DocumentObjectGroupPython] G4_TESTIS_ICRP  # scripted group (container) (typed FeaturePython)
  Dunit = g/cm3
  Dvalue = 1.04
  Group = -> [H_element099,C_element108,N_element041,O_element093,Na_element018,P_element010,S_element021,Cl_element024,K_element011]
  conduct = 2
  density = 1
  expand = 3
  formula = G4_TESTIS_ICRP
  name = G4_TESTIS_ICRP
  specific = 4
FEATURE [App::DocumentObjectGroupPython] C_element109  label="C_element : 060"  # scripted group (container) (typed FeaturePython)
  n = 2
  ref = C_element
FEATURE [App::DocumentObjectGroupPython] Cl_element025  label="Cl_element : 012"  # scripted group (container) (typed FeaturePython)
  n = 4
  ref = Cl_element
FEATURE [App::DocumentObjectGroupPython] G4_TETRACHLOROETHYLENE  # scripted group (container) (typed FeaturePython)
  Dunit = g/cm3
  Dvalue = 1.625
  Group = -> [C_element109,Cl_element025]
  conduct = 2
  density = 1
  expand = 3
  formula = G4_TETRACHLOROETHYLENE
  name = G4_TETRACHLOROETHYLENE
  specific = 4
FEATURE [App::DocumentObjectGroupPython] Tl_element001  label="Tl_element : 1"  # scripted group (container) (typed FeaturePython)
  n = 1
  ref = Tl_element
FEATURE [App::DocumentObjectGroupPython] Cl_element026  label="Cl_element : 013"  # scripted group (container) (typed FeaturePython)
  n = 1
  ref = Cl_element
FEATURE [App::DocumentObjectGroupPython] G4_THALLIUM_CHLORIDE  # scripted group (container) (typed FeaturePython)
  Dunit = g/cm3
  Dvalue = 7.004
  Group = -> [Tl_element001,Cl_element026]
  conduct = 2
  density = 1
  expand = 3
  formula = G4_THALLIUM_CHLORIDE
  name = G4_THALLIUM_CHLORIDE
  specific = 4
FEATURE [App::DocumentObjectGroupPython] H_element100  label="H_element : 0.147"  # scripted group (container) (typed FeaturePython)
  n = 0.105
FEATURE [App::DocumentObjectGroupPython] C_element110  label="C_element : 0.256"  # scripted group (container) (typed FeaturePython)
  n = 0.256
FEATURE [App::DocumentObjectGroupPython] N_element042  label="N_element : 0.760"  # scripted group (container) (typed FeaturePython)
  n = 0.027
FEATURE [App::DocumentObjectGroupPython] O_element094  label="O_element : 0.602"  # scripted group (container) (typed FeaturePython)
  n = 0.602
FEATURE [App::DocumentObjectGroupPython] Na_element019  label="Na_element : 0.102"  # scripted group (container) (typed FeaturePython)
  n = 0.001
FEATURE [App::DocumentObjectGroupPython] P_element011  label="P_element : 0.109"  # scripted group (container) (typed FeaturePython)
  n = 0.002
FEATURE [App::DocumentObjectGroupPython] S_element022  label="S_element : 0.023"  # scripted group (container) (typed FeaturePython)
  n = 0.003
FEATURE [App::DocumentObjectGroupPython] Cl_element027  label="Cl_element : 0.591"  # scripted group (container) (typed FeaturePython)
  n = 0.002
FEATURE [App::DocumentObjectGroupPython] K_element012  label="K_element : 0.018"  # scripted group (container) (typed FeaturePython)
  n = 0.002
FEATURE [App::DocumentObjectGroupPython] G4_TISSUE_SOFT_ICRP  # scripted group (container) (typed FeaturePython)
  Dunit = g/cm3
  Dvalue = 1.03
  Group = -> [H_element100,C_element110,N_element042,O_element094,Na_element019,P_element011,S_element022,Cl_element027,K_element012]
  conduct = 2
  density = 1
  expand = 3
  formula = G4_TISSUE_SOFT_ICRP
  name = G4_TISSUE_SOFT_ICRP
  specific = 4
FEATURE [App::DocumentObjectGroupPython] H_element101  label="H_element : 0.148"  # scripted group (container) (typed FeaturePython)
  n = 0.101
FEATURE [App::DocumentObjectGroupPython] C_element111  label="C_element : 0.111"  # scripted group (container) (typed FeaturePython)
  n = 0.111
FEATURE [App::DocumentObjectGroupPython] N_element043  label="N_element : 0.026"  # scripted group (container) (typed FeaturePython)
  n = 0.026
FEATURE [App::DocumentObjectGroupPython] O_element095  label="O_element : 0.762"  # scripted group (container) (typed FeaturePython)
  n = 0.762
FEATURE [App::DocumentObjectGroupPython] G4_TISSUE_SOFT_ICRU_4  label="G4_TISSUE_SOFT_ICRU-4"  # scripted group (container) (typed FeaturePython)
  Dunit = g/cm3
  Dvalue = 1
  Group = -> [H_element101,C_element111,N_element043,O_element095]
  conduct = 2
  density = 1
  expand = 3
  formula = G4_TISSUE_SOFT_ICRU-4
  name = G4_TISSUE_SOFT_ICRU-4
  specific = 4
FEATURE [App::DocumentObjectGroupPython] H_element102  label="H_element : 0.149"  # scripted group (container) (typed FeaturePython)
  n = 0.101869
FEATURE [App::DocumentObjectGroupPython] C_element112  label="C_element : 0.456"  # scripted group (container) (typed FeaturePython)
  n = 0.456179
FEATURE [App::DocumentObjectGroupPython] N_element044  label="N_element : 0.761"  # scripted group (container) (typed FeaturePython)
  n = 0.035172
FEATURE [App::DocumentObjectGroupPython] O_element096  label="O_element : 0.407"  # scripted group (container) (typed FeaturePython)
  n = 0.40678
FEATURE [App::DocumentObjectGroupPython] G4_TISSUE_METHANE  label="G4_TISSUE-METHANE"  # scripted group (container) (typed FeaturePython)
  Dunit = g/cm3
  Dvalue = 0.00106409
  Group = -> [H_element102,C_element112,N_element044,O_element096]
  conduct = 2
  density = 1
  expand = 3
  formula = G4_TISSUE-METHANE
  name = G4_TISSUE-METHANE
  specific = 4
FEATURE [App::DocumentObjectGroupPython] H_element103  label="H_element : 0.103"  # scripted group (container) (typed FeaturePython)
  n = 0.102672
FEATURE [App::DocumentObjectGroupPython] C_element113  label="C_element : 0.569"  # scripted group (container) (typed FeaturePython)
  n = 0.56894
FEATURE [App::DocumentObjectGroupPython] N_element045  label="N_element : 0.762"  # scripted group (container) (typed FeaturePython)
  n = 0.035022
FEATURE [App::DocumentObjectGroupPython] O_element097  label="O_element : 0.293"  # scripted group (container) (typed FeaturePython)
  n = 0.293366
FEATURE [App::DocumentObjectGroupPython] G4_TISSUE_PROPANE  label="G4_TISSUE-PROPANE"  # scripted group (container) (typed FeaturePython)
  Dunit = g/cm3
  Dvalue = 0.00182628
  Group = -> [H_element103,C_element113,N_element045,O_element097]
  conduct = 2
  density = 1
  expand = 3
  formula = G4_TISSUE-PROPANE
  name = G4_TISSUE-PROPANE
  specific = 4
FEATURE [App::DocumentObjectGroupPython] Ti_element003  label="Ti_element : 1"  # scripted group (container) (typed FeaturePython)
  n = 1
  ref = Ti_element
FEATURE [App::DocumentObjectGroupPython] O_element098  label="O_element : 052"  # scripted group (container) (typed FeaturePython)
  n = 2
  ref = O_element
FEATURE [App::DocumentObjectGroupPython] G4_TITANIUM_DIOXIDE  # scripted group (container) (typed FeaturePython)
  Dunit = g/cm3
  Dvalue = 4.26
  Group = -> [Ti_element003,O_element098]
  conduct = 2
  density = 1
  expand = 3
  formula = G4_TITANIUM_DIOXIDE
  name = G4_TITANIUM_DIOXIDE
  specific = 4
FEATURE [App::DocumentObjectGroupPython] C_element114  label="C_element : 061"  # scripted group (container) (typed FeaturePython)
  n = 7
  ref = C_element
FEATURE [App::DocumentObjectGroupPython] H_element104  label="H_element : 055"  # scripted group (container) (typed FeaturePython)
  n = 8
  ref = H_element
FEATURE [App::DocumentObjectGroupPython] G4_TOLUENE  # scripted group (container) (typed FeaturePython)
  Dunit = g/cm3
  Dvalue = 0.8669
  Group = -> [C_element114,H_element104]
  conduct = 2
  density = 1
  expand = 3
  formula = G4_TOLUENE
  name = G4_TOLUENE
  specific = 4
FEATURE [App::DocumentObjectGroupPython] C_element115  label="C_element : 062"  # scripted group (container) (typed FeaturePython)
  n = 2
  ref = C_element
FEATURE [App::DocumentObjectGroupPython] H_element105  label="H_element : 056"  # scripted group (container) (typed FeaturePython)
  n = 1
  ref = H_element
FEATURE [App::DocumentObjectGroupPython] Cl_element028  label="Cl_element : 014"  # scripted group (container) (typed FeaturePython)
  n = 3
  ref = Cl_element
FEATURE [App::DocumentObjectGroupPython] G4_TRICHLOROETHYLENE  # scripted group (container) (typed FeaturePython)
  Dunit = g/cm3
  Dvalue = 1.46
  Group = -> [C_element115,H_element105,Cl_element028]
  conduct = 2
  density = 1
  expand = 3
  formula = G4_TRICHLOROETHYLENE
  name = G4_TRICHLOROETHYLENE
  specific = 4
FEATURE [App::DocumentObjectGroupPython] C_element116  label="C_element : 063"  # scripted group (container) (typed FeaturePython)
  n = 6
  ref = C_element
FEATURE [App::DocumentObjectGroupPython] H_element106  label="H_element : 15"  # scripted group (container) (typed FeaturePython)
  n = 15
  ref = H_element
FEATURE [App::DocumentObjectGroupPython] O_element099  label="O_element : 053"  # scripted group (container) (typed FeaturePython)
  n = 4
  ref = O_element
FEATURE [App::DocumentObjectGroupPython] P_element012  label="P_element : 1"  # scripted group (container) (typed FeaturePython)
  n = 1
  ref = P_element
FEATURE [App::DocumentObjectGroupPython] G4_TRIETHYL_PHOSPHATE  # scripted group (container) (typed FeaturePython)
  Dunit = g/cm3
  Dvalue = 1.07
  Group = -> [C_element116,H_element106,O_element099,P_element012]
  conduct = 2
  density = 1
  expand = 3
  formula = G4_TRIETHYL_PHOSPHATE
  name = G4_TRIETHYL_PHOSPHATE
  specific = 4
FEATURE [App::DocumentObjectGroupPython] W_element003  label="W_element : 003"  # scripted group (container) (typed FeaturePython)
  n = 1
  ref = W_element
FEATURE [App::DocumentObjectGroupPython] F_element017  label="F_element : 6"  # scripted group (container) (typed FeaturePython)
  n = 6
  ref = F_element
FEATURE [App::DocumentObjectGroupPython] G4_TUNGSTEN_HEXAFLUORIDE  # scripted group (container) (typed FeaturePython)
  Dunit = g/cm3
  Dvalue = 2.4
  Group = -> [W_element003,F_element017]
  conduct = 2
  density = 1
  expand = 3
  formula = G4_TUNGSTEN_HEXAFLUORIDE
  name = G4_TUNGSTEN_HEXAFLUORIDE
  specific = 4
FEATURE [App::DocumentObjectGroupPython] U_element001  label="U_element : 1"  # scripted group (container) (typed FeaturePython)
  n = 1
  ref = U_element
FEATURE [App::DocumentObjectGroupPython] C_element117  label="C_element : 064"  # scripted group (container) (typed FeaturePython)
  n = 2
  ref = C_element
FEATURE [App::DocumentObjectGroupPython] G4_URANIUM_DICARBIDE  # scripted group (container) (typed FeaturePython)
  Dunit = g/cm3
  Dvalue = 11.28
  Group = -> [U_element001,C_element117]
  conduct = 2
  density = 1
  expand = 3
  formula = G4_URANIUM_DICARBIDE
  name = G4_URANIUM_DICARBIDE
  specific = 4
FEATURE [App::DocumentObjectGroupPython] U_element002  label="U_element : 002"  # scripted group (container) (typed FeaturePython)
  n = 1
  ref = U_element
FEATURE [App::DocumentObjectGroupPython] C_element118  label="C_element : 065"  # scripted group (container) (typed FeaturePython)
  n = 1
  ref = C_element
FEATURE [App::DocumentObjectGroupPython] G4_URANIUM_MONOCARBIDE  # scripted group (container) (typed FeaturePython)
  Dunit = g/cm3
  Dvalue = 13.63
  Group = -> [U_element002,C_element118]
  conduct = 2
  density = 1
  expand = 3
  formula = G4_URANIUM_MONOCARBIDE
  name = G4_URANIUM_MONOCARBIDE
  specific = 4
FEATURE [App::DocumentObjectGroupPython] U_element003  label="U_element : 003"  # scripted group (container) (typed FeaturePython)
  n = 1
  ref = U_element
FEATURE [App::DocumentObjectGroupPython] O_element100  label="O_element : 054"  # scripted group (container) (typed FeaturePython)
  n = 2
  ref = O_element
FEATURE [App::DocumentObjectGroupPython] G4_URANIUM_OXIDE  # scripted group (container) (typed FeaturePython)
  Dunit = g/cm3
  Dvalue = 10.96
  Group = -> [U_element003,O_element100]
  conduct = 2
  density = 1
  expand = 3
  formula = G4_URANIUM_OXIDE
  name = G4_URANIUM_OXIDE
  specific = 4
FEATURE [App::DocumentObjectGroupPython] C_element119  label="C_element : 066"  # scripted group (container) (typed FeaturePython)
  n = 1
  ref = C_element
FEATURE [App::DocumentObjectGroupPython] H_element107  label="H_element : 057"  # scripted group (container) (typed FeaturePython)
  n = 4
  ref = H_element
FEATURE [App::DocumentObjectGroupPython] N_element046  label="N_element : 019"  # scripted group (container) (typed FeaturePython)
  n = 2
  ref = N_element
FEATURE [App::DocumentObjectGroupPython] O_element101  label="O_element : 055"  # scripted group (container) (typed FeaturePython)
  n = 1
  ref = O_element
FEATURE [App::DocumentObjectGroupPython] G4_UREA  # scripted group (container) (typed FeaturePython)
  Dunit = g/cm3
  Dvalue = 1.323
  Group = -> [C_element119,H_element107,N_element046,O_element101]
  conduct = 2
  density = 1
  expand = 3
  formula = G4_UREA
  name = G4_UREA
  specific = 4
FEATURE [App::DocumentObjectGroupPython] C_element120  label="C_element : 067"  # scripted group (container) (typed FeaturePython)
  n = 5
  ref = C_element
FEATURE [App::DocumentObjectGroupPython] H_element108  label="H_element : 058"  # scripted group (container) (typed FeaturePython)
  n = 11
  ref = H_element
FEATURE [App::DocumentObjectGroupPython] N_element047  label="N_element : 020"  # scripted group (container) (typed FeaturePython)
  n = 1
  ref = N_element
FEATURE [App::DocumentObjectGroupPython] O_element102  label="O_element : 056"  # scripted group (container) (typed FeaturePython)
  n = 2
  ref = O_element
FEATURE [App::DocumentObjectGroupPython] G4_VALINE  # scripted group (container) (typed FeaturePython)
  Dunit = g/cm3
  Dvalue = 1.23
  Group = -> [C_element120,H_element108,N_element047,O_element102]
  conduct = 2
  density = 1
  expand = 3
  formula = G4_VALINE
  name = G4_VALINE
  specific = 4
FEATURE [App::DocumentObjectGroupPython] H_element109  label="H_element : 0.009"  # scripted group (container) (typed FeaturePython)
  n = 0.009417
FEATURE [App::DocumentObjectGroupPython] C_element121  label="C_element : 0.281"  # scripted group (container) (typed FeaturePython)
  n = 0.280555
FEATURE [App::DocumentObjectGroupPython] F_element018  label="F_element : 0.710"  # scripted group (container) (typed FeaturePython)
  n = 0.710028
FEATURE [App::DocumentObjectGroupPython] G4_VITON  # scripted group (container) (typed FeaturePython)
  Dunit = g/cm3
  Dvalue = 1.8
  Group = -> [H_element109,C_element121,F_element018]
  conduct = 2
  density = 1
  expand = 3
  formula = G4_VITON
  name = G4_VITON
  specific = 4
FEATURE [App::DocumentObjectGroupPython] H_element110  label="H_element : 059"  # scripted group (container) (typed FeaturePython)
  n = 2
  ref = H_element
FEATURE [App::DocumentObjectGroupPython] O_element103  label="O_element : 057"  # scripted group (container) (typed FeaturePython)
  n = 1
  ref = O_element
FEATURE [App::DocumentObjectGroupPython] G4_WATER  # scripted group (container) (typed FeaturePython)
  Dunit = g/cm3
  Dvalue = 1
  Group = -> [H_element110,O_element103]
  conduct = 2
  density = 1
  expand = 3
  formula = G4_WATER
  name = G4_WATER
  specific = 4
FEATURE [App::DocumentObjectGroupPython] H_element111  label="H_element : 060"  # scripted group (container) (typed FeaturePython)
  n = 2
  ref = H_element
FEATURE [App::DocumentObjectGroupPython] O_element104  label="O_element : 058"  # scripted group (container) (typed FeaturePython)
  n = 1
  ref = O_element
FEATURE [App::DocumentObjectGroupPython] G4_WATER_VAPOR  # scripted group (container) (typed FeaturePython)
  Dunit = g/cm3
  Dvalue = 0.000756182
  Group = -> [H_element111,O_element104]
  conduct = 2
  density = 1
  expand = 3
  formula = G4_WATER_VAPOR
  name = G4_WATER_VAPOR
  specific = 4
FEATURE [App::DocumentObjectGroupPython] C_element122  label="C_element : 068"  # scripted group (container) (typed FeaturePython)
  n = 8
  ref = C_element
FEATURE [App::DocumentObjectGroupPython] H_element112  label="H_element : 061"  # scripted group (container) (typed FeaturePython)
  n = 10
  ref = H_element
FEATURE [App::DocumentObjectGroupPython] G4_XYLENE  # scripted group (container) (typed FeaturePython)
  Dunit = g/cm3
  Dvalue = 0.87
  Group = -> [C_element122,H_element112]
  conduct = 2
  density = 1
  expand = 3
  formula = G4_XYLENE
  name = G4_XYLENE
  specific = 4
FEATURE [App::DocumentObjectGroupPython] C_element123  label="C_element : 069"  # scripted group (container) (typed FeaturePython)
  n = 1
  ref = C_element
FEATURE [App::DocumentObjectGroupPython] G4_GRAPHITE  # scripted group (container) (typed FeaturePython)
  Dunit = g/cm3
  Dvalue = 2.21
  Group = -> [C_element123]
  conduct = 2
  density = 1
  expand = 3
  formula = G4_GRAPHITE
  name = G4_GRAPHITE
  specific = 4
FEATURE [App::DocumentObjectGroupPython] NIST  # scripted group (container) (typed FeaturePython)
  Group = -> [G4_A_150_TISSUE,G4_ACETONE,G4_ACETYLENE,G4_ADENINE,G4_ADIPOSE_TISSUE_ICRP,G4_AIR,G4_ALANINE,G4_ALUMINUM_OXIDE,G4_AMBER,G4_AMMONIA,G4_ANILINE,G4_ANTHRACENE,G4_B_100_BONE,G4_BAKELITE,G4_BARIUM_FLUORIDE,G4_BARIUM_SULFATE,G4_BENZENE,G4_BERYLLIUM_OXIDE,G4_BGO,G4_BLOOD_ICRP,G4_BONE_COMPACT_ICRU,G4_BONE_CORTICAL_ICRP,G4_BORON_CARBIDE,G4_BORON_OXIDE,G4_BRAIN_ICRP,G4_BUTANE,G4_N_BUTYL_ALCOHOL,G4_C_552,+152 more]
FEATURE [App::DocumentObjectGroupPython] H_element113  label="H_element : 062"  # scripted group (container) (typed FeaturePython)
  n = 1
  ref = H_element
FEATURE [App::DocumentObjectGroupPython] G4_H  # scripted group (container) (typed FeaturePython)
  Dunit = g/cm3
  Dvalue = 8.3748e-05
  Group = -> [H_element113]
  conduct = 2
  density = 1
  expand = 3
  formula = H
  name = G4_H
  specific = 4
FEATURE [App::DocumentObjectGroupPython] He_element001  label="He_element : 1"  # scripted group (container) (typed FeaturePython)
  n = 1
  ref = He_element
FEATURE [App::DocumentObjectGroupPython] G4_He  # scripted group (container) (typed FeaturePython)
  Dunit = g/cm3
  Dvalue = 0.000166322
  Group = -> [He_element001]
  conduct = 2
  density = 1
  expand = 3
  formula = He
  name = G4_He
  specific = 4
FEATURE [App::DocumentObjectGroupPython] Li_element008  label="Li_element : 008"  # scripted group (container) (typed FeaturePython)
  n = 1
  ref = Li_element
FEATURE [App::DocumentObjectGroupPython] G4_Li  # scripted group (container) (typed FeaturePython)
  Dunit = g/cm3
  Dvalue = 0.534
  Group = -> [Li_element008]
  conduct = 2
  density = 1
  expand = 3
  formula = Li
  name = G4_Li
  specific = 4
FEATURE [App::DocumentObjectGroupPython] Be_element002  label="Be_element : 002"  # scripted group (container) (typed FeaturePython)
  n = 1
  ref = Be_element
FEATURE [App::DocumentObjectGroupPython] G4_Be  # scripted group (container) (typed FeaturePython)
  Dunit = g/cm3
  Dvalue = 1.848
  Group = -> [Be_element002]
  conduct = 2
  density = 1
  expand = 3
  formula = Be
  name = G4_Be
  specific = 4
FEATURE [App::DocumentObjectGroupPython] B_element007  label="B_element : 007"  # scripted group (container) (typed FeaturePython)
  n = 1
  ref = B_element
FEATURE [App::DocumentObjectGroupPython] G4_B  # scripted group (container) (typed FeaturePython)
  Dunit = g/cm3
  Dvalue = 2.37
  Group = -> [B_element007]
  conduct = 2
  density = 1
  expand = 3
  formula = B
  name = G4_B
  specific = 4
FEATURE [App::DocumentObjectGroupPython] C_element124  label="C_element : 070"  # scripted group (container) (typed FeaturePython)
  n = 1
  ref = C_element
FEATURE [App::DocumentObjectGroupPython] G4_C  # scripted group (container) (typed FeaturePython)
  Dunit = g/cm3
  Dvalue = 2
  Group = -> [C_element124]
  conduct = 2
  density = 1
  expand = 3
  formula = C
  name = G4_C
  specific = 4
FEATURE [App::DocumentObjectGroupPython] N_element048  label="N_element : 021"  # scripted group (container) (typed FeaturePython)
  n = 1
  ref = N_element
FEATURE [App::DocumentObjectGroupPython] G4_N  # scripted group (container) (typed FeaturePython)
  Dunit = g/cm3
  Dvalue = 0.0011652
  Group = -> [N_element048]
  conduct = 2
  density = 1
  expand = 3
  formula = N
  name = G4_N
  specific = 4
FEATURE [App::DocumentObjectGroupPython] O_element105  label="O_element : 059"  # scripted group (container) (typed FeaturePython)
  n = 1
  ref = O_element
FEATURE [App::DocumentObjectGroupPython] G4_O  # scripted group (container) (typed FeaturePython)
  Dunit = g/cm3
  Dvalue = 0.00133151
  Group = -> [O_element105]
  conduct = 2
  density = 1
  expand = 3
  formula = O
  name = G4_O
  specific = 4
FEATURE [App::DocumentObjectGroupPython] F_element019  label="F_element : 008"  # scripted group (container) (typed FeaturePython)
  n = 1
  ref = F_element
FEATURE [App::DocumentObjectGroupPython] G4_F  # scripted group (container) (typed FeaturePython)
  Dunit = g/cm3
  Dvalue = 0.00158029
  Group = -> [F_element019]
  conduct = 2
  density = 1
  expand = 3
  formula = F
  name = G4_F
  specific = 4
FEATURE [App::DocumentObjectGroupPython] Ne_element001  label="Ne_element : 1"  # scripted group (container) (typed FeaturePython)
  n = 1
  ref = Ne_element
FEATURE [App::DocumentObjectGroupPython] G4_Ne  # scripted group (container) (typed FeaturePython)
  Dunit = g/cm3
  Dvalue = 0.000838505
  Group = -> [Ne_element001]
  conduct = 2
  density = 1
  expand = 3
  formula = Ne
  name = G4_Ne
  specific = 4
FEATURE [App::DocumentObjectGroupPython] Na_element020  label="Na_element : 005"  # scripted group (container) (typed FeaturePython)
  n = 1
  ref = Na_element
FEATURE [App::DocumentObjectGroupPython] G4_Na  # scripted group (container) (typed FeaturePython)
  Dunit = g/cm3
  Dvalue = 0.971
  Group = -> [Na_element020]
  conduct = 2
  density = 1
  expand = 3
  formula = Na
  name = G4_Na
  specific = 4
FEATURE [App::DocumentObjectGroupPython] Mg_element011  label="Mg_element : 005"  # scripted group (container) (typed FeaturePython)
  n = 1
  ref = Mg_element
FEATURE [App::DocumentObjectGroupPython] G4_Mg  # scripted group (container) (typed FeaturePython)
  Dunit = g/cm3
  Dvalue = 1.74
  Group = -> [Mg_element011]
  conduct = 2
  density = 1
  expand = 3
  formula = Mg
  name = G4_Mg
  specific = 4
FEATURE [App::DocumentObjectGroupPython] Al_element004  label="Al_element : 1"  # scripted group (container) (typed FeaturePython)
  n = 1
  ref = Al_element
FEATURE [App::DocumentObjectGroupPython] G4_Al  # scripted group (container) (typed FeaturePython)
  Dunit = g/cm3
  Dvalue = 2.699
  Group = -> [Al_element004]
  conduct = 2
  density = 1
  expand = 3
  formula = Al
  name = G4_Al
  specific = 4
FEATURE [App::DocumentObjectGroupPython] Si_element007  label="Si_element : 002"  # scripted group (container) (typed FeaturePython)
  n = 1
  ref = Si_element
FEATURE [App::DocumentObjectGroupPython] G4_Si  # scripted group (container) (typed FeaturePython)
  Dunit = g/cm3
  Dvalue = 2.33
  Group = -> [Si_element007]
  conduct = 2
  density = 1
  expand = 3
  formula = Si
  name = G4_Si
  specific = 4
FEATURE [App::DocumentObjectGroupPython] P_element013  label="P_element : 002"  # scripted group (container) (typed FeaturePython)
  n = 1
  ref = P_element
FEATURE [App::DocumentObjectGroupPython] G4_P  # scripted group (container) (typed FeaturePython)
  Dunit = g/cm3
  Dvalue = 2.2
  Group = -> [P_element013]
  conduct = 2
  density = 1
  expand = 3
  formula = P
  name = G4_P
  specific = 4
FEATURE [App::DocumentObjectGroupPython] S_element023  label="S_element : 007"  # scripted group (container) (typed FeaturePython)
  n = 1
  ref = S_element
FEATURE [App::DocumentObjectGroupPython] G4_S  # scripted group (container) (typed FeaturePython)
  Dunit = g/cm3
  Dvalue = 2
  Group = -> [S_element023]
  conduct = 2
  density = 1
  expand = 3
  formula = S
  name = G4_S
  specific = 4
FEATURE [App::DocumentObjectGroupPython] Cl_element029  label="Cl_element : 015"  # scripted group (container) (typed FeaturePython)
  n = 1
  ref = Cl_element
FEATURE [App::DocumentObjectGroupPython] G4_Cl  # scripted group (container) (typed FeaturePython)
  Dunit = g/cm3
  Dvalue = 0.00299473
  Group = -> [Cl_element029]
  conduct = 2
  density = 1
  expand = 3
  formula = Cl
  name = G4_Cl
  specific = 4
FEATURE [App::DocumentObjectGroupPython] Ar_element002  label="Ar_element : 1"  # scripted group (container) (typed FeaturePython)
  n = 1
  ref = Ar_element
FEATURE [App::DocumentObjectGroupPython] G4_Ar  # scripted group (container) (typed FeaturePython)
  Dunit = g/cm3
  Dvalue = 0.00166201
  Group = -> [Ar_element002]
  conduct = 2
  density = 1
  expand = 3
  formula = Ar
  name = G4_Ar
  specific = 4
FEATURE [App::DocumentObjectGroupPython] K_element013  label="K_element : 003"  # scripted group (container) (typed FeaturePython)
  n = 1
  ref = K_element
FEATURE [App::DocumentObjectGroupPython] G4_K  # scripted group (container) (typed FeaturePython)
  Dunit = g/cm3
  Dvalue = 0.862
  Group = -> [K_element013]
  conduct = 2
  density = 1
  expand = 3
  formula = K
  name = G4_K
  specific = 4
FEATURE [App::DocumentObjectGroupPython] Ca_element014  label="Ca_element : 007"  # scripted group (container) (typed FeaturePython)
  n = 1
  ref = Ca_element
FEATURE [App::DocumentObjectGroupPython] G4_Ca  # scripted group (container) (typed FeaturePython)
  Dunit = g/cm3
  Dvalue = 1.55
  Group = -> [Ca_element014]
  conduct = 2
  density = 1
  expand = 3
  formula = Ca
  name = G4_Ca
  specific = 4
FEATURE [App::DocumentObjectGroupPython] Sc_element001  label="Sc_element : 1"  # scripted group (container) (typed FeaturePython)
  n = 1
  ref = Sc_element
FEATURE [App::DocumentObjectGroupPython] G4_Sc  # scripted group (container) (typed FeaturePython)
  Dunit = g/cm3
  Dvalue = 2.989
  Group = -> [Sc_element001]
  conduct = 2
  density = 1
  expand = 3
  formula = Sc
  name = G4_Sc
  specific = 4
FEATURE [App::DocumentObjectGroupPython] Ti_element004  label="Ti_element : 002"  # scripted group (container) (typed FeaturePython)
  n = 1
  ref = Ti_element
FEATURE [App::DocumentObjectGroupPython] G4_Ti  # scripted group (container) (typed FeaturePython)
  Dunit = g/cm3
  Dvalue = 4.54
  Group = -> [Ti_element004]
  conduct = 2
  density = 1
  expand = 3
  formula = Ti
  name = G4_Ti
  specific = 4
FEATURE [App::DocumentObjectGroupPython] V_element001  label="V_element : 1"  # scripted group (container) (typed FeaturePython)
  n = 1
  ref = V_element
FEATURE [App::DocumentObjectGroupPython] G4_V  # scripted group (container) (typed FeaturePython)
  Dunit = g/cm3
  Dvalue = 6.11
  Group = -> [V_element001]
  conduct = 2
  density = 1
  expand = 3
  formula = V
  name = G4_V
  specific = 4
FEATURE [App::DocumentObjectGroupPython] Cr_element001  label="Cr_element : 1"  # scripted group (container) (typed FeaturePython)
  n = 1
  ref = Cr_element
FEATURE [App::DocumentObjectGroupPython] G4_Cr  # scripted group (container) (typed FeaturePython)
  Dunit = g/cm3
  Dvalue = 7.18
  Group = -> [Cr_element001]
  conduct = 2
  density = 1
  expand = 3
  formula = Cr
  name = G4_Cr
  specific = 4
FEATURE [App::DocumentObjectGroupPython] Mn_element001  label="Mn_element : 1"  # scripted group (container) (typed FeaturePython)
  n = 1
  ref = Mn_element
FEATURE [App::DocumentObjectGroupPython] G4_Mn  # scripted group (container) (typed FeaturePython)
  Dunit = g/cm3
  Dvalue = 7.44
  Group = -> [Mn_element001]
  conduct = 2
  density = 1
  expand = 3
  formula = Mn
  name = G4_Mn
  specific = 4
FEATURE [App::DocumentObjectGroupPython] Fe_element007  label="Fe_element : 004"  # scripted group (container) (typed FeaturePython)
  n = 1
  ref = Fe_element
FEATURE [App::DocumentObjectGroupPython] G4_Fe  # scripted group (container) (typed FeaturePython)
  Dunit = g/cm3
  Dvalue = 7.874
  Group = -> [Fe_element007]
  conduct = 2
  density = 1
  expand = 3
  formula = Fe
  name = G4_Fe
  specific = 4
FEATURE [App::DocumentObjectGroupPython] Co_element001  label="Co_element : 1"  # scripted group (container) (typed FeaturePython)
  n = 1
  ref = Co_element
FEATURE [App::DocumentObjectGroupPython] G4_Co  # scripted group (container) (typed FeaturePython)
  Dunit = g/cm3
  Dvalue = 8.9
  Group = -> [Co_element001]
  conduct = 2
  density = 1
  expand = 3
  formula = Co
  name = G4_Co
  specific = 4
FEATURE [App::DocumentObjectGroupPython] Ni_element001  label="Ni_element : 1"  # scripted group (container) (typed FeaturePython)
  n = 1
  ref = Ni_element
FEATURE [App::DocumentObjectGroupPython] G4_Ni  # scripted group (container) (typed FeaturePython)
  Dunit = g/cm3
  Dvalue = 8.902
  Group = -> [Ni_element001]
  conduct = 2
  density = 1
  expand = 3
  formula = Ni
  name = G4_Ni
  specific = 4
FEATURE [App::DocumentObjectGroupPython] Cu_element001  label="Cu_element : 1"  # scripted group (container) (typed FeaturePython)
  n = 1
  ref = Cu_element
FEATURE [App::DocumentObjectGroupPython] G4_Cu  # scripted group (container) (typed FeaturePython)
  Dunit = g/cm3
  Dvalue = 8.96
  Group = -> [Cu_element001]
  conduct = 2
  density = 1
  expand = 3
  formula = Cu
  name = G4_Cu
  specific = 4
FEATURE [App::DocumentObjectGroupPython] Zn_element001  label="Zn_element : 1"  # scripted group (container) (typed FeaturePython)
  n = 1
  ref = Zn_element
FEATURE [App::DocumentObjectGroupPython] G4_Zn  # scripted group (container) (typed FeaturePython)
  Dunit = g/cm3
  Dvalue = 7.133
  Group = -> [Zn_element001]
  conduct = 2
  density = 1
  expand = 3
  formula = Zn
  name = G4_Zn
  specific = 4
FEATURE [App::DocumentObjectGroupPython] Ga_element002  label="Ga_element : 002"  # scripted group (container) (typed FeaturePython)
  n = 1
  ref = Ga_element
FEATURE [App::DocumentObjectGroupPython] G4_Ga  # scripted group (container) (typed FeaturePython)
  Dunit = g/cm3
  Dvalue = 5.904
  Group = -> [Ga_element002]
  conduct = 2
  density = 1
  expand = 3
  formula = Ga
  name = G4_Ga
  specific = 4
FEATURE [App::DocumentObjectGroupPython] Ge_element002  label="Ge_element : 1"  # scripted group (container) (typed FeaturePython)
  n = 1
  ref = Ge_element
FEATURE [App::DocumentObjectGroupPython] G4_Ge  # scripted group (container) (typed FeaturePython)
  Dunit = g/cm3
  Dvalue = 5.323
  Group = -> [Ge_element002]
  conduct = 2
  density = 1
  expand = 3
  formula = Ge
  name = G4_Ge
  specific = 4
FEATURE [App::DocumentObjectGroupPython] As_element003  label="As_element : 002"  # scripted group (container) (typed FeaturePython)
  n = 1
  ref = As_element
FEATURE [App::DocumentObjectGroupPython] G4_As  # scripted group (container) (typed FeaturePython)
  Dunit = g/cm3
  Dvalue = 5.73
  Group = -> [As_element003]
  conduct = 2
  density = 1
  expand = 3
  formula = As
  name = G4_As
  specific = 4
FEATURE [App::DocumentObjectGroupPython] Se_element001  label="Se_element : 1"  # scripted group (container) (typed FeaturePython)
  n = 1
  ref = Se_element
FEATURE [App::DocumentObjectGroupPython] G4_Se  # scripted group (container) (typed FeaturePython)
  Dunit = g/cm3
  Dvalue = 4.5
  Group = -> [Se_element001]
  conduct = 2
  density = 1
  expand = 3
  formula = Se
  name = G4_Se
  specific = 4
FEATURE [App::DocumentObjectGroupPython] Br_element007  label="Br_element : 004"  # scripted group (container) (typed FeaturePython)
  n = 1
  ref = Br_element
FEATURE [App::DocumentObjectGroupPython] G4_Br  # scripted group (container) (typed FeaturePython)
  Dunit = g/cm3
  Dvalue = 0.0070721
  Group = -> [Br_element007]
  conduct = 2
  density = 1
  expand = 3
  formula = Br
  name = G4_Br
  specific = 4
FEATURE [App::DocumentObjectGroupPython] Kr_element001  label="Kr_element : 1"  # scripted group (container) (typed FeaturePython)
  n = 1
  ref = Kr_element
FEATURE [App::DocumentObjectGroupPython] G4_Kr  # scripted group (container) (typed FeaturePython)
  Dunit = g/cm3
  Dvalue = 0.00347832
  Group = -> [Kr_element001]
  conduct = 2
  density = 1
  expand = 3
  formula = Kr
  name = G4_Kr
  specific = 4
FEATURE [App::DocumentObjectGroupPython] Rb_element001  label="Rb_element : 1"  # scripted group (container) (typed FeaturePython)
  n = 1
  ref = Rb_element
FEATURE [App::DocumentObjectGroupPython] G4_Rb  # scripted group (container) (typed FeaturePython)
  Dunit = g/cm3
  Dvalue = 1.532
  Group = -> [Rb_element001]
  conduct = 2
  density = 1
  expand = 3
  formula = Rb
  name = G4_Rb
  specific = 4
FEATURE [App::DocumentObjectGroupPython] Sr_element001  label="Sr_element : 1"  # scripted group (container) (typed FeaturePython)
  n = 1
  ref = Sr_element
FEATURE [App::DocumentObjectGroupPython] G4_Sr  # scripted group (container) (typed FeaturePython)
  Dunit = g/cm3
  Dvalue = 2.54
  Group = -> [Sr_element001]
  conduct = 2
  density = 1
  expand = 3
  formula = Sr
  name = G4_Sr
  specific = 4
FEATURE [App::DocumentObjectGroupPython] Y_element001  label="Y_element : 1"  # scripted group (container) (typed FeaturePython)
  n = 1
  ref = Y_element
FEATURE [App::DocumentObjectGroupPython] G4_Y  # scripted group (container) (typed FeaturePython)
  Dunit = g/cm3
  Dvalue = 4.469
  Group = -> [Y_element001]
  conduct = 2
  density = 1
  expand = 3
  formula = Y
  name = G4_Y
  specific = 4
FEATURE [App::DocumentObjectGroupPython] Zr_element001  label="Zr_element : 1"  # scripted group (container) (typed FeaturePython)
  n = 1
  ref = Zr_element
FEATURE [App::DocumentObjectGroupPython] G4_Zr  # scripted group (container) (typed FeaturePython)
  Dunit = g/cm3
  Dvalue = 6.506
  Group = -> [Zr_element001]
  conduct = 2
  density = 1
  expand = 3
  formula = Zr
  name = G4_Zr
  specific = 4
FEATURE [App::DocumentObjectGroupPython] Nb_element001  label="Nb_element : 1"  # scripted group (container) (typed FeaturePython)
  n = 1
  ref = Nb_element
FEATURE [App::DocumentObjectGroupPython] G4_Nb  # scripted group (container) (typed FeaturePython)
  Dunit = g/cm3
  Dvalue = 8.57
  Group = -> [Nb_element001]
  conduct = 2
  density = 1
  expand = 3
  formula = Nb
  name = G4_Nb
  specific = 4
FEATURE [App::DocumentObjectGroupPython] Mo_element001  label="Mo_element : 1"  # scripted group (container) (typed FeaturePython)
  n = 1
  ref = Mo_element
FEATURE [App::DocumentObjectGroupPython] G4_Mo  # scripted group (container) (typed FeaturePython)
  Dunit = g/cm3
  Dvalue = 10.22
  Group = -> [Mo_element001]
  conduct = 2
  density = 1
  expand = 3
  formula = Mo
  name = G4_Mo
  specific = 4
FEATURE [App::DocumentObjectGroupPython] Tc_element001  label="Tc_element : 1"  # scripted group (container) (typed FeaturePython)
  n = 1
  ref = Tc_element
FEATURE [App::DocumentObjectGroupPython] G4_Tc  # scripted group (container) (typed FeaturePython)
  Dunit = g/cm3
  Dvalue = 11.5
  Group = -> [Tc_element001]
  conduct = 2
  density = 1
  expand = 3
  formula = Tc
  name = G4_Tc
  specific = 4
FEATURE [App::DocumentObjectGroupPython] Ru_element001  label="Ru_element : 1"  # scripted group (container) (typed FeaturePython)
  n = 1
  ref = Ru_element
FEATURE [App::DocumentObjectGroupPython] G4_Ru  # scripted group (container) (typed FeaturePython)
  Dunit = g/cm3
  Dvalue = 12.41
  Group = -> [Ru_element001]
  conduct = 2
  density = 1
  expand = 3
  formula = Ru
  name = G4_Ru
  specific = 4
FEATURE [App::DocumentObjectGroupPython] Rh_element001  label="Rh_element : 1"  # scripted group (container) (typed FeaturePython)
  n = 1
  ref = Rh_element
FEATURE [App::DocumentObjectGroupPython] G4_Rh  # scripted group (container) (typed FeaturePython)
  Dunit = g/cm3
  Dvalue = 12.41
  Group = -> [Rh_element001]
  conduct = 2
  density = 1
  expand = 3
  formula = Rh
  name = G4_Rh
  specific = 4
FEATURE [App::DocumentObjectGroupPython] Pd_element001  label="Pd_element : 1"  # scripted group (container) (typed FeaturePython)
  n = 1
  ref = Pd_element
FEATURE [App::DocumentObjectGroupPython] G4_Pd  # scripted group (container) (typed FeaturePython)
  Dunit = g/cm3
  Dvalue = 12.02
  Group = -> [Pd_element001]
  conduct = 2
  density = 1
  expand = 3
  formula = Pd
  name = G4_Pd
  specific = 4
FEATURE [App::DocumentObjectGroupPython] Ag_element006  label="Ag_element : 004"  # scripted group (container) (typed FeaturePython)
  n = 1
  ref = Ag_element
FEATURE [App::DocumentObjectGroupPython] G4_Ag  # scripted group (container) (typed FeaturePython)
  Dunit = g/cm3
  Dvalue = 10.5
  Group = -> [Ag_element006]
  conduct = 2
  density = 1
  expand = 3
  formula = Ag
  name = G4_Ag
  specific = 4
FEATURE [App::DocumentObjectGroupPython] Cd_element003  label="Cd_element : 003"  # scripted group (container) (typed FeaturePython)
  n = 1
  ref = Cd_element
FEATURE [App::DocumentObjectGroupPython] G4_Cd  # scripted group (container) (typed FeaturePython)
  Dunit = g/cm3
  Dvalue = 8.65
  Group = -> [Cd_element003]
  conduct = 2
  density = 1
  expand = 3
  formula = Cd
  name = G4_Cd
  specific = 4
FEATURE [App::DocumentObjectGroupPython] In_element001  label="In_element : 1"  # scripted group (container) (typed FeaturePython)
  n = 1
  ref = In_element
FEATURE [App::DocumentObjectGroupPython] G4_In  # scripted group (container) (typed FeaturePython)
  Dunit = g/cm3
  Dvalue = 7.31
  Group = -> [In_element001]
  conduct = 2
  density = 1
  expand = 3
  formula = In
  name = G4_In
  specific = 4
FEATURE [App::DocumentObjectGroupPython] Sn_element001  label="Sn_element : 1"  # scripted group (container) (typed FeaturePython)
  n = 1
  ref = Sn_element
FEATURE [App::DocumentObjectGroupPython] G4_Sn  # scripted group (container) (typed FeaturePython)
  Dunit = g/cm3
  Dvalue = 7.31
  Group = -> [Sn_element001]
  conduct = 2
  density = 1
  expand = 3
  formula = Sn
  name = G4_Sn
  specific = 4
FEATURE [App::DocumentObjectGroupPython] Sb_element001  label="Sb_element : 1"  # scripted group (container) (typed FeaturePython)
  n = 1
  ref = Sb_element
FEATURE [App::DocumentObjectGroupPython] G4_Sb  # scripted group (container) (typed FeaturePython)
  Dunit = g/cm3
  Dvalue = 6.691
  Group = -> [Sb_element001]
  conduct = 2
  density = 1
  expand = 3
  formula = Sb
  name = G4_Sb
  specific = 4
FEATURE [App::DocumentObjectGroupPython] Te_element002  label="Te_element : 002"  # scripted group (container) (typed FeaturePython)
  n = 1
  ref = Te_element
FEATURE [App::DocumentObjectGroupPython] G4_Te  # scripted group (container) (typed FeaturePython)
  Dunit = g/cm3
  Dvalue = 6.24
  Group = -> [Te_element002]
  conduct = 2
  density = 1
  expand = 3
  formula = Te
  name = G4_Te
  specific = 4
FEATURE [App::DocumentObjectGroupPython] I_element010  label="I_element : 006"  # scripted group (container) (typed FeaturePython)
  n = 1
  ref = I_element
FEATURE [App::DocumentObjectGroupPython] G4_I  # scripted group (container) (typed FeaturePython)
  Dunit = g/cm3
  Dvalue = 4.93
  Group = -> [I_element010]
  conduct = 2
  density = 1
  expand = 3
  formula = I
  name = G4_I
  specific = 4
FEATURE [App::DocumentObjectGroupPython] Xe_element001  label="Xe_element : 1"  # scripted group (container) (typed FeaturePython)
  n = 1
  ref = Xe_element
FEATURE [App::DocumentObjectGroupPython] G4_Xe  # scripted group (container) (typed FeaturePython)
  Dunit = g/cm3
  Dvalue = 0.00548536
  Group = -> [Xe_element001]
  conduct = 2
  density = 1
  expand = 3
  formula = Xe
  name = G4_Xe
  specific = 4
FEATURE [App::DocumentObjectGroupPython] Cs_element003  label="Cs_element : 003"  # scripted group (container) (typed FeaturePython)
  n = 1
  ref = Cs_element
FEATURE [App::DocumentObjectGroupPython] G4_Cs  # scripted group (container) (typed FeaturePython)
  Dunit = g/cm3
  Dvalue = 1.873
  Group = -> [Cs_element003]
  conduct = 2
  density = 1
  expand = 3
  formula = Cs
  name = G4_Cs
  specific = 4
FEATURE [App::DocumentObjectGroupPython] Ba_element003  label="Ba_element : 003"  # scripted group (container) (typed FeaturePython)
  n = 1
  ref = Ba_element
FEATURE [App::DocumentObjectGroupPython] G4_Ba  # scripted group (container) (typed FeaturePython)
  Dunit = g/cm3
  Dvalue = 3.5
  Group = -> [Ba_element003]
  conduct = 2
  density = 1
  expand = 3
  formula = Ba
  name = G4_Ba
  specific = 4
FEATURE [App::DocumentObjectGroupPython] La_element003  label="La_element : 003"  # scripted group (container) (typed FeaturePython)
  n = 1
  ref = La_element
FEATURE [App::DocumentObjectGroupPython] G4_La  # scripted group (container) (typed FeaturePython)
  Dunit = g/cm3
  Dvalue = 6.154
  Group = -> [La_element003]
  conduct = 2
  density = 1
  expand = 3
  formula = La
  name = G4_La
  specific = 4
FEATURE [App::DocumentObjectGroupPython] Ce_element002  label="Ce_element : 1"  # scripted group (container) (typed FeaturePython)
  n = 1
  ref = Ce_element
FEATURE [App::DocumentObjectGroupPython] G4_Ce  # scripted group (container) (typed FeaturePython)
  Dunit = g/cm3
  Dvalue = 6.657
  Group = -> [Ce_element002]
  conduct = 2
  density = 1
  expand = 3
  formula = Ce
  name = G4_Ce
  specific = 4
FEATURE [App::DocumentObjectGroupPython] Pr_element001  label="Pr_element : 1"  # scripted group (container) (typed FeaturePython)
  n = 1
  ref = Pr_element
FEATURE [App::DocumentObjectGroupPython] G4_Pr  # scripted group (container) (typed FeaturePython)
  Dunit = g/cm3
  Dvalue = 6.71
  Group = -> [Pr_element001]
  conduct = 2
  density = 1
  expand = 3
  formula = Pr
  name = G4_Pr
  specific = 4
FEATURE [App::DocumentObjectGroupPython] Nd_element001  label="Nd_element : 1"  # scripted group (container) (typed FeaturePython)
  n = 1
  ref = Nd_element
FEATURE [App::DocumentObjectGroupPython] G4_Nd  # scripted group (container) (typed FeaturePython)
  Dunit = g/cm3
  Dvalue = 6.9
  Group = -> [Nd_element001]
  conduct = 2
  density = 1
  expand = 3
  formula = Nd
  name = G4_Nd
  specific = 4
FEATURE [App::DocumentObjectGroupPython] Pm_element001  label="Pm_element : 1"  # scripted group (container) (typed FeaturePython)
  n = 1
  ref = Pm_element
FEATURE [App::DocumentObjectGroupPython] G4_Pm  # scripted group (container) (typed FeaturePython)
  Dunit = g/cm3
  Dvalue = 7.22
  Group = -> [Pm_element001]
  conduct = 2
  density = 1
  expand = 3
  formula = Pm
  name = G4_Pm
  specific = 4
FEATURE [App::DocumentObjectGroupPython] Sm_element001  label="Sm_element : 1"  # scripted group (container) (typed FeaturePython)
  n = 1
  ref = Sm_element
FEATURE [App::DocumentObjectGroupPython] G4_Sm  # scripted group (container) (typed FeaturePython)
  Dunit = g/cm3
  Dvalue = 7.46
  Group = -> [Sm_element001]
  conduct = 2
  density = 1
  expand = 3
  formula = Sm
  name = G4_Sm
  specific = 4
FEATURE [App::DocumentObjectGroupPython] Eu_element001  label="Eu_element : 1"  # scripted group (container) (typed FeaturePython)
  n = 1
  ref = Eu_element
FEATURE [App::DocumentObjectGroupPython] G4_Eu  # scripted group (container) (typed FeaturePython)
  Dunit = g/cm3
  Dvalue = 5.243
  Group = -> [Eu_element001]
  conduct = 2
  density = 1
  expand = 3
  formula = Eu
  name = G4_Eu
  specific = 4
FEATURE [App::DocumentObjectGroupPython] Gd_element002  label="Gd_element : 1"  # scripted group (container) (typed FeaturePython)
  n = 1
  ref = Gd_element
FEATURE [App::DocumentObjectGroupPython] G4_Gd  # scripted group (container) (typed FeaturePython)
  Dunit = g/cm3
  Dvalue = 7.9004
  Group = -> [Gd_element002]
  conduct = 2
  density = 1
  expand = 3
  formula = Gd
  name = G4_Gd
  specific = 4
FEATURE [App::DocumentObjectGroupPython] Tb_element001  label="Tb_element : 1"  # scripted group (container) (typed FeaturePython)
  n = 1
  ref = Tb_element
FEATURE [App::DocumentObjectGroupPython] G4_Tb  # scripted group (container) (typed FeaturePython)
  Dunit = g/cm3
  Dvalue = 8.229
  Group = -> [Tb_element001]
  conduct = 2
  density = 1
  expand = 3
  formula = Tb
  name = G4_Tb
  specific = 4
FEATURE [App::DocumentObjectGroupPython] Dy_element001  label="Dy_element : 1"  # scripted group (container) (typed FeaturePython)
  n = 1
  ref = Dy_element
FEATURE [App::DocumentObjectGroupPython] G4_Dy  # scripted group (container) (typed FeaturePython)
  Dunit = g/cm3
  Dvalue = 8.55
  Group = -> [Dy_element001]
  conduct = 2
  density = 1
  expand = 3
  formula = Dy
  name = G4_Dy
  specific = 4
FEATURE [App::DocumentObjectGroupPython] Ho_element001  label="Ho_element : 1"  # scripted group (container) (typed FeaturePython)
  n = 1
  ref = Ho_element
FEATURE [App::DocumentObjectGroupPython] G4_Ho  # scripted group (container) (typed FeaturePython)
  Dunit = g/cm3
  Dvalue = 8.795
  Group = -> [Ho_element001]
  conduct = 2
  density = 1
  expand = 3
  formula = Ho
  name = G4_Ho
  specific = 4
FEATURE [App::DocumentObjectGroupPython] Er_element001  label="Er_element : 1"  # scripted group (container) (typed FeaturePython)
  n = 1
  ref = Er_element
FEATURE [App::DocumentObjectGroupPython] G4_Er  # scripted group (container) (typed FeaturePython)
  Dunit = g/cm3
  Dvalue = 9.066
  Group = -> [Er_element001]
  conduct = 2
  density = 1
  expand = 3
  formula = Er
  name = G4_Er
  specific = 4
FEATURE [App::DocumentObjectGroupPython] Tm_element001  label="Tm_element : 1"  # scripted group (container) (typed FeaturePython)
  n = 1
  ref = Tm_element
FEATURE [App::DocumentObjectGroupPython] G4_Tm  # scripted group (container) (typed FeaturePython)
  Dunit = g/cm3
  Dvalue = 9.321
  Group = -> [Tm_element001]
  conduct = 2
  density = 1
  expand = 3
  formula = Tm
  name = G4_Tm
  specific = 4
FEATURE [App::DocumentObjectGroupPython] Yb_element001  label="Yb_element : 1"  # scripted group (container) (typed FeaturePython)
  n = 1
  ref = Yb_element
FEATURE [App::DocumentObjectGroupPython] G4_Yb  # scripted group (container) (typed FeaturePython)
  Dunit = g/cm3
  Dvalue = 6.73
  Group = -> [Yb_element001]
  conduct = 2
  density = 1
  expand = 3
  formula = Yb
  name = G4_Yb
  specific = 4
FEATURE [App::DocumentObjectGroupPython] Lu_element001  label="Lu_element : 1"  # scripted group (container) (typed FeaturePython)
  n = 1
  ref = Lu_element
FEATURE [App::DocumentObjectGroupPython] G4_Lu  # scripted group (container) (typed FeaturePython)
  Dunit = g/cm3
  Dvalue = 9.84
  Group = -> [Lu_element001]
  conduct = 2
  density = 1
  expand = 3
  formula = Lu
  name = G4_Lu
  specific = 4
FEATURE [App::DocumentObjectGroupPython] Hf_element001  label="Hf_element : 1"  # scripted group (container) (typed FeaturePython)
  n = 1
  ref = Hf_element
FEATURE [App::DocumentObjectGroupPython] G4_Hf  # scripted group (container) (typed FeaturePython)
  Dunit = g/cm3
  Dvalue = 13.31
  Group = -> [Hf_element001]
  conduct = 2
  density = 1
  expand = 3
  formula = Hf
  name = G4_Hf
  specific = 4
FEATURE [App::DocumentObjectGroupPython] Ta_element001  label="Ta_element : 1"  # scripted group (container) (typed FeaturePython)
  n = 1
  ref = Ta_element
FEATURE [App::DocumentObjectGroupPython] G4_Ta  # scripted group (container) (typed FeaturePython)
  Dunit = g/cm3
  Dvalue = 16.654
  Group = -> [Ta_element001]
  conduct = 2
  density = 1
  expand = 3
  formula = Ta
  name = G4_Ta
  specific = 4
FEATURE [App::DocumentObjectGroupPython] W_element004  label="W_element : 004"  # scripted group (container) (typed FeaturePython)
  n = 1
  ref = W_element
FEATURE [App::DocumentObjectGroupPython] G4_W  # scripted group (container) (typed FeaturePython)
  Dunit = g/cm3
  Dvalue = 19.3
  Group = -> [W_element004]
  conduct = 2
  density = 1
  expand = 3
  formula = W
  name = G4_W
  specific = 4
FEATURE [App::DocumentObjectGroupPython] Re_element001  label="Re_element : 1"  # scripted group (container) (typed FeaturePython)
  n = 1
  ref = Re_element
FEATURE [App::DocumentObjectGroupPython] G4_Re  # scripted group (container) (typed FeaturePython)
  Dunit = g/cm3
  Dvalue = 21.02
  Group = -> [Re_element001]
  conduct = 2
  density = 1
  expand = 3
  formula = Re
  name = G4_Re
  specific = 4
FEATURE [App::DocumentObjectGroupPython] Os_element001  label="Os_element : 1"  # scripted group (container) (typed FeaturePython)
  n = 1
  ref = Os_element
FEATURE [App::DocumentObjectGroupPython] G4_Os  # scripted group (container) (typed FeaturePython)
  Dunit = g/cm3
  Dvalue = 22.57
  Group = -> [Os_element001]
  conduct = 2
  density = 1
  expand = 3
  formula = Os
  name = G4_Os
  specific = 4
FEATURE [App::DocumentObjectGroupPython] Ir_element001  label="Ir_element : 1"  # scripted group (container) (typed FeaturePython)
  n = 1
  ref = Ir_element
FEATURE [App::DocumentObjectGroupPython] G4_Ir  # scripted group (container) (typed FeaturePython)
  Dunit = g/cm3
  Dvalue = 22.42
  Group = -> [Ir_element001]
  conduct = 2
  density = 1
  expand = 3
  formula = Ir
  name = G4_Ir
  specific = 4
FEATURE [App::DocumentObjectGroupPython] Pt_element001  label="Pt_element : 1"  # scripted group (container) (typed FeaturePython)
  n = 1
  ref = Pt_element
FEATURE [App::DocumentObjectGroupPython] G4_Pt  # scripted group (container) (typed FeaturePython)
  Dunit = g/cm3
  Dvalue = 21.45
  Group = -> [Pt_element001]
  conduct = 2
  density = 1
  expand = 3
  formula = Pt
  name = G4_Pt
  specific = 4
FEATURE [App::DocumentObjectGroupPython] Au_element001  label="Au_element : 1"  # scripted group (container) (typed FeaturePython)
  n = 1
  ref = Au_element
FEATURE [App::DocumentObjectGroupPython] G4_Au  # scripted group (container) (typed FeaturePython)
  Dunit = g/cm3
  Dvalue = 19.32
  Group = -> [Au_element001]
  conduct = 2
  density = 1
  expand = 3
  formula = Au
  name = G4_Au
  specific = 4
FEATURE [App::DocumentObjectGroupPython] Hg_element002  label="Hg_element : 002"  # scripted group (container) (typed FeaturePython)
  n = 1
  ref = Hg_element
FEATURE [App::DocumentObjectGroupPython] G4_Hg  # scripted group (container) (typed FeaturePython)
  Dunit = g/cm3
  Dvalue = 13.546
  Group = -> [Hg_element002]
  conduct = 2
  density = 1
  expand = 3
  formula = Hg
  name = G4_Hg
  specific = 4
FEATURE [App::DocumentObjectGroupPython] Tl_element002  label="Tl_element : 002"  # scripted group (container) (typed FeaturePython)
  n = 1
  ref = Tl_element
FEATURE [App::DocumentObjectGroupPython] G4_Tl  # scripted group (container) (typed FeaturePython)
  Dunit = g/cm3
  Dvalue = 11.72
  Group = -> [Tl_element002]
  conduct = 2
  density = 1
  expand = 3
  formula = Tl
  name = G4_Tl
  specific = 4
FEATURE [App::DocumentObjectGroupPython] Pb_element003  label="Pb_element : 1"  # scripted group (container) (typed FeaturePython)
  n = 1
  ref = Pb_element
FEATURE [App::DocumentObjectGroupPython] G4_Pb  # scripted group (container) (typed FeaturePython)
  Dunit = g/cm3
  Dvalue = 11.35
  Group = -> [Pb_element003]
  conduct = 2
  density = 1
  expand = 3
  formula = Pb
  name = G4_Pb
  specific = 4
FEATURE [App::DocumentObjectGroupPython] Bi_element002  label="Bi_element : 1"  # scripted group (container) (typed FeaturePython)
  n = 1
  ref = Bi_element
FEATURE [App::DocumentObjectGroupPython] G4_Bi  # scripted group (container) (typed FeaturePython)
  Dunit = g/cm3
  Dvalue = 9.747
  Group = -> [Bi_element002]
  conduct = 2
  density = 1
  expand = 3
  formula = Bi
  name = G4_Bi
  specific = 4
FEATURE [App::DocumentObjectGroupPython] Po_element001  label="Po_element : 1"  # scripted group (container) (typed FeaturePython)
  n = 1
  ref = Po_element
FEATURE [App::DocumentObjectGroupPython] G4_Po  # scripted group (container) (typed FeaturePython)
  Dunit = g/cm3
  Dvalue = 9.32
  Group = -> [Po_element001]
  conduct = 2
  density = 1
  expand = 3
  formula = Po
  name = G4_Po
  specific = 4
FEATURE [App::DocumentObjectGroupPython] At_element001  label="At_element : 1"  # scripted group (container) (typed FeaturePython)
  n = 1
  ref = At_element
FEATURE [App::DocumentObjectGroupPython] G4_At  # scripted group (container) (typed FeaturePython)
  Dunit = g/cm3
  Dvalue = 9.32
  Group = -> [At_element001]
  conduct = 2
  density = 1
  expand = 3
  formula = At
  name = G4_At
  specific = 4
FEATURE [App::DocumentObjectGroupPython] Rn_element001  label="Rn_element : 1"  # scripted group (container) (typed FeaturePython)
  n = 1
  ref = Rn_element
FEATURE [App::DocumentObjectGroupPython] G4_Rn  # scripted group (container) (typed FeaturePython)
  Dunit = g/cm3
  Dvalue = 0.00900662
  Group = -> [Rn_element001]
  conduct = 2
  density = 1
  expand = 3
  formula = Rn
  name = G4_Rn
  specific = 4
FEATURE [App::DocumentObjectGroupPython] Fr_element001  label="Fr_element : 1"  # scripted group (container) (typed FeaturePython)
  n = 1
  ref = Fr_element
FEATURE [App::DocumentObjectGroupPython] G4_Fr  # scripted group (container) (typed FeaturePython)
  Dunit = g/cm3
  Dvalue = 1
  Group = -> [Fr_element001]
  conduct = 2
  density = 1
  expand = 3
  formula = Fr
  name = G4_Fr
  specific = 4
FEATURE [App::DocumentObjectGroupPython] Ra_element001  label="Ra_element : 1"  # scripted group (container) (typed FeaturePython)
  n = 1
  ref = Ra_element
FEATURE [App::DocumentObjectGroupPython] G4_Ra  # scripted group (container) (typed FeaturePython)
  Dunit = g/cm3
  Dvalue = 5
  Group = -> [Ra_element001]
  conduct = 2
  density = 1
  expand = 3
  formula = Ra
  name = G4_Ra
  specific = 4
FEATURE [App::DocumentObjectGroupPython] Ac_element001  label="Ac_element : 1"  # scripted group (container) (typed FeaturePython)
  n = 1
  ref = Ac_element
FEATURE [App::DocumentObjectGroupPython] G4_Ac  # scripted group (container) (typed FeaturePython)
  Dunit = g/cm3
  Dvalue = 10.07
  Group = -> [Ac_element001]
  conduct = 2
  density = 1
  expand = 3
  formula = Ac
  name = G4_Ac
  specific = 4
FEATURE [App::DocumentObjectGroupPython] Th_element001  label="Th_element : 1"  # scripted group (container) (typed FeaturePython)
  n = 1
  ref = Th_element
FEATURE [App::DocumentObjectGroupPython] G4_Th  # scripted group (container) (typed FeaturePython)
  Dunit = g/cm3
  Dvalue = 11.72
  Group = -> [Th_element001]
  conduct = 2
  density = 1
  expand = 3
  formula = Th
  name = G4_Th
  specific = 4
FEATURE [App::DocumentObjectGroupPython] Pa_element001  label="Pa_element : 1"  # scripted group (container) (typed FeaturePython)
  n = 1
  ref = Pa_element
FEATURE [App::DocumentObjectGroupPython] G4_Pa  # scripted group (container) (typed FeaturePython)
  Dunit = g/cm3
  Dvalue = 15.37
  Group = -> [Pa_element001]
  conduct = 2
  density = 1
  expand = 3
  formula = Pa
  name = G4_Pa
  specific = 4
FEATURE [App::DocumentObjectGroupPython] U_element004  label="U_element : 004"  # scripted group (container) (typed FeaturePython)
  n = 1
  ref = U_element
FEATURE [App::DocumentObjectGroupPython] G4_U  # scripted group (container) (typed FeaturePython)
  Dunit = g/cm3
  Dvalue = 18.95
  Group = -> [U_element004]
  conduct = 2
  density = 1
  expand = 3
  formula = U
  name = G4_U
  specific = 4
FEATURE [App::DocumentObjectGroupPython] Np_element001  label="Np_element : 1"  # scripted group (container) (typed FeaturePython)
  n = 1
  ref = Np_element
FEATURE [App::DocumentObjectGroupPython] G4_Np  # scripted group (container) (typed FeaturePython)
  Dunit = g/cm3
  Dvalue = 20.25
  Group = -> [Np_element001]
  conduct = 2
  density = 1
  expand = 3
  formula = Np
  name = G4_Np
  specific = 4
FEATURE [App::DocumentObjectGroupPython] Pu_element002  label="Pu_element : 002"  # scripted group (container) (typed FeaturePython)
  n = 1
  ref = Pu_element
FEATURE [App::DocumentObjectGroupPython] G4_Pu  # scripted group (container) (typed FeaturePython)
  Dunit = g/cm3
  Dvalue = 19.84
  Group = -> [Pu_element002]
  conduct = 2
  density = 1
  expand = 3
  formula = Pu
  name = G4_Pu
  specific = 4
FEATURE [App::DocumentObjectGroupPython] Am_element001  label="Am_element : 1"  # scripted group (container) (typed FeaturePython)
  n = 1
  ref = Am_element
FEATURE [App::DocumentObjectGroupPython] G4_Am  # scripted group (container) (typed FeaturePython)
  Dunit = g/cm3
  Dvalue = 13.67
  Group = -> [Am_element001]
  conduct = 2
  density = 1
  expand = 3
  formula = Am
  name = G4_Am
  specific = 4
FEATURE [App::DocumentObjectGroupPython] Cm_element001  label="Cm_element : 1"  # scripted group (container) (typed FeaturePython)
  n = 1
  ref = Cm_element
FEATURE [App::DocumentObjectGroupPython] G4_Cm  # scripted group (container) (typed FeaturePython)
  Dunit = g/cm3
  Dvalue = 13.51
  Group = -> [Cm_element001]
  conduct = 2
  density = 1
  expand = 3
  formula = Cm
  name = G4_Cm
  specific = 4
FEATURE [App::DocumentObjectGroupPython] Bk_element001  label="Bk_element : 1"  # scripted group (container) (typed FeaturePython)
  n = 1
  ref = Bk_element
FEATURE [App::DocumentObjectGroupPython] G4_Bk  # scripted group (container) (typed FeaturePython)
  Dunit = g/cm3
  Dvalue = 14
  Group = -> [Bk_element001]
  conduct = 2
  density = 1
  expand = 3
  formula = Bk
  name = G4_Bk
  specific = 4
FEATURE [App::DocumentObjectGroupPython] Cf_element001  label="Cf_element : 1"  # scripted group (container) (typed FeaturePython)
  n = 1
  ref = Cf_element
FEATURE [App::DocumentObjectGroupPython] G4_Cf  # scripted group (container) (typed FeaturePython)
  Dunit = g/cm3
  Dvalue = 10
  Group = -> [Cf_element001]
  conduct = 2
  density = 1
  expand = 3
  formula = Cf
  name = G4_Cf
  specific = 4
FEATURE [App::DocumentObjectGroupPython] Element  # scripted group (container) (typed FeaturePython)
  Group = -> [G4_H,G4_He,G4_Li,G4_Be,G4_B,G4_C,G4_N,G4_O,G4_F,G4_Ne,G4_Na,G4_Mg,G4_Al,G4_Si,G4_P,G4_S,G4_Cl,G4_Ar,G4_K,G4_Ca,G4_Sc,G4_Ti,G4_V,G4_Cr,G4_Mn,G4_Fe,G4_Co,G4_Ni,G4_Cu,G4_Zn,G4_Ga,G4_Ge,G4_As,G4_Se,G4_Br,G4_Kr,G4_Rb,G4_Sr,G4_Y,G4_Zr,G4_Nb,G4_Mo,G4_Tc,G4_Ru,G4_Rh,G4_Pd,G4_Ag,G4_Cd,G4_In,G4_Sn,G4_Sb,G4_Te,G4_I,G4_Xe,G4_Cs,G4_Ba,G4_La,G4_Ce,G4_Pr,G4_Nd,G4_Pm,G4_Sm,G4_Eu,G4_Gd,G4_Tb,G4_Dy,G4_Ho,G4_Er,+30 more]
FEATURE [App::DocumentObjectGroupPython] H_element114  label="H_element : 063"  # scripted group (container) (typed FeaturePython)
  n = 2
  ref = H_element
FEATURE [App::DocumentObjectGroupPython] G4_lH2  # scripted group (container) (typed FeaturePython)
  Dunit = g/cm3
  Dvalue = 0.0708
  Group = -> [H_element114]
  conduct = 2
  density = 1
  expand = 3
  formula = G4_lH2
  name = G4_lH2
  specific = 4
FEATURE [App::DocumentObjectGroupPython] N_element049  label="N_element : 022"  # scripted group (container) (typed FeaturePython)
  n = 2
  ref = N_element
FEATURE [App::DocumentObjectGroupPython] G4_lN2  # scripted group (container) (typed FeaturePython)
  Dunit = g/cm3
  Dvalue = 0.807
  Group = -> [N_element049]
  conduct = 2
  density = 1
  expand = 3
  formula = G4_lN2
  name = G4_lN2
  specific = 4
FEATURE [App::DocumentObjectGroupPython] O_element106  label="O_element : 060"  # scripted group (container) (typed FeaturePython)
  n = 2
  ref = O_element
FEATURE [App::DocumentObjectGroupPython] G4_lO2  # scripted group (container) (typed FeaturePython)
  Dunit = g/cm3
  Dvalue = 1.141
  Group = -> [O_element106]
  conduct = 2
  density = 1
  expand = 3
  formula = G4_lO2
  name = G4_lO2
  specific = 4
FEATURE [App::DocumentObjectGroupPython] Ar  label="Ar : 1"  # scripted group (container) (typed FeaturePython)
  n = 1
  ref = Ar
FEATURE [App::DocumentObjectGroupPython] G4_lAr  # scripted group (container) (typed FeaturePython)
  Dunit = g/cm3
  Dvalue = 1.396
  Group = -> [Ar]
  conduct = 2
  density = 1
  expand = 3
  formula = G4_lAr
  name = G4_lAr
  specific = 4
FEATURE [App::DocumentObjectGroupPython] Br  label="Br : 1"  # scripted group (container) (typed FeaturePython)
  n = 1
  ref = Br
FEATURE [App::DocumentObjectGroupPython] G4_lBr  # scripted group (container) (typed FeaturePython)
  Dunit = g/cm3
  Dvalue = 3.1028
  Group = -> [Br]
  conduct = 2
  density = 1
  expand = 3
  formula = G4_lBr
  name = G4_lBr
  specific = 4
FEATURE [App::DocumentObjectGroupPython] Kr  label="Kr : 1"  # scripted group (container) (typed FeaturePython)
  n = 1
  ref = Kr
FEATURE [App::DocumentObjectGroupPython] G4_lKr  # scripted group (container) (typed FeaturePython)
  Dunit = g/cm3
  Dvalue = 2.418
  Group = -> [Kr]
  conduct = 2
  density = 1
  expand = 3
  formula = G4_lKr
  name = G4_lKr
  specific = 4
FEATURE [App::DocumentObjectGroupPython] Xe  label="Xe : 1"  # scripted group (container) (typed FeaturePython)
  n = 1
  ref = Xe
FEATURE [App::DocumentObjectGroupPython] G4_lXe  # scripted group (container) (typed FeaturePython)
  Dunit = g/cm3
  Dvalue = 2.953
  Group = -> [Xe]
  conduct = 2
  density = 1
  expand = 3
  formula = G4_lXe
  name = G4_lXe
  specific = 4
FEATURE [App::DocumentObjectGroupPython] O_element107  label="O_element : 061"  # scripted group (container) (typed FeaturePython)
  n = 4
  ref = O_element
FEATURE [App::DocumentObjectGroupPython] Pb_element004  label="Pb_element : 002"  # scripted group (container) (typed FeaturePython)
  n = 1
  ref = Pb_element
FEATURE [App::DocumentObjectGroupPython] W_element005  label="W_element : 005"  # scripted group (container) (typed FeaturePython)
  n = 1
  ref = W_element
FEATURE [App::DocumentObjectGroupPython] G4_PbWO4  # scripted group (container) (typed FeaturePython)
  Dunit = g/cm3
  Dvalue = 8.28
  Group = -> [O_element107,Pb_element004,W_element005]
  conduct = 2
  density = 1
  expand = 3
  formula = G4_PbWO4
  name = G4_PbWO4
  specific = 4
FEATURE [App::DocumentObjectGroupPython] alactic  label="alactic : 1"  # scripted group (container) (typed FeaturePython)
  n = 1
  ref = alactic
FEATURE [App::DocumentObjectGroupPython] G4_Galactic  # scripted group (container) (typed FeaturePython)
  Dunit = g/cm3
  Dvalue = 0
  Group = -> [alactic]
  conduct = 2
  density = 1
  expand = 3
  formula = G4_Galactic
  name = G4_Galactic
  specific = 4
FEATURE [App::DocumentObjectGroupPython] RAPHITE_POROUS  label="RAPHITE_POROUS : 1"  # scripted group (container) (typed FeaturePython)
  n = 1
  ref = RAPHITE_POROUS
FEATURE [App::DocumentObjectGroupPython] G4_GRAPHITE_POROUS  # scripted group (container) (typed FeaturePython)
  Dunit = g/cm3
  Dvalue = 1.7
  Group = -> [RAPHITE_POROUS]
  conduct = 2
  density = 1
  expand = 3
  formula = G4_GRAPHITE_POROUS
  name = G4_GRAPHITE_POROUS
  specific = 4
FEATURE [App::DocumentObjectGroupPython] H_element115  label="H_element : 0.150"  # scripted group (container) (typed FeaturePython)
  n = 0.080538
FEATURE [App::DocumentObjectGroupPython] C_element125  label="C_element : 0.600"  # scripted group (container) (typed FeaturePython)
  n = 0.599848
FEATURE [App::DocumentObjectGroupPython] O_element108  label="O_element : 0.320"  # scripted group (container) (typed FeaturePython)
  n = 0.319614
FEATURE [App::DocumentObjectGroupPython] G4_LUCITE  # scripted group (container) (typed FeaturePython)
  Dunit = g/cm3
  Dvalue = 1.19
  Group = -> [H_element115,C_element125,O_element108]
  conduct = 2
  density = 1
  expand = 3
  formula = G4_LUCITE
  name = G4_LUCITE
  specific = 4
FEATURE [App::DocumentObjectGroupPython] Cu_element002  label="Cu_element : 62"  # scripted group (container) (typed FeaturePython)
  n = 62
  ref = Cu_element
FEATURE [App::DocumentObjectGroupPython] Zn_element002  label="Zn_element : 35"  # scripted group (container) (typed FeaturePython)
  n = 35
  ref = Zn_element
FEATURE [App::DocumentObjectGroupPython] Pb_element005  label="Pb_element : 3"  # scripted group (container) (typed FeaturePython)
  n = 3
  ref = Pb_element
FEATURE [App::DocumentObjectGroupPython] G4_BRASS  # scripted group (container) (typed FeaturePython)
  Dunit = g/cm3
  Dvalue = 8.52
  Group = -> [Cu_element002,Zn_element002,Pb_element005]
  conduct = 2
  density = 1
  expand = 3
  formula = G4_BRASS
  name = G4_BRASS
  specific = 4
FEATURE [App::DocumentObjectGroupPython] Cu_element003  label="Cu_element : 89"  # scripted group (container) (typed FeaturePython)
  n = 89
  ref = Cu_element
FEATURE [App::DocumentObjectGroupPython] Zn_element003  label="Zn_element : 9"  # scripted group (container) (typed FeaturePython)
  n = 9
  ref = Zn_element
FEATURE [App::DocumentObjectGroupPython] Pb_element006  label="Pb_element : 2"  # scripted group (container) (typed FeaturePython)
  n = 2
  ref = Pb_element
FEATURE [App::DocumentObjectGroupPython] G4_BRONZE  # scripted group (container) (typed FeaturePython)
  Dunit = g/cm3
  Dvalue = 8.82
  Group = -> [Cu_element003,Zn_element003,Pb_element006]
  conduct = 2
  density = 1
  expand = 3
  formula = G4_BRONZE
  name = G4_BRONZE
  specific = 4
FEATURE [App::DocumentObjectGroupPython] Fe_element008  label="Fe_element : 74"  # scripted group (container) (typed FeaturePython)
  n = 74
  ref = Fe_element
FEATURE [App::DocumentObjectGroupPython] Cr_element002  label="Cr_element : 18"  # scripted group (container) (typed FeaturePython)
  n = 18
  ref = Cr_element
FEATURE [App::DocumentObjectGroupPython] Ni_element002  label="Ni_element : 8"  # scripted group (container) (typed FeaturePython)
  n = 8
  ref = Ni_element
FEATURE [App::DocumentObjectGroupPython] G4_STAINLESS_STEEL  label="G4_STAINLESS-STEEL"  # scripted group (container) (typed FeaturePython)
  Dunit = g/cm3
  Dvalue = 8
  Group = -> [Fe_element008,Cr_element002,Ni_element002]
  conduct = 2
  density = 1
  expand = 3
  formula = G4_STAINLESS-STEEL
  name = G4_STAINLESS-STEEL
  specific = 4
FEATURE [App::DocumentObjectGroupPython] H_element116  label="H_element : 064"  # scripted group (container) (typed FeaturePython)
  n = 18
  ref = H_element
FEATURE [App::DocumentObjectGroupPython] C_element126  label="C_element : 071"  # scripted group (container) (typed FeaturePython)
  n = 12
  ref = C_element
FEATURE [App::DocumentObjectGroupPython] O_element109  label="O_element : 062"  # scripted group (container) (typed FeaturePython)
  n = 7
  ref = O_element
FEATURE [App::DocumentObjectGroupPython] G4_CR39  # scripted group (container) (typed FeaturePython)
  Dunit = g/cm3
  Dvalue = 1.32
  Group = -> [H_element116,C_element126,O_element109]
  conduct = 2
  density = 1
  expand = 3
  formula = G4_CR39
  name = G4_CR39
  specific = 4
FEATURE [App::DocumentObjectGroupPython] H_element117  label="H_element : 38"  # scripted group (container) (typed FeaturePython)
  n = 38
  ref = H_element
FEATURE [App::DocumentObjectGroupPython] C_element127  label="C_element : 072"  # scripted group (container) (typed FeaturePython)
  n = 18
  ref = C_element
FEATURE [App::DocumentObjectGroupPython] O_element110  label="O_element : 063"  # scripted group (container) (typed FeaturePython)
  n = 1
  ref = O_element
FEATURE [App::DocumentObjectGroupPython] G4_OCTADECANOL  # scripted group (container) (typed FeaturePython)
  Dunit = g/cm3
  Dvalue = 0.812
  Group = -> [H_element117,C_element127,O_element110]
  conduct = 2
  density = 1
  expand = 3
  formula = G4_OCTADECANOL
  name = G4_OCTADECANOL
  specific = 4
FEATURE [App::DocumentObjectGroupPython] HEP  # scripted group (container) (typed FeaturePython)
  Group = -> [G4_lH2,G4_lN2,G4_lO2,G4_lAr,G4_lBr,G4_lKr,G4_lXe,G4_PbWO4,G4_Galactic,G4_GRAPHITE_POROUS,G4_LUCITE,G4_BRASS,G4_BRONZE,G4_STAINLESS_STEEL,G4_CR39,G4_OCTADECANOL]
FEATURE [App::DocumentObjectGroupPython] C_element128  label="C_element : 073"  # scripted group (container) (typed FeaturePython)
  n = 14
  ref = C_element
FEATURE [App::DocumentObjectGroupPython] H_element118  label="H_element : 065"  # scripted group (container) (typed FeaturePython)
  n = 10
  ref = H_element
FEATURE [App::DocumentObjectGroupPython] O_element111  label="O_element : 064"  # scripted group (container) (typed FeaturePython)
  n = 2
  ref = O_element
FEATURE [App::DocumentObjectGroupPython] N_element050  label="N_element : 023"  # scripted group (container) (typed FeaturePython)
  n = 2
  ref = N_element
FEATURE [App::DocumentObjectGroupPython] G4_KEVLAR  # scripted group (container) (typed FeaturePython)
  Dunit = g/cm3
  Dvalue = 1.44
  Group = -> [C_element128,H_element118,O_element111,N_element050]
  conduct = 2
  density = 1
  expand = 3
  formula = G4_KEVLAR
  name = G4_KEVLAR
  specific = 4
FEATURE [App::DocumentObjectGroupPython] C_element129  label="C_element : 074"  # scripted group (container) (typed FeaturePython)
  n = 10
  ref = C_element
FEATURE [App::DocumentObjectGroupPython] H_element119  label="H_element : 066"  # scripted group (container) (typed FeaturePython)
  n = 8
  ref = H_element
FEATURE [App::DocumentObjectGroupPython] O_element112  label="O_element : 065"  # scripted group (container) (typed FeaturePython)
  n = 4
  ref = O_element
FEATURE [App::DocumentObjectGroupPython] G4_DACRON  # scripted group (container) (typed FeaturePython)
  Dunit = g/cm3
  Dvalue = 1.4
  Group = -> [C_element129,H_element119,O_element112]
  conduct = 2
  density = 1
  expand = 3
  formula = G4_DACRON
  name = G4_DACRON
  specific = 4
FEATURE [App::DocumentObjectGroupPython] C_element130  label="C_element : 075"  # scripted group (container) (typed FeaturePython)
  n = 4
  ref = C_element
FEATURE [App::DocumentObjectGroupPython] H_element120  label="H_element : 067"  # scripted group (container) (typed FeaturePython)
  n = 5
  ref = H_element
FEATURE [App::DocumentObjectGroupPython] Cl_element030  label="Cl_element : 016"  # scripted group (container) (typed FeaturePython)
  n = 1
  ref = Cl_element
FEATURE [App::DocumentObjectGroupPython] G4_NEOPRENE  # scripted group (container) (typed FeaturePython)
  Dunit = g/cm3
  Dvalue = 1.23
  Group = -> [C_element130,H_element120,Cl_element030]
  conduct = 2
  density = 1
  expand = 3
  formula = G4_NEOPRENE
  name = G4_NEOPRENE
  specific = 4
FEATURE [App::DocumentObjectGroupPython] Space  # scripted group (container) (typed FeaturePython)
  Group = -> [G4_KEVLAR,G4_DACRON,G4_NEOPRENE]
FEATURE [App::DocumentObjectGroupPython] H_element121  label="H_element : 068"  # scripted group (container) (typed FeaturePython)
  n = 5
  ref = H_element
FEATURE [App::DocumentObjectGroupPython] C_element131  label="C_element : 076"  # scripted group (container) (typed FeaturePython)
  n = 4
  ref = C_element
FEATURE [App::DocumentObjectGroupPython] N_element051  label="N_element : 3"  # scripted group (container) (typed FeaturePython)
  n = 3
  ref = N_element
FEATURE [App::DocumentObjectGroupPython] O_element113  label="O_element : 066"  # scripted group (container) (typed FeaturePython)
  n = 1
  ref = O_element
FEATURE [App::DocumentObjectGroupPython] G4_CYTOSINE  # scripted group (container) (typed FeaturePython)
  Dunit = g/cm3
  Dvalue = 1.55
  Group = -> [H_element121,C_element131,N_element051,O_element113]
  conduct = 2
  density = 1
  expand = 3
  formula = G4_CYTOSINE
  name = G4_CYTOSINE
  specific = 4
FEATURE [App::DocumentObjectGroupPython] H_element122  label="H_element : 069"  # scripted group (container) (typed FeaturePython)
  n = 6
  ref = H_element
FEATURE [App::DocumentObjectGroupPython] C_element132  label="C_element : 077"  # scripted group (container) (typed FeaturePython)
  n = 5
  ref = C_element
FEATURE [App::DocumentObjectGroupPython] N_element052  label="N_element : 024"  # scripted group (container) (typed FeaturePython)
  n = 2
  ref = N_element
FEATURE [App::DocumentObjectGroupPython] O_element114  label="O_element : 067"  # scripted group (container) (typed FeaturePython)
  n = 2
  ref = O_element
FEATURE [App::DocumentObjectGroupPython] G4_THYMINE  # scripted group (container) (typed FeaturePython)
  Dunit = g/cm3
  Dvalue = 1.23
  Group = -> [H_element122,C_element132,N_element052,O_element114]
  conduct = 2
  density = 1
  expand = 3
  formula = G4_THYMINE
  name = G4_THYMINE
  specific = 4
FEATURE [App::DocumentObjectGroupPython] H_element123  label="H_element : 070"  # scripted group (container) (typed FeaturePython)
  n = 4
  ref = H_element
FEATURE [App::DocumentObjectGroupPython] C_element133  label="C_element : 078"  # scripted group (container) (typed FeaturePython)
  n = 4
  ref = C_element
FEATURE [App::DocumentObjectGroupPython] N_element053  label="N_element : 025"  # scripted group (container) (typed FeaturePython)
  n = 2
  ref = N_element
FEATURE [App::DocumentObjectGroupPython] O_element115  label="O_element : 068"  # scripted group (container) (typed FeaturePython)
  n = 2
  ref = O_element
FEATURE [App::DocumentObjectGroupPython] G4_URACIL  # scripted group (container) (typed FeaturePython)
  Dunit = g/cm3
  Dvalue = 1.32
  Group = -> [H_element123,C_element133,N_element053,O_element115]
  conduct = 2
  density = 1
  expand = 3
  formula = G4_URACIL
  name = G4_URACIL
  specific = 4
FEATURE [App::DocumentObjectGroupPython] H_element124  label="H_element : 071"  # scripted group (container) (typed FeaturePython)
  n = 4
  ref = H_element
FEATURE [App::DocumentObjectGroupPython] C_element134  label="C_element : 079"  # scripted group (container) (typed FeaturePython)
  n = 5
  ref = C_element
FEATURE [App::DocumentObjectGroupPython] N_element054  label="N_element : 026"  # scripted group (container) (typed FeaturePython)
  n = 5
  ref = N_element
FEATURE [App::DocumentObjectGroupPython] G4_DNA_ADENINE  # scripted group (container) (typed FeaturePython)
  Dunit = g/cm3
  Dvalue = 1
  Group = -> [H_element124,C_element134,N_element054]
  conduct = 2
  density = 1
  expand = 3
  formula = G4_DNA_ADENINE
  name = G4_DNA_ADENINE
  specific = 4
FEATURE [App::DocumentObjectGroupPython] H_element125  label="H_element : 072"  # scripted group (container) (typed FeaturePython)
  n = 4
  ref = H_element
FEATURE [App::DocumentObjectGroupPython] C_element135  label="C_element : 080"  # scripted group (container) (typed FeaturePython)
  n = 5
  ref = C_element
FEATURE [App::DocumentObjectGroupPython] N_element055  label="N_element : 027"  # scripted group (container) (typed FeaturePython)
  n = 5
  ref = N_element
FEATURE [App::DocumentObjectGroupPython] O_element116  label="O_element : 069"  # scripted group (container) (typed FeaturePython)
  n = 1
  ref = O_element
FEATURE [App::DocumentObjectGroupPython] G4_DNA_GUANINE  # scripted group (container) (typed FeaturePython)
  Dunit = g/cm3
  Dvalue = 1
  Group = -> [H_element125,C_element135,N_element055,O_element116]
  conduct = 2
  density = 1
  expand = 3
  formula = G4_DNA_GUANINE
  name = G4_DNA_GUANINE
  specific = 4
FEATURE [App::DocumentObjectGroupPython] H_element126  label="H_element : 073"  # scripted group (container) (typed FeaturePython)
  n = 4
  ref = H_element
FEATURE [App::DocumentObjectGroupPython] C_element136  label="C_element : 081"  # scripted group (container) (typed FeaturePython)
  n = 4
  ref = C_element
FEATURE [App::DocumentObjectGroupPython] N_element056  label="N_element : 028"  # scripted group (container) (typed FeaturePython)
  n = 3
  ref = N_element
FEATURE [App::DocumentObjectGroupPython] O_element117  label="O_element : 070"  # scripted group (container) (typed FeaturePython)
  n = 1
  ref = O_element
FEATURE [App::DocumentObjectGroupPython] G4_DNA_CYTOSINE  # scripted group (container) (typed FeaturePython)
  Dunit = g/cm3
  Dvalue = 1
  Group = -> [H_element126,C_element136,N_element056,O_element117]
  conduct = 2
  density = 1
  expand = 3
  formula = G4_DNA_CYTOSINE
  name = G4_DNA_CYTOSINE
  specific = 4
FEATURE [App::DocumentObjectGroupPython] H_element127  label="H_element : 074"  # scripted group (container) (typed FeaturePython)
  n = 5
  ref = H_element
FEATURE [App::DocumentObjectGroupPython] C_element137  label="C_element : 082"  # scripted group (container) (typed FeaturePython)
  n = 5
  ref = C_element
FEATURE [App::DocumentObjectGroupPython] N_element057  label="N_element : 029"  # scripted group (container) (typed FeaturePython)
  n = 2
  ref = N_element
FEATURE [App::DocumentObjectGroupPython] O_element118  label="O_element : 071"  # scripted group (container) (typed FeaturePython)
  n = 2
  ref = O_element
FEATURE [App::DocumentObjectGroupPython] G4_DNA_THYMINE  # scripted group (container) (typed FeaturePython)
  Dunit = g/cm3
  Dvalue = 1
  Group = -> [H_element127,C_element137,N_element057,O_element118]
  conduct = 2
  density = 1
  expand = 3
  formula = G4_DNA_THYMINE
  name = G4_DNA_THYMINE
  specific = 4
FEATURE [App::DocumentObjectGroupPython] H_element128  label="H_element : 075"  # scripted group (container) (typed FeaturePython)
  n = 3
  ref = H_element
FEATURE [App::DocumentObjectGroupPython] C_element138  label="C_element : 083"  # scripted group (container) (typed FeaturePython)
  n = 4
  ref = C_element
FEATURE [App::DocumentObjectGroupPython] N_element058  label="N_element : 030"  # scripted group (container) (typed FeaturePython)
  n = 2
  ref = N_element
FEATURE [App::DocumentObjectGroupPython] O_element119  label="O_element : 072"  # scripted group (container) (typed FeaturePython)
  n = 2
  ref = O_element
FEATURE [App::DocumentObjectGroupPython] G4_DNA_URACIL  # scripted group (container) (typed FeaturePython)
  Dunit = g/cm3
  Dvalue = 1
  Group = -> [H_element128,C_element138,N_element058,O_element119]
  conduct = 2
  density = 1
  expand = 3
  formula = G4_DNA_URACIL
  name = G4_DNA_URACIL
  specific = 4
FEATURE [App::DocumentObjectGroupPython] H_element129  label="H_element : 076"  # scripted group (container) (typed FeaturePython)
  n = 10
  ref = H_element
FEATURE [App::DocumentObjectGroupPython] C_element139  label="C_element : 084"  # scripted group (container) (typed FeaturePython)
  n = 10
  ref = C_element
FEATURE [App::DocumentObjectGroupPython] N_element059  label="N_element : 031"  # scripted group (container) (typed FeaturePython)
  n = 5
  ref = N_element
FEATURE [App::DocumentObjectGroupPython] O_element120  label="O_element : 073"  # scripted group (container) (typed FeaturePython)
  n = 4
  ref = O_element
FEATURE [App::DocumentObjectGroupPython] G4_DNA_ADENOSINE  # scripted group (container) (typed FeaturePython)
  Dunit = g/cm3
  Dvalue = 1
  Group = -> [H_element129,C_element139,N_element059,O_element120]
  conduct = 2
  density = 1
  expand = 3
  formula = G4_DNA_ADENOSINE
  name = G4_DNA_ADENOSINE
  specific = 4
FEATURE [App::DocumentObjectGroupPython] H_element130  label="H_element : 077"  # scripted group (container) (typed FeaturePython)
  n = 10
  ref = H_element
FEATURE [App::DocumentObjectGroupPython] C_element140  label="C_element : 085"  # scripted group (container) (typed FeaturePython)
  n = 10
  ref = C_element
FEATURE [App::DocumentObjectGroupPython] N_element060  label="N_element : 032"  # scripted group (container) (typed FeaturePython)
  n = 5
  ref = N_element
FEATURE [App::DocumentObjectGroupPython] O_element121  label="O_element : 074"  # scripted group (container) (typed FeaturePython)
  n = 5
  ref = O_element
FEATURE [App::DocumentObjectGroupPython] G4_DNA_GUANOSINE  # scripted group (container) (typed FeaturePython)
  Dunit = g/cm3
  Dvalue = 1
  Group = -> [H_element130,C_element140,N_element060,O_element121]
  conduct = 2
  density = 1
  expand = 3
  formula = G4_DNA_GUANOSINE
  name = G4_DNA_GUANOSINE
  specific = 4
FEATURE [App::DocumentObjectGroupPython] H_element131  label="H_element : 078"  # scripted group (container) (typed FeaturePython)
  n = 10
  ref = H_element
FEATURE [App::DocumentObjectGroupPython] C_element141  label="C_element : 086"  # scripted group (container) (typed FeaturePython)
  n = 9
  ref = C_element
FEATURE [App::DocumentObjectGroupPython] N_element061  label="N_element : 033"  # scripted group (container) (typed FeaturePython)
  n = 3
  ref = N_element
FEATURE [App::DocumentObjectGroupPython] O_element122  label="O_element : 075"  # scripted group (container) (typed FeaturePython)
  n = 5
  ref = O_element
FEATURE [App::DocumentObjectGroupPython] G4_DNA_CYTIDINE  # scripted group (container) (typed FeaturePython)
  Dunit = g/cm3
  Dvalue = 1
  Group = -> [H_element131,C_element141,N_element061,O_element122]
  conduct = 2
  density = 1
  expand = 3
  formula = G4_DNA_CYTIDINE
  name = G4_DNA_CYTIDINE
  specific = 4
FEATURE [App::DocumentObjectGroupPython] H_element132  label="H_element : 079"  # scripted group (container) (typed FeaturePython)
  n = 9
  ref = H_element
FEATURE [App::DocumentObjectGroupPython] C_element142  label="C_element : 087"  # scripted group (container) (typed FeaturePython)
  n = 9
  ref = C_element
FEATURE [App::DocumentObjectGroupPython] N_element062  label="N_element : 034"  # scripted group (container) (typed FeaturePython)
  n = 2
  ref = N_element
FEATURE [App::DocumentObjectGroupPython] O_element123  label="O_element : 076"  # scripted group (container) (typed FeaturePython)
  n = 6
  ref = O_element
FEATURE [App::DocumentObjectGroupPython] G4_DNA_URIDINE  # scripted group (container) (typed FeaturePython)
  Dunit = g/cm3
  Dvalue = 1
  Group = -> [H_element132,C_element142,N_element062,O_element123]
  conduct = 2
  density = 1
  expand = 3
  formula = G4_DNA_URIDINE
  name = G4_DNA_URIDINE
  specific = 4
FEATURE [App::DocumentObjectGroupPython] H_element133  label="H_element : 080"  # scripted group (container) (typed FeaturePython)
  n = 11
  ref = H_element
FEATURE [App::DocumentObjectGroupPython] C_element143  label="C_element : 088"  # scripted group (container) (typed FeaturePython)
  n = 10
  ref = C_element
FEATURE [App::DocumentObjectGroupPython] N_element063  label="N_element : 035"  # scripted group (container) (typed FeaturePython)
  n = 2
  ref = N_element
FEATURE [App::DocumentObjectGroupPython] O_element124  label="O_element : 077"  # scripted group (container) (typed FeaturePython)
  n = 6
  ref = O_element
FEATURE [App::DocumentObjectGroupPython] G4_DNA_METHYLURIDINE  # scripted group (container) (typed FeaturePython)
  Dunit = g/cm3
  Dvalue = 1
  Group = -> [H_element133,C_element143,N_element063,O_element124]
  conduct = 2
  density = 1
  expand = 3
  formula = G4_DNA_METHYLURIDINE
  name = G4_DNA_METHYLURIDINE
  specific = 4
FEATURE [App::DocumentObjectGroupPython] P_element014  label="P_element : 003"  # scripted group (container) (typed FeaturePython)
  n = 1
  ref = P_element
FEATURE [App::DocumentObjectGroupPython] O_element125  label="O_element : 078"  # scripted group (container) (typed FeaturePython)
  n = 3
  ref = O_element
FEATURE [App::DocumentObjectGroupPython] G4_DNA_MONOPHOSPHATE  # scripted group (container) (typed FeaturePython)
  Dunit = g/cm3
  Dvalue = 1
  Group = -> [P_element014,O_element125]
  conduct = 2
  density = 1
  expand = 3
  formula = G4_DNA_MONOPHOSPHATE
  name = G4_DNA_MONOPHOSPHATE
  specific = 4
FEATURE [App::DocumentObjectGroupPython] H_element134  label="H_element : 081"  # scripted group (container) (typed FeaturePython)
  n = 10
  ref = H_element
FEATURE [App::DocumentObjectGroupPython] C_element144  label="C_element : 089"  # scripted group (container) (typed FeaturePython)
  n = 10
  ref = C_element
FEATURE [App::DocumentObjectGroupPython] N_element064  label="N_element : 036"  # scripted group (container) (typed FeaturePython)
  n = 5
  ref = N_element
FEATURE [App::DocumentObjectGroupPython] O_element126  label="O_element : 079"  # scripted group (container) (typed FeaturePython)
  n = 7
  ref = O_element
FEATURE [App::DocumentObjectGroupPython] P_element015  label="P_element : 004"  # scripted group (container) (typed FeaturePython)
  n = 1
  ref = P_element
FEATURE [App::DocumentObjectGroupPython] G4_DNA_A  # scripted group (container) (typed FeaturePython)
  Dunit = g/cm3
  Dvalue = 1
  Group = -> [H_element134,C_element144,N_element064,O_element126,P_element015]
  conduct = 2
  density = 1
  expand = 3
  formula = G4_DNA_A
  name = G4_DNA_A
  specific = 4
FEATURE [App::DocumentObjectGroupPython] H_element135  label="H_element : 082"  # scripted group (container) (typed FeaturePython)
  n = 10
  ref = H_element
FEATURE [App::DocumentObjectGroupPython] C_element145  label="C_element : 090"  # scripted group (container) (typed FeaturePython)
  n = 10
  ref = C_element
FEATURE [App::DocumentObjectGroupPython] N_element065  label="N_element : 037"  # scripted group (container) (typed FeaturePython)
  n = 5
  ref = N_element
FEATURE [App::DocumentObjectGroupPython] O_element127  label="O_element : 8"  # scripted group (container) (typed FeaturePython)
  n = 8
  ref = O_element
FEATURE [App::DocumentObjectGroupPython] P_element016  label="P_element : 005"  # scripted group (container) (typed FeaturePython)
  n = 1
  ref = P_element
FEATURE [App::DocumentObjectGroupPython] G4_DNA_G  # scripted group (container) (typed FeaturePython)
  Dunit = g/cm3
  Dvalue = 1
  Group = -> [H_element135,C_element145,N_element065,O_element127,P_element016]
  conduct = 2
  density = 1
  expand = 3
  formula = G4_DNA_G
  name = G4_DNA_G
  specific = 4
FEATURE [App::DocumentObjectGroupPython] H_element136  label="H_element : 083"  # scripted group (container) (typed FeaturePython)
  n = 10
  ref = H_element
FEATURE [App::DocumentObjectGroupPython] C_element146  label="C_element : 091"  # scripted group (container) (typed FeaturePython)
  n = 9
  ref = C_element
FEATURE [App::DocumentObjectGroupPython] N_element066  label="N_element : 038"  # scripted group (container) (typed FeaturePython)
  n = 3
  ref = N_element
FEATURE [App::DocumentObjectGroupPython] O_element128  label="O_element : 080"  # scripted group (container) (typed FeaturePython)
  n = 8
  ref = O_element
FEATURE [App::DocumentObjectGroupPython] P_element017  label="P_element : 006"  # scripted group (container) (typed FeaturePython)
  n = 1
  ref = P_element
FEATURE [App::DocumentObjectGroupPython] G4_DNA_C  # scripted group (container) (typed FeaturePython)
  Dunit = g/cm3
  Dvalue = 1
  Group = -> [H_element136,C_element146,N_element066,O_element128,P_element017]
  conduct = 2
  density = 1
  expand = 3
  formula = G4_DNA_C
  name = G4_DNA_C
  specific = 4
FEATURE [App::DocumentObjectGroupPython] H_element137  label="H_element : 084"  # scripted group (container) (typed FeaturePython)
  n = 9
  ref = H_element
FEATURE [App::DocumentObjectGroupPython] C_element147  label="C_element : 092"  # scripted group (container) (typed FeaturePython)
  n = 9
  ref = C_element
FEATURE [App::DocumentObjectGroupPython] N_element067  label="N_element : 039"  # scripted group (container) (typed FeaturePython)
  n = 2
  ref = N_element
FEATURE [App::DocumentObjectGroupPython] O_element129  label="O_element : 9"  # scripted group (container) (typed FeaturePython)
  n = 9
  ref = O_element
FEATURE [App::DocumentObjectGroupPython] P_element018  label="P_element : 007"  # scripted group (container) (typed FeaturePython)
  n = 1
  ref = P_element
FEATURE [App::DocumentObjectGroupPython] G4_DNA_U  # scripted group (container) (typed FeaturePython)
  Dunit = g/cm3
  Dvalue = 1
  Group = -> [H_element137,C_element147,N_element067,O_element129,P_element018]
  conduct = 2
  density = 1
  expand = 3
  formula = G4_DNA_U
  name = G4_DNA_U
  specific = 4
FEATURE [App::DocumentObjectGroupPython] H_element138  label="H_element : 085"  # scripted group (container) (typed FeaturePython)
  n = 11
  ref = H_element
FEATURE [App::DocumentObjectGroupPython] C_element148  label="C_element : 093"  # scripted group (container) (typed FeaturePython)
  n = 10
  ref = C_element
FEATURE [App::DocumentObjectGroupPython] N_element068  label="N_element : 040"  # scripted group (container) (typed FeaturePython)
  n = 2
  ref = N_element
FEATURE [App::DocumentObjectGroupPython] O_element130  label="O_element : 081"  # scripted group (container) (typed FeaturePython)
  n = 9
  ref = O_element
FEATURE [App::DocumentObjectGroupPython] P_element019  label="P_element : 008"  # scripted group (container) (typed FeaturePython)
  n = 1
  ref = P_element
FEATURE [App::DocumentObjectGroupPython] G4_DNA_MU  # scripted group (container) (typed FeaturePython)
  Dunit = g/cm3
  Dvalue = 1
  Group = -> [H_element138,C_element148,N_element068,O_element130,P_element019]
  conduct = 2
  density = 1
  expand = 3
  formula = G4_DNA_MU
  name = G4_DNA_MU
  specific = 4
FEATURE [App::DocumentObjectGroupPython] BioChemical  # scripted group (container) (typed FeaturePython)
  Group = -> [G4_CYTOSINE,G4_THYMINE,G4_URACIL,G4_DNA_ADENINE,G4_DNA_GUANINE,G4_DNA_CYTOSINE,G4_DNA_THYMINE,G4_DNA_URACIL,G4_DNA_ADENOSINE,G4_DNA_GUANOSINE,G4_DNA_CYTIDINE,G4_DNA_URIDINE,G4_DNA_METHYLURIDINE,G4_DNA_MONOPHOSPHATE,G4_DNA_A,G4_DNA_G,G4_DNA_C,G4_DNA_U,G4_DNA_MU]
FEATURE [App::DocumentObjectGroupPython] G4Materials  # scripted group (container) (typed FeaturePython)
  Group = -> [NIST,Element,HEP,Space,BioChemical]
  version = 1
FEATURE [App::DocumentObjectGroupPython] Geant4  # scripted group (container) (typed FeaturePython)
  Group = -> [G4Isotopes,G4Elements,G4Materials]
FEATURE [App::DocumentObjectGroupPython] Materials  # scripted group (container) (typed FeaturePython)
  Group = -> [Geant4]
FEATURE [Part::FeaturePython] GDMLBox_WorldBox  # WARN: FeaturePython — macro-defined, semantics opaque (R4)
  lunit = 2
  material = 5
  x = 100
  y = 100
  z = 100
FEATURE [Sketcher::SketchObject] Sketch
  ArcFitTolerance = 0
  FullyConstrained = false
  MakeInternals = false
  sketch-geometry (15):
    g0-g5: Circle [constr] x6 (B-spline internal-alignment scaffolding for g6; pole/knot coordinates omitted)
    g6: BSplineCurve PolesCount=7 KnotsCount=5 Degree=3 IsPeriodic=0
    g7-g10: GeomPoint [constr] x4 (B-spline internal-alignment scaffolding for g6; pole/knot coordinates omitted)
    g11: LineSegment StartX=-4.39557 StartY=8.39124 StartZ=0 EndX=-5.2662 EndY=10.5884 EndZ=0
    g12: LineSegment StartX=-5.2662 StartY=10.5884 StartZ=0 EndX=-7.82152 EndY=9.89481 EndZ=0
    g13: LineSegment StartX=-7.82152 StartY=9.89481 StartZ=0 EndX=-9.50073 EndY=7.63152 EndZ=0
    g14: ArcOfCircle CenterX=-7.8377 CenterY=5.34547 CenterZ=0 NormalX=0 NormalY=0 NormalZ=1 AngleXU=0 Radius=2.82696 StartAngle=4.84147 EndAngle=8.48291
  constraints (9):
    c: Weight(g0) = 1
    c: Equal(g0, g1-g5) x5
    c: InternalAlignment(g0-g5 -> g6) x6
    c: InternalAlignment(g7-g10 -> g6) x4
    c: Coincident(g11,g6)
    c: Coincident(g11,g12)
    c: Coincident(g12,g13)
    c: Coincident(g14,g13)
    c: Coincident(g14,g6)
FEATURE [Part::Extrusion] Extrude
  Base = -> Sketch
  Dir = (0,0,1)
  DirMode = 2
  FaceMakerClass = Part::FaceMakerBullseye
  FaceMakerMode = 3
  LengthFwd = 10
  LengthRev = 0
  Placement = pos=(13,12,0) rot=(0,0,1;0rad)
  Solid = true
  Symmetric = false
  material = 1
FEATURE [Part::Mirroring] Part__Mirroring  label="mirror1"
  Base = (0,0,0)
  Normal = (1,0,0)
  Placement = pos=(0,21,0) rot=(0,0,1;0rad)
  Source = -> Extrude
  material = 261
FEATURE [Part::Mirroring] Part__Mirroring002  label="mirror2"
  Base = (0,0,0)
  Normal = (0,1,0)
  Placement = pos=(-10,0,0) rot=(0,0,1;0rad)
  Source = -> Part__Mirroring
FEATURE [App::Part] Part
  Group = -> [Sketch,Extrude,Part__Mirroring,Part__Mirroring002]
  Origin = -> Origin001
FEATURE [App::Part] worldVOL
  Group = -> [GDMLBox_WorldBox,Part]
  Origin = -> Origin
